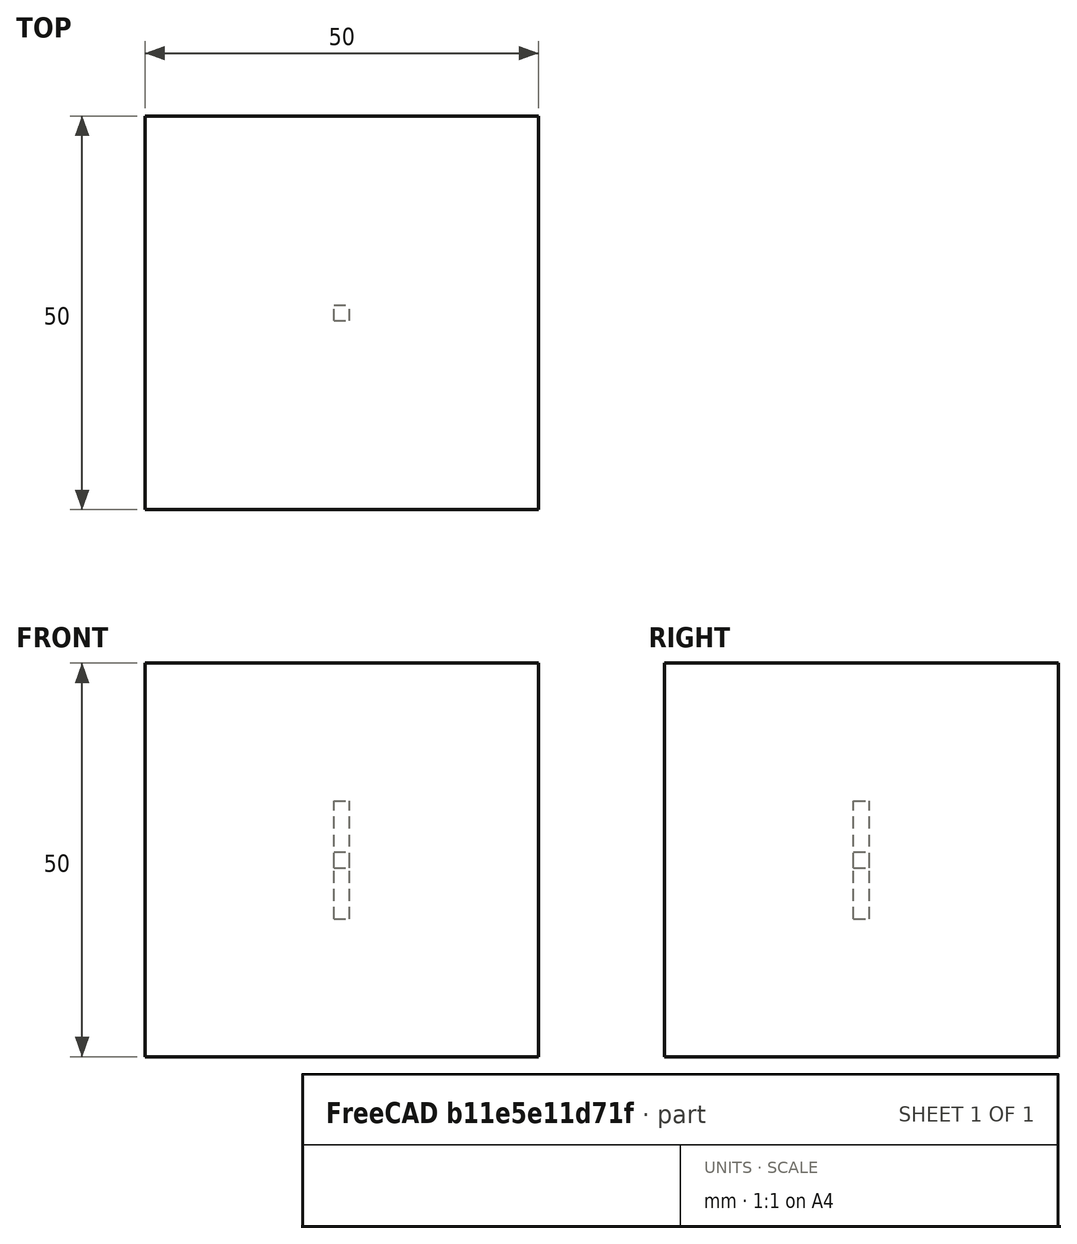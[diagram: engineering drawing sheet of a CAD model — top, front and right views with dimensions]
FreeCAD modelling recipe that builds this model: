
FCSTD DOCUMENT  (FreeCAD 0.22R36391 (Git))
Label: COG_Expanded_simple_array
License: All rights reserved
LicenseURL: http://en.wikipedia.org/wiki/All_rights_reserved
objects: App::DocumentObjectGroupPython×1269, App::Part×7, Part::FeaturePython×6, App::Link×4, App::FeaturePython×2
note: 5 computed .brp shape members not serialized (recipe doc carries the construction recipe); baked Part::Feature solids carry a one-line shape summary decoded from their .brp

FEATURE [App::DocumentObjectGroupPython] Constants  # scripted group (container) (typed FeaturePython)
FEATURE [App::DocumentObjectGroupPython] Variables  # scripted group (container) (typed FeaturePython)
FEATURE [App::DocumentObjectGroupPython] Quantities  # scripted group (container) (typed FeaturePython)
FEATURE [App::DocumentObjectGroupPython] Isotopes  # scripted group (container) (typed FeaturePython)
FEATURE [App::DocumentObjectGroupPython] Elements  # scripted group (container) (typed FeaturePython)
FEATURE [App::DocumentObjectGroupPython] G4_CESIUM_IODIDE  label="G4_CESIUM_IODIDE : 1.000"  # scripted group (container) (typed FeaturePython)
  n = 1
FEATURE [App::DocumentObjectGroupPython] LYSO  # scripted group (container) (typed FeaturePython)
  ABSLENGTH = ABSLENGTHLAR
  Dunit = g/cm3
  Dvalue = 7.1
  FASTCOMPONENT = SCINTLAR
  Group = -> [G4_CESIUM_IODIDE]
  RAYLEIGH = RAYLEIGHLAR
  REEMISSIONPROB = SCINTLAR
  RESOLUTIONSCALE = RS
  RINDEX = RINDEXLAR
  SCINTILLATIONCOMPONENT1 = SCINTLAR
  SCINTILLATIONCOMPONENT2 = SCINTLAR
  SCINTILLATIONTIMECONSTANT1 = FTC
  SCINTILLATIONTIMECONSTANT2 = STC
  SCINTILLATIONYIELD = SY
  SCINTILLATIONYIELD1 = RY1
  SCINTILLATIONYIELD2 = RY2
  SLOWCOMPONENT = SCINTLAR
  YIELDRATIO = YR
  conduct = 2
  density = 1
  expand = 3
  name = LYSO
  specific = 4
FEATURE [App::DocumentObjectGroupPython] G4_AIR  label="G4_AIR : 1.000"  # scripted group (container) (typed FeaturePython)
  n = 1
FEATURE [App::DocumentObjectGroupPython] Air  # scripted group (container) (typed FeaturePython)
  Dunit = mg/cm3
  Dvalue = 1.29
  Group = -> [G4_AIR]
  RINDEX = AirRINDEX
  conduct = 2
  density = 1
  expand = 3
  name = Air
  specific = 4
FEATURE [App::DocumentObjectGroupPython] G4_SILICON_DIOXIDE  label="G4_SILICON_DIOXIDE : 1.000"  # scripted group (container) (typed FeaturePython)
  n = 1
FEATURE [App::DocumentObjectGroupPython] Glass  # scripted group (container) (typed FeaturePython)
  Dunit = g/cm3
  Dvalue = 2.32
  Group = -> [G4_SILICON_DIOXIDE]
  RINDEX = RINDEXLAR
  conduct = 2
  density = 1
  expand = 3
  name = Glass
  specific = 4
FEATURE [App::DocumentObjectGroupPython] SY  # scripted group (container) (typed FeaturePython)
  coldim = 1
  values = 100000
FEATURE [App::DocumentObjectGroupPython] RS  # scripted group (container) (typed FeaturePython)
  coldim = 1
  values = 1
FEATURE [App::DocumentObjectGroupPython] FTC  # scripted group (container) (typed FeaturePython)
  coldim = 1
  values = 21.5*ns
FEATURE [App::DocumentObjectGroupPython] STC  # scripted group (container) (typed FeaturePython)
  coldim = 1
  values = 43.8*ns
FEATURE [App::DocumentObjectGroupPython] RY1  # scripted group (container) (typed FeaturePython)
  coldim = 1
  values = 95
FEATURE [App::DocumentObjectGroupPython] RY2  # scripted group (container) (typed FeaturePython)
  coldim = 1
  values = 5
FEATURE [App::DocumentObjectGroupPython] YR  # scripted group (container) (typed FeaturePython)
  coldim = 1
  values = 0.8
FEATURE [App::DocumentObjectGroupPython] SCINTLAR  # scripted group (container) (typed FeaturePython)
  coldim = 2
  values = <blob: 2358 chars omitted>
FEATURE [App::DocumentObjectGroupPython] RINDEXLAR  # scripted group (container) (typed FeaturePython)
  coldim = 2
  values = <blob: 9384 chars omitted>
FEATURE [App::DocumentObjectGroupPython] ABSLENGTHLAR  # scripted group (container) (typed FeaturePython)
  coldim = 2
  values = 7.74901*eV 10.0*m 7.77525*eV 10.0*m 7.80167*eV 10.0*m 7.82827*eV 10.0*m 7.85506*eV 10.0*m 7.88202*eV 10.0*m 7.90917*eV 10.0*m 7.93651*eV 10.0*m 7.96404*eV 10.0*m 7.99176*eV 10.0*m 8.01968*eV 10.0*m 8.04779*eV 10.0*m 8.07609*eV 10.0*m 8.1046*eV 10.0*m 8.13331*eV 10.0*m 8.16222*eV 10.0*m 8.19134*eV 10.0*m 8.22067*eV 10.0*m 8.25021*eV 10.0*m 8.27996*eV 10.0*m 8.30993*eV 10.0*m 8.34012*eV 10.0*m 8.37052*eV 10.0*m 8.40115*eV 10.0*m 8.432*eV 10.0*m 8.46308*eV 10.0*m 8.4944*eV 10.0*m 8.52594*eV 10.0*m 8.55772*eV 10.0*m 8.58973*eV 10.0*m 8.62199*eV 10.0*m 8.65449*eV 10.0*m 8.68723*eV 10.0*m 8.72023*eV 10.0*m 8.75347*eV 10.0*m 8.78697*eV 10.0*m 8.82073*eV 10.0*m 8.85475*eV 10.0*m 8.88903*eV 10.0*m 8.92358*eV 10.0*m 8.9584*eV 10.0*m 8.99349*eV 10.0*m 9.02885*eV 10.0*m 9.0645*eV 10.0*m 9.10043*eV 10.0*m 9.13664*eV 10.0*m 9.17314*eV 10.0*m 9.20994*eV 10.0*m 9.24703*eV 10.0*m 9.28442*eV 10.0*m 9.32212*eV 10.0*m 9.36012*eV 10.0*m 9.39844*eV 10.0*m 9.43707*eV 10.0*m 9.47602*eV 10.0*m 9.51529*eV 10.0*m 9.55489*eV 10.0*m 9.59481*eV 10.0*m 9.63508*eV 10.0*m 9.67568*eV 10.0*m 9.71663*eV 10.0*m 9.75792*eV 10.0*m 9.79957*eV 10.0*m 9.84158*eV 10.0*m 9.88394*eV 10.0*m 9.92668*eV 10.0*m 9.96978*eV 10.0*m 10.0133*eV 10.0*m 10.0571*eV 10.0*m 10.1014*eV 10.0*m 10.146*eV 10.0*m 10.191*eV 10.0*m 10.2365*eV 10.0*m 10.2823*eV 10.0*m 10.3286*eV 10.0*m 10.3752*eV 10.0*m 10.4223*eV 10.0*m 10.4699*eV 10.0*m 10.5178*eV 10.0*m 10.5662*eV 10.0*m 10.6151*eV 10.0*m 10.6644*eV 10.0*m 10.7142*eV 10.0*m 10.7644*eV 10.0*m 10.8151*eV 10.0*m 10.8663*eV 10.0*m 10.9179*eV 10.0*m 10.9701*eV 10.0*m 11.0228*eV 10.0*m 11.076*eV 10.0*m 11.1296*eV 10.0*m 11.1839*eV 10.0*m 11.2386*eV 10.0*m 11.2939*eV 10.0*m 11.3497*eV 10.0*m 11.4061*eV 10.0*m 11.463*eV 10.0*m 11.5206*eV 10.0*m 11.5787*eV 10.0*m 11.6373*eV 10.0*m
FEATURE [App::DocumentObjectGroupPython] RAYLEIGHLAR  # scripted group (container) (typed FeaturePython)
  coldim = 2
  values = 7.74901*eV 90.0*cm 7.77525*eV 90.0*cm 7.80167*eV 90.0*cm 7.82827*eV 90.0*cm 7.85506*eV 90.0*cm 7.88202*eV 90.0*cm 7.90917*eV 90.0*cm 7.93651*eV 90.0*cm 7.96404*eV 90.0*cm 7.99176*eV 90.0*cm 8.01968*eV 90.0*cm 8.04779*eV 90.0*cm 8.07609*eV 90.0*cm 8.1046*eV 90.0*cm 8.13331*eV 90.0*cm 8.16222*eV 90.0*cm 8.19134*eV 90.0*cm 8.22067*eV 90.0*cm 8.25021*eV 90.0*cm 8.27996*eV 90.0*cm 8.30993*eV 90.0*cm 8.34012*eV 90.0*cm 8.37052*eV 90.0*cm 8.40115*eV 90.0*cm 8.432*eV 90.0*cm 8.46308*eV 90.0*cm 8.4944*eV 90.0*cm 8.52594*eV 90.0*cm 8.55772*eV 90.0*cm 8.58973*eV 90.0*cm 8.62199*eV 90.0*cm 8.65449*eV 90.0*cm 8.68723*eV 90.0*cm 8.72023*eV 90.0*cm 8.75347*eV 90.0*cm 8.78697*eV 90.0*cm 8.82073*eV 90.0*cm 8.85475*eV 90.0*cm 8.88903*eV 90.0*cm 8.92358*eV 90.0*cm 8.9584*eV 90.0*cm 8.99349*eV 90.0*cm 9.02885*eV 90.0*cm 9.0645*eV 90.0*cm 9.10043*eV 90.0*cm 9.13664*eV 90.0*cm 9.17314*eV 90.0*cm 9.20994*eV 90.0*cm 9.24703*eV 90.0*cm 9.28442*eV 90.0*cm 9.32212*eV 90.0*cm 9.36012*eV 90.0*cm 9.39844*eV 90.0*cm 9.43707*eV 90.0*cm 9.47602*eV 90.0*cm 9.51529*eV 90.0*cm 9.55489*eV 90.0*cm 9.59481*eV 90.0*cm 9.63508*eV 90.0*cm 9.67568*eV 90.0*cm 9.71663*eV 90.0*cm 9.75792*eV 90.0*cm 9.79957*eV 90.0*cm 9.84158*eV 90.0*cm 9.88394*eV 90.0*cm 9.92668*eV 90.0*cm 9.96978*eV 90.0*cm 10.0133*eV 90.0*cm 10.0571*eV 90.0*cm 10.1014*eV 90.0*cm 10.146*eV 90.0*cm 10.191*eV 90.0*cm 10.2365*eV 90.0*cm 10.2823*eV 90.0*cm 10.3286*eV 90.0*cm 10.3752*eV 90.0*cm 10.4223*eV 90.0*cm 10.4699*eV 90.0*cm 10.5178*eV 90.0*cm 10.5662*eV 90.0*cm 10.6151*eV 90.0*cm 10.6644*eV 90.0*cm 10.7142*eV 90.0*cm 10.7644*eV 90.0*cm 10.8151*eV 90.0*cm 10.8663*eV 90.0*cm 10.9179*eV 90.0*cm 10.9701*eV 90.0*cm 11.0228*eV 90.0*cm 11.076*eV 90.0*cm 11.1296*eV 90.0*cm 11.1839*eV 90.0*cm 11.2386*eV 90.0*cm 11.2939*eV 90.0*cm 11.3497*eV 90.0*cm 11.4061*eV 90.0*cm 11.463*eV 90.0*cm 11.5206*eV 90.0*cm 11.5787*eV 90.0*cm 11.6373*eV 90.0*cm
FEATURE [App::DocumentObjectGroupPython] REFLECTIVITY  # scripted group (container) (typed FeaturePython)
  coldim = 2
  values = 2.034*eV 0.98 2.068*eV 0.98 2.103*eV 0.98 2.139*eV 0.98 2.177*eV 0.98 2.216*eV 0.98 2.256*eV 0.98 2.298*eV 0.98 2.341*eV 0.98 2.386*eV 0.98 2.433*eV 0.98 2.481*eV 0.98 2.532*eV 0.98 2.585*eV 0.98 2.64*eV 0.98 2.697*eV 0.98 2.757*eV 0.98 2.82*eV 0.98 2.885*eV 0.98 2.954*eV 0.98 3.026*eV 0.98 3.102*eV 0.98 3.181*eV 0.98 3.265*eV 0.98 3.353*eV 0.98 3.446*eV 0.98 3.545*eV 0.98 3.649*eV 0.98 3.76*eV 0.98 3.877*eV 0.98 4.002*eV 0.98 4.136*eV 0.98 5.0*eV 0.98 6.0*eV 0.98 7.0*eV 0.98 8.0*eV 0.98 9.0*eV 0.98 9.0*eV 0.98 10.0*eV 0.98 11.0*eV 0.98 11.6*eV 0.98
FEATURE [App::DocumentObjectGroupPython] EFFICIENCY  # scripted group (container) (typed FeaturePython)
  coldim = 2
  values = 2.034*eV 1 2.068*eV 1 2.103*eV 1 2.139*eV 1 2.177*eV 1 2.216*eV 1 2.256*eV 1 2.298*eV 1 2.341*eV 1 2.386*eV 1 2.433*eV 1 2.481*eV 1 2.532*eV 1 2.585*eV 1 2.64*eV 1 2.697*eV 1 2.757*eV 1 2.82*eV 1 2.885*eV 1 2.954*eV 1 3.026*eV 1 3.102*eV 1 3.181*eV  1 3.265*eV 1 3.353*eV 1 3.446*eV 1 3.545*eV 1 3.649*eV 1 3.76*eV 1 3.877*eV 1 4.002*eV 1 4.136*eV 1 5.0*eV 1 6.0*eV 1 7.0*eV 1 8.0*eV 1 9.0*eV 1 9.0*eV 1 10.0*eV 1 11.0*eV 1 11.6*eV 1
FEATURE [App::DocumentObjectGroupPython] AirRINDEX  # scripted group (container) (typed FeaturePython)
  coldim = 2
  values = 2.034*eV 1 2.068*eV 1 2.103*eV 1 2.139*eV 1 2.177*eV 1 2.216*eV 1 2.256*eV 1 2.298*eV 1 2.341*eV 1 2.386*eV 1 2.433*eV 1 2.481*eV 1 2.532*eV 1 2.585*eV 1 2.64*eV 1 2.697*eV 1 2.757*eV 1 2.82*eV 1 2.885*eV 1 2.954*eV 1 3.026*eV 1 3.102*eV 1 3.181*eV 1 3.265*eV 1 3.353*eV 1 3.446*eV 1 3.545*eV 1 3.649*eV 1 3.76*eV 1 3.877*eV 1 4.002*eV 1 4.136*eV 1 5.0*eV 1 6.0*eV 1 7.0*eV 1 8.0*eV 1 9.0*eV 1 10.0*eV 1 11.0*eV 1 11.6*eV 1
FEATURE [App::DocumentObjectGroupPython] Matrix  # scripted group (container) (typed FeaturePython)
  Group = -> [SY,RS,FTC,STC,RY1,RY2,YR,SCINTLAR,RINDEXLAR,ABSLENGTHLAR,RAYLEIGHLAR,REFLECTIVITY,EFFICIENCY,AirRINDEX]
FEATURE [App::DocumentObjectGroupPython] ScintWrap  # scripted group (container) (typed FeaturePython)
  EFFICIENCY = EFFICIENCY
  REFLECTIVITY = REFLECTIVITY
  finish = 39
  model = 0
  type = 2
  value = 1
FEATURE [App::DocumentObjectGroupPython] Surfaces  # scripted group (container) (typed FeaturePython)
  Group = -> [ScintWrap]
FEATURE [App::DocumentObjectGroupPython] Opticals  # scripted group (container) (typed FeaturePython)
  Group = -> [Matrix,Surfaces]
FEATURE [App::DocumentObjectGroupPython] G4Isotopes  # scripted group (container) (typed FeaturePython)
FEATURE [App::DocumentObjectGroupPython] H_element  # scripted group (container) (typed FeaturePython)
  Z = 1
  atom_value = 1.008
  formula = H
  name = H_element
FEATURE [App::DocumentObjectGroupPython] He_element  # scripted group (container) (typed FeaturePython)
  Z = 2
  atom_value = 4.0026
  formula = He
  name = He_element
FEATURE [App::DocumentObjectGroupPython] Li_element  # scripted group (container) (typed FeaturePython)
  Z = 3
  atom_value = 6.94
  formula = Li
  name = Li_element
FEATURE [App::DocumentObjectGroupPython] Be_element  # scripted group (container) (typed FeaturePython)
  Z = 4
  atom_value = 9.01218
  formula = Be
  name = Be_element
FEATURE [App::DocumentObjectGroupPython] B_element  # scripted group (container) (typed FeaturePython)
  Z = 5
  atom_value = 10.81
  formula = B
  name = B_element
FEATURE [App::DocumentObjectGroupPython] C_element  # scripted group (container) (typed FeaturePython)
  Z = 6
  atom_value = 12.011
  formula = C
  name = C_element
FEATURE [App::DocumentObjectGroupPython] N_element  # scripted group (container) (typed FeaturePython)
  Z = 7
  atom_value = 14.007
  formula = N
  name = N_element
FEATURE [App::DocumentObjectGroupPython] O_element  # scripted group (container) (typed FeaturePython)
  Z = 8
  atom_value = 15.999
  formula = O
  name = O_element
FEATURE [App::DocumentObjectGroupPython] F_element  # scripted group (container) (typed FeaturePython)
  Z = 9
  atom_value = 18.9984
  formula = F
  name = F_element
FEATURE [App::DocumentObjectGroupPython] Ne_element  # scripted group (container) (typed FeaturePython)
  Z = 10
  atom_value = 20.1797
  formula = Ne
  name = Ne_element
FEATURE [App::DocumentObjectGroupPython] Na_element  # scripted group (container) (typed FeaturePython)
  Z = 11
  atom_value = 22.9898
  formula = Na
  name = Na_element
FEATURE [App::DocumentObjectGroupPython] Mg_element  # scripted group (container) (typed FeaturePython)
  Z = 12
  atom_value = 24.305
  formula = Mg
  name = Mg_element
FEATURE [App::DocumentObjectGroupPython] Al_element  # scripted group (container) (typed FeaturePython)
  Z = 13
  atom_value = 26.9815
  formula = Al
  name = Al_element
FEATURE [App::DocumentObjectGroupPython] Si_element  # scripted group (container) (typed FeaturePython)
  Z = 14
  atom_value = 28.085
  formula = Si
  name = Si_element
FEATURE [App::DocumentObjectGroupPython] P_element  # scripted group (container) (typed FeaturePython)
  Z = 15
  atom_value = 30.9738
  formula = P
  name = P_element
FEATURE [App::DocumentObjectGroupPython] S_element  # scripted group (container) (typed FeaturePython)
  Z = 16
  atom_value = 32.06
  formula = S
  name = S_element
FEATURE [App::DocumentObjectGroupPython] Cl_element  # scripted group (container) (typed FeaturePython)
  Z = 17
  atom_value = 35.45
  formula = Cl
  name = Cl_element
FEATURE [App::DocumentObjectGroupPython] Ar_element  # scripted group (container) (typed FeaturePython)
  Z = 18
  atom_value = 39.95
  formula = Ar
  name = Ar_element
FEATURE [App::DocumentObjectGroupPython] K_element  # scripted group (container) (typed FeaturePython)
  Z = 19
  atom_value = 39.0983
  formula = K
  name = K_element
FEATURE [App::DocumentObjectGroupPython] Ca_element  # scripted group (container) (typed FeaturePython)
  Z = 20
  atom_value = 40.078
  formula = Ca
  name = Ca_element
FEATURE [App::DocumentObjectGroupPython] Sc_element  # scripted group (container) (typed FeaturePython)
  Z = 21
  atom_value = 44.9559
  formula = Sc
  name = Sc_element
FEATURE [App::DocumentObjectGroupPython] Ti_element  # scripted group (container) (typed FeaturePython)
  Z = 22
  atom_value = 47.867
  formula = Ti
  name = Ti_element
FEATURE [App::DocumentObjectGroupPython] V_element  # scripted group (container) (typed FeaturePython)
  Z = 23
  atom_value = 50.9415
  formula = V
  name = V_element
FEATURE [App::DocumentObjectGroupPython] Cr_element  # scripted group (container) (typed FeaturePython)
  Z = 24
  atom_value = 51.9961
  formula = Cr
  name = Cr_element
FEATURE [App::DocumentObjectGroupPython] Mn_element  # scripted group (container) (typed FeaturePython)
  Z = 25
  atom_value = 54.938
  formula = Mn
  name = Mn_element
FEATURE [App::DocumentObjectGroupPython] Fe_element  # scripted group (container) (typed FeaturePython)
  Z = 26
  atom_value = 55.845
  formula = Fe
  name = Fe_element
FEATURE [App::DocumentObjectGroupPython] Co_element  # scripted group (container) (typed FeaturePython)
  Z = 27
  atom_value = 58.9332
  formula = Co
  name = Co_element
FEATURE [App::DocumentObjectGroupPython] Ni_element  # scripted group (container) (typed FeaturePython)
  Z = 28
  atom_value = 58.6934
  formula = Ni
  name = Ni_element
FEATURE [App::DocumentObjectGroupPython] Cu_element  # scripted group (container) (typed FeaturePython)
  Z = 29
  atom_value = 63.546
  formula = Cu
  name = Cu_element
FEATURE [App::DocumentObjectGroupPython] Zn_element  # scripted group (container) (typed FeaturePython)
  Z = 30
  atom_value = 65.38
  formula = Zn
  name = Zn_element
FEATURE [App::DocumentObjectGroupPython] Ga_element  # scripted group (container) (typed FeaturePython)
  Z = 31
  atom_value = 69.723
  formula = Ga
  name = Ga_element
FEATURE [App::DocumentObjectGroupPython] Ge_element  # scripted group (container) (typed FeaturePython)
  Z = 32
  atom_value = 72.63
  formula = Ge
  name = Ge_element
FEATURE [App::DocumentObjectGroupPython] As_element  # scripted group (container) (typed FeaturePython)
  Z = 33
  atom_value = 74.9216
  formula = As
  name = As_element
FEATURE [App::DocumentObjectGroupPython] Se_element  # scripted group (container) (typed FeaturePython)
  Z = 34
  atom_value = 78.971
  formula = Se
  name = Se_element
FEATURE [App::DocumentObjectGroupPython] Br_element  # scripted group (container) (typed FeaturePython)
  Z = 35
  atom_value = 79.904
  formula = Br
  name = Br_element
FEATURE [App::DocumentObjectGroupPython] Kr_element  # scripted group (container) (typed FeaturePython)
  Z = 36
  atom_value = 83.798
  formula = Kr
  name = Kr_element
FEATURE [App::DocumentObjectGroupPython] Rb_element  # scripted group (container) (typed FeaturePython)
  Z = 37
  atom_value = 85.4678
  formula = Rb
  name = Rb_element
FEATURE [App::DocumentObjectGroupPython] Sr_element  # scripted group (container) (typed FeaturePython)
  Z = 38
  atom_value = 87.62
  formula = Sr
  name = Sr_element
FEATURE [App::DocumentObjectGroupPython] Y_element  # scripted group (container) (typed FeaturePython)
  Z = 39
  atom_value = 88.9058
  formula = Y
  name = Y_element
FEATURE [App::DocumentObjectGroupPython] Zr_element  # scripted group (container) (typed FeaturePython)
  Z = 40
  atom_value = 91.224
  formula = Zr
  name = Zr_element
FEATURE [App::DocumentObjectGroupPython] Nb_element  # scripted group (container) (typed FeaturePython)
  Z = 41
  atom_value = 92.9064
  formula = Nb
  name = Nb_element
FEATURE [App::DocumentObjectGroupPython] Mo_element  # scripted group (container) (typed FeaturePython)
  Z = 42
  atom_value = 95.95
  formula = Mo
  name = Mo_element
FEATURE [App::DocumentObjectGroupPython] Tc_element  # scripted group (container) (typed FeaturePython)
  Z = 43
  atom_value = 97
  formula = Tc
  name = Tc_element
FEATURE [App::DocumentObjectGroupPython] Ru_element  # scripted group (container) (typed FeaturePython)
  Z = 44
  atom_value = 101.07
  formula = Ru
  name = Ru_element
FEATURE [App::DocumentObjectGroupPython] Rh_element  # scripted group (container) (typed FeaturePython)
  Z = 45
  atom_value = 102.905
  formula = Rh
  name = Rh_element
FEATURE [App::DocumentObjectGroupPython] Pd_element  # scripted group (container) (typed FeaturePython)
  Z = 46
  atom_value = 106.42
  formula = Pd
  name = Pd_element
FEATURE [App::DocumentObjectGroupPython] Ag_element  # scripted group (container) (typed FeaturePython)
  Z = 47
  atom_value = 107.868
  formula = Ag
  name = Ag_element
FEATURE [App::DocumentObjectGroupPython] Cd_element  # scripted group (container) (typed FeaturePython)
  Z = 48
  atom_value = 112.414
  formula = Cd
  name = Cd_element
FEATURE [App::DocumentObjectGroupPython] In_element  # scripted group (container) (typed FeaturePython)
  Z = 49
  atom_value = 114.818
  formula = In
  name = In_element
FEATURE [App::DocumentObjectGroupPython] Sn_element  # scripted group (container) (typed FeaturePython)
  Z = 50
  atom_value = 118.71
  formula = Sn
  name = Sn_element
FEATURE [App::DocumentObjectGroupPython] Sb_element  # scripted group (container) (typed FeaturePython)
  Z = 51
  atom_value = 121.76
  formula = Sb
  name = Sb_element
FEATURE [App::DocumentObjectGroupPython] Te_element  # scripted group (container) (typed FeaturePython)
  Z = 52
  atom_value = 127.6
  formula = Te
  name = Te_element
FEATURE [App::DocumentObjectGroupPython] I_element  # scripted group (container) (typed FeaturePython)
  Z = 53
  atom_value = 126.904
  formula = I
  name = I_element
FEATURE [App::DocumentObjectGroupPython] Xe_element  # scripted group (container) (typed FeaturePython)
  Z = 54
  atom_value = 131.293
  formula = Xe
  name = Xe_element
FEATURE [App::DocumentObjectGroupPython] Cs_element  # scripted group (container) (typed FeaturePython)
  Z = 55
  atom_value = 132.905
  formula = Cs
  name = Cs_element
FEATURE [App::DocumentObjectGroupPython] Ba_element  # scripted group (container) (typed FeaturePython)
  Z = 56
  atom_value = 137.327
  formula = Ba
  name = Ba_element
FEATURE [App::DocumentObjectGroupPython] La_element  # scripted group (container) (typed FeaturePython)
  Z = 57
  atom_value = 138.905
  formula = La
  name = La_element
FEATURE [App::DocumentObjectGroupPython] Ce_element  # scripted group (container) (typed FeaturePython)
  Z = 58
  atom_value = 140.116
  formula = Ce
  name = Ce_element
FEATURE [App::DocumentObjectGroupPython] Pr_element  # scripted group (container) (typed FeaturePython)
  Z = 59
  atom_value = 140.908
  formula = Pr
  name = Pr_element
FEATURE [App::DocumentObjectGroupPython] Nd_element  # scripted group (container) (typed FeaturePython)
  Z = 60
  atom_value = 144.242
  formula = Nd
  name = Nd_element
FEATURE [App::DocumentObjectGroupPython] Pm_element  # scripted group (container) (typed FeaturePython)
  Z = 61
  atom_value = 145
  formula = Pm
  name = Pm_element
FEATURE [App::DocumentObjectGroupPython] Sm_element  # scripted group (container) (typed FeaturePython)
  Z = 62
  atom_value = 150.36
  formula = Sm
  name = Sm_element
FEATURE [App::DocumentObjectGroupPython] Eu_element  # scripted group (container) (typed FeaturePython)
  Z = 63
  atom_value = 151.964
  formula = Eu
  name = Eu_element
FEATURE [App::DocumentObjectGroupPython] Gd_element  # scripted group (container) (typed FeaturePython)
  Z = 64
  atom_value = 157.25
  formula = Gd
  name = Gd_element
FEATURE [App::DocumentObjectGroupPython] Tb_element  # scripted group (container) (typed FeaturePython)
  Z = 65
  atom_value = 158.925
  formula = Tb
  name = Tb_element
FEATURE [App::DocumentObjectGroupPython] Dy_element  # scripted group (container) (typed FeaturePython)
  Z = 66
  atom_value = 162.5
  formula = Dy
  name = Dy_element
FEATURE [App::DocumentObjectGroupPython] Ho_element  # scripted group (container) (typed FeaturePython)
  Z = 67
  atom_value = 164.93
  formula = Ho
  name = Ho_element
FEATURE [App::DocumentObjectGroupPython] Er_element  # scripted group (container) (typed FeaturePython)
  Z = 68
  atom_value = 167.259
  formula = Er
  name = Er_element
FEATURE [App::DocumentObjectGroupPython] Tm_element  # scripted group (container) (typed FeaturePython)
  Z = 69
  atom_value = 168.934
  formula = Tm
  name = Tm_element
FEATURE [App::DocumentObjectGroupPython] Yb_element  # scripted group (container) (typed FeaturePython)
  Z = 70
  atom_value = 173.045
  formula = Yb
  name = Yb_element
FEATURE [App::DocumentObjectGroupPython] Lu_element  # scripted group (container) (typed FeaturePython)
  Z = 71
  atom_value = 174.967
  formula = Lu
  name = Lu_element
FEATURE [App::DocumentObjectGroupPython] Hf_element  # scripted group (container) (typed FeaturePython)
  Z = 72
  atom_value = 178.49
  formula = Hf
  name = Hf_element
FEATURE [App::DocumentObjectGroupPython] Ta_element  # scripted group (container) (typed FeaturePython)
  Z = 73
  atom_value = 180.948
  formula = Ta
  name = Ta_element
FEATURE [App::DocumentObjectGroupPython] W_element  # scripted group (container) (typed FeaturePython)
  Z = 74
  atom_value = 183.84
  formula = W
  name = W_element
FEATURE [App::DocumentObjectGroupPython] Re_element  # scripted group (container) (typed FeaturePython)
  Z = 75
  atom_value = 186.207
  formula = Re
  name = Re_element
FEATURE [App::DocumentObjectGroupPython] Os_element  # scripted group (container) (typed FeaturePython)
  Z = 76
  atom_value = 190.23
  formula = Os
  name = Os_element
FEATURE [App::DocumentObjectGroupPython] Ir_element  # scripted group (container) (typed FeaturePython)
  Z = 77
  atom_value = 192.217
  formula = Ir
  name = Ir_element
FEATURE [App::DocumentObjectGroupPython] Pt_element  # scripted group (container) (typed FeaturePython)
  Z = 78
  atom_value = 195.084
  formula = Pt
  name = Pt_element
FEATURE [App::DocumentObjectGroupPython] Au_element  # scripted group (container) (typed FeaturePython)
  Z = 79
  atom_value = 196.967
  formula = Au
  name = Au_element
FEATURE [App::DocumentObjectGroupPython] Hg_element  # scripted group (container) (typed FeaturePython)
  Z = 80
  atom_value = 200.592
  formula = Hg
  name = Hg_element
FEATURE [App::DocumentObjectGroupPython] Tl_element  # scripted group (container) (typed FeaturePython)
  Z = 81
  atom_value = 204.38
  formula = Tl
  name = Tl_element
FEATURE [App::DocumentObjectGroupPython] Pb_element  # scripted group (container) (typed FeaturePython)
  Z = 82
  atom_value = 207.2
  formula = Pb
  name = Pb_element
FEATURE [App::DocumentObjectGroupPython] Bi_element  # scripted group (container) (typed FeaturePython)
  Z = 83
  atom_value = 208.98
  formula = Bi
  name = Bi_element
FEATURE [App::DocumentObjectGroupPython] Po_element  # scripted group (container) (typed FeaturePython)
  Z = 84
  atom_value = 209
  formula = Po
  name = Po_element
FEATURE [App::DocumentObjectGroupPython] At_element  # scripted group (container) (typed FeaturePython)
  Z = 85
  atom_value = 210
  formula = At
  name = At_element
FEATURE [App::DocumentObjectGroupPython] Rn_element  # scripted group (container) (typed FeaturePython)
  Z = 86
  atom_value = 222
  formula = Rn
  name = Rn_element
FEATURE [App::DocumentObjectGroupPython] Fr_element  # scripted group (container) (typed FeaturePython)
  Z = 87
  atom_value = 223
  formula = Fr
  name = Fr_element
FEATURE [App::DocumentObjectGroupPython] Ra_element  # scripted group (container) (typed FeaturePython)
  Z = 88
  atom_value = 226
  formula = Ra
  name = Ra_element
FEATURE [App::DocumentObjectGroupPython] Ac_element  # scripted group (container) (typed FeaturePython)
  Z = 89
  atom_value = 227
  formula = Ac
  name = Ac_element
FEATURE [App::DocumentObjectGroupPython] Th_element  # scripted group (container) (typed FeaturePython)
  Z = 90
  atom_value = 232.038
  formula = Th
  name = Th_element
FEATURE [App::DocumentObjectGroupPython] Pa_element  # scripted group (container) (typed FeaturePython)
  Z = 91
  atom_value = 231.036
  formula = Pa
  name = Pa_element
FEATURE [App::DocumentObjectGroupPython] U_element  # scripted group (container) (typed FeaturePython)
  Z = 92
  atom_value = 238.029
  formula = U
  name = U_element
FEATURE [App::DocumentObjectGroupPython] Np_element  # scripted group (container) (typed FeaturePython)
  Z = 93
  atom_value = 237
  formula = Np
  name = Np_element
FEATURE [App::DocumentObjectGroupPython] Pu_element  # scripted group (container) (typed FeaturePython)
  Z = 94
  atom_value = 244
  formula = Pu
  name = Pu_element
FEATURE [App::DocumentObjectGroupPython] Am_element  # scripted group (container) (typed FeaturePython)
  Z = 95
  atom_value = 243
  formula = Am
  name = Am_element
FEATURE [App::DocumentObjectGroupPython] Cm_element  # scripted group (container) (typed FeaturePython)
  Z = 96
  atom_value = 247
  formula = Cm
  name = Cm_element
FEATURE [App::DocumentObjectGroupPython] Bk_element  # scripted group (container) (typed FeaturePython)
  Z = 97
  atom_value = 247
  formula = Bk
  name = Bk_element
FEATURE [App::DocumentObjectGroupPython] Cf_element  # scripted group (container) (typed FeaturePython)
  Z = 98
  atom_value = 251
  formula = Cf
  name = Cf_element
FEATURE [App::DocumentObjectGroupPython] G4Elements  # scripted group (container) (typed FeaturePython)
  Group = -> [H_element,He_element,Li_element,Be_element,B_element,C_element,N_element,O_element,F_element,Ne_element,Na_element,Mg_element,Al_element,Si_element,P_element,S_element,Cl_element,Ar_element,K_element,Ca_element,Sc_element,Ti_element,V_element,Cr_element,Mn_element,Fe_element,Co_element,Ni_element,Cu_element,Zn_element,Ga_element,Ge_element,As_element,Se_element,Br_element,Kr_element,Rb_element,+61 more]
FEATURE [App::DocumentObjectGroupPython] H_element001  label="H_element : 0.101"  # scripted group (container) (typed FeaturePython)
  n = 0.101327
FEATURE [App::DocumentObjectGroupPython] C_element001  label="C_element : 0.775"  # scripted group (container) (typed FeaturePython)
  n = 0.7755
FEATURE [App::DocumentObjectGroupPython] N_element001  label="N_element : 0.035"  # scripted group (container) (typed FeaturePython)
  n = 0.035057
FEATURE [App::DocumentObjectGroupPython] O_element001  label="O_element : 0.052"  # scripted group (container) (typed FeaturePython)
  n = 0.0523159
FEATURE [App::DocumentObjectGroupPython] F_element001  label="F_element : 0.017"  # scripted group (container) (typed FeaturePython)
  n = 0.017422
FEATURE [App::DocumentObjectGroupPython] Ca_element001  label="Ca_element : 0.018"  # scripted group (container) (typed FeaturePython)
  n = 0.018378
FEATURE [App::DocumentObjectGroupPython] G4_A_150_TISSUE  label="G4_A-150_TISSUE"  # scripted group (container) (typed FeaturePython)
  Dunit = g/cm3
  Dvalue = 1.127
  Group = -> [H_element001,C_element001,N_element001,O_element001,F_element001,Ca_element001]
  conduct = 2
  density = 1
  expand = 3
  formula = G4_A-150_TISSUE
  name = G4_A-150_TISSUE
  specific = 4
FEATURE [App::DocumentObjectGroupPython] C_element002  label="C_element : 3"  # scripted group (container) (typed FeaturePython)
  n = 3
  ref = C_element
FEATURE [App::DocumentObjectGroupPython] H_element002  label="H_element : 6"  # scripted group (container) (typed FeaturePython)
  n = 6
  ref = H_element
FEATURE [App::DocumentObjectGroupPython] O_element002  label="O_element : 1"  # scripted group (container) (typed FeaturePython)
  n = 1
  ref = O_element
FEATURE [App::DocumentObjectGroupPython] G4_ACETONE  # scripted group (container) (typed FeaturePython)
  Dunit = g/cm3
  Dvalue = 0.7899
  Group = -> [C_element002,H_element002,O_element002]
  conduct = 2
  density = 1
  expand = 3
  formula = G4_ACETONE
  name = G4_ACETONE
  specific = 4
FEATURE [App::DocumentObjectGroupPython] C_element003  label="C_element : 2"  # scripted group (container) (typed FeaturePython)
  n = 2
  ref = C_element
FEATURE [App::DocumentObjectGroupPython] H_element003  label="H_element : 2"  # scripted group (container) (typed FeaturePython)
  n = 2
  ref = H_element
FEATURE [App::DocumentObjectGroupPython] G4_ACETYLENE  # scripted group (container) (typed FeaturePython)
  Dunit = g/cm3
  Dvalue = 0.0010967
  Group = -> [C_element003,H_element003]
  conduct = 2
  density = 1
  expand = 3
  formula = G4_ACETYLENE
  name = G4_ACETYLENE
  specific = 4
FEATURE [App::DocumentObjectGroupPython] C_element004  label="C_element : 5"  # scripted group (container) (typed FeaturePython)
  n = 5
  ref = C_element
FEATURE [App::DocumentObjectGroupPython] H_element004  label="H_element : 5"  # scripted group (container) (typed FeaturePython)
  n = 5
  ref = H_element
FEATURE [App::DocumentObjectGroupPython] N_element002  label="N_element : 5"  # scripted group (container) (typed FeaturePython)
  n = 5
  ref = N_element
FEATURE [App::DocumentObjectGroupPython] G4_ADENINE  # scripted group (container) (typed FeaturePython)
  Dunit = g/cm3
  Dvalue = 1.6
  Group = -> [C_element004,H_element004,N_element002]
  conduct = 2
  density = 1
  expand = 3
  formula = G4_ADENINE
  name = G4_ADENINE
  specific = 4
FEATURE [App::DocumentObjectGroupPython] H_element005  label="H_element : 0.114"  # scripted group (container) (typed FeaturePython)
  n = 0.114
FEATURE [App::DocumentObjectGroupPython] C_element005  label="C_element : 0.598"  # scripted group (container) (typed FeaturePython)
  n = 0.598
FEATURE [App::DocumentObjectGroupPython] N_element003  label="N_element : 0.007"  # scripted group (container) (typed FeaturePython)
  n = 0.007
FEATURE [App::DocumentObjectGroupPython] O_element003  label="O_element : 0.278"  # scripted group (container) (typed FeaturePython)
  n = 0.278
FEATURE [App::DocumentObjectGroupPython] Na_element001  label="Na_element : 0.001"  # scripted group (container) (typed FeaturePython)
  n = 0.001
FEATURE [App::DocumentObjectGroupPython] S_element001  label="S_element : 0.001"  # scripted group (container) (typed FeaturePython)
  n = 0.001
FEATURE [App::DocumentObjectGroupPython] Cl_element001  label="Cl_element : 0.001"  # scripted group (container) (typed FeaturePython)
  n = 0.001
FEATURE [App::DocumentObjectGroupPython] G4_ADIPOSE_TISSUE_ICRP  # scripted group (container) (typed FeaturePython)
  Dunit = g/cm3
  Dvalue = 0.95
  Group = -> [H_element005,C_element005,N_element003,O_element003,Na_element001,S_element001,Cl_element001]
  conduct = 2
  density = 1
  expand = 3
  formula = G4_ADIPOSE_TISSUE_ICRP
  name = G4_ADIPOSE_TISSUE_ICRP
  specific = 4
FEATURE [App::DocumentObjectGroupPython] C_element006  label="C_element : 0.000"  # scripted group (container) (typed FeaturePython)
  n = 0.000124
FEATURE [App::DocumentObjectGroupPython] N_element004  label="N_element : 0.755"  # scripted group (container) (typed FeaturePython)
  n = 0.755268
FEATURE [App::DocumentObjectGroupPython] O_element004  label="O_element : 0.232"  # scripted group (container) (typed FeaturePython)
  n = 0.231781
FEATURE [App::DocumentObjectGroupPython] Ar_element001  label="Ar_element : 0.013"  # scripted group (container) (typed FeaturePython)
  n = 0.012827
FEATURE [App::DocumentObjectGroupPython] G4_AIR001  label="G4_AIR"  # scripted group (container) (typed FeaturePython)
  Dunit = g/cm3
  Dvalue = 0.00120479
  Group = -> [C_element006,N_element004,O_element004,Ar_element001]
  conduct = 2
  density = 1
  expand = 3
  formula = G4_AIR
  name = G4_AIR
  specific = 4
FEATURE [App::DocumentObjectGroupPython] C_element007  label="C_element : 006"  # scripted group (container) (typed FeaturePython)
  n = 3
  ref = C_element
FEATURE [App::DocumentObjectGroupPython] H_element006  label="H_element : 7"  # scripted group (container) (typed FeaturePython)
  n = 7
  ref = H_element
FEATURE [App::DocumentObjectGroupPython] N_element005  label="N_element : 1"  # scripted group (container) (typed FeaturePython)
  n = 1
  ref = N_element
FEATURE [App::DocumentObjectGroupPython] O_element005  label="O_element : 2"  # scripted group (container) (typed FeaturePython)
  n = 2
  ref = O_element
FEATURE [App::DocumentObjectGroupPython] G4_ALANINE  # scripted group (container) (typed FeaturePython)
  Dunit = g/cm3
  Dvalue = 1.42
  Group = -> [C_element007,H_element006,N_element005,O_element005]
  conduct = 2
  density = 1
  expand = 3
  formula = G4_ALANINE
  name = G4_ALANINE
  specific = 4
FEATURE [App::DocumentObjectGroupPython] Al_element001  label="Al_element : 2"  # scripted group (container) (typed FeaturePython)
  n = 2
  ref = Al_element
FEATURE [App::DocumentObjectGroupPython] O_element006  label="O_element : 3"  # scripted group (container) (typed FeaturePython)
  n = 3
  ref = O_element
FEATURE [App::DocumentObjectGroupPython] G4_ALUMINUM_OXIDE  # scripted group (container) (typed FeaturePython)
  Dunit = g/cm3
  Dvalue = 3.97
  Group = -> [Al_element001,O_element006]
  conduct = 2
  density = 1
  expand = 3
  formula = G4_ALUMINUM_OXIDE
  name = G4_ALUMINUM_OXIDE
  specific = 4
FEATURE [App::DocumentObjectGroupPython] H_element007  label="H_element : 0.106"  # scripted group (container) (typed FeaturePython)
  n = 0.10593
FEATURE [App::DocumentObjectGroupPython] C_element008  label="C_element : 0.789"  # scripted group (container) (typed FeaturePython)
  n = 0.788974
FEATURE [App::DocumentObjectGroupPython] O_element007  label="O_element : 0.105"  # scripted group (container) (typed FeaturePython)
  n = 0.105096
FEATURE [App::DocumentObjectGroupPython] G4_AMBER  # scripted group (container) (typed FeaturePython)
  Dunit = g/cm3
  Dvalue = 1.1
  Group = -> [H_element007,C_element008,O_element007]
  conduct = 2
  density = 1
  expand = 3
  formula = G4_AMBER
  name = G4_AMBER
  specific = 4
FEATURE [App::DocumentObjectGroupPython] N_element006  label="N_element : 006"  # scripted group (container) (typed FeaturePython)
  n = 1
  ref = N_element
FEATURE [App::DocumentObjectGroupPython] H_element008  label="H_element : 3"  # scripted group (container) (typed FeaturePython)
  n = 3
  ref = H_element
FEATURE [App::DocumentObjectGroupPython] G4_AMMONIA  # scripted group (container) (typed FeaturePython)
  Dunit = g/cm3
  Dvalue = 0.000826019
  Group = -> [N_element006,H_element008]
  conduct = 2
  density = 1
  expand = 3
  formula = G4_AMMONIA
  name = G4_AMMONIA
  specific = 4
FEATURE [App::DocumentObjectGroupPython] C_element009  label="C_element : 6"  # scripted group (container) (typed FeaturePython)
  n = 6
  ref = C_element
FEATURE [App::DocumentObjectGroupPython] H_element009  label="H_element : 008"  # scripted group (container) (typed FeaturePython)
  n = 7
  ref = H_element
FEATURE [App::DocumentObjectGroupPython] N_element007  label="N_element : 007"  # scripted group (container) (typed FeaturePython)
  n = 1
  ref = N_element
FEATURE [App::DocumentObjectGroupPython] G4_ANILINE  # scripted group (container) (typed FeaturePython)
  Dunit = g/cm3
  Dvalue = 1.0235
  Group = -> [C_element009,H_element009,N_element007]
  conduct = 2
  density = 1
  expand = 3
  formula = G4_ANILINE
  name = G4_ANILINE
  specific = 4
FEATURE [App::DocumentObjectGroupPython] C_element010  label="C_element : 14"  # scripted group (container) (typed FeaturePython)
  n = 14
  ref = C_element
FEATURE [App::DocumentObjectGroupPython] H_element010  label="H_element : 10"  # scripted group (container) (typed FeaturePython)
  n = 10
  ref = H_element
FEATURE [App::DocumentObjectGroupPython] G4_ANTHRACENE  # scripted group (container) (typed FeaturePython)
  Dunit = g/cm3
  Dvalue = 1.283
  Group = -> [C_element010,H_element010]
  conduct = 2
  density = 1
  expand = 3
  formula = G4_ANTHRACENE
  name = G4_ANTHRACENE
  specific = 4
FEATURE [App::DocumentObjectGroupPython] H_element011  label="H_element : 0.065"  # scripted group (container) (typed FeaturePython)
  n = 0.0654709
FEATURE [App::DocumentObjectGroupPython] C_element011  label="C_element : 0.537"  # scripted group (container) (typed FeaturePython)
  n = 0.536944
FEATURE [App::DocumentObjectGroupPython] N_element008  label="N_element : 0.021"  # scripted group (container) (typed FeaturePython)
  n = 0.0215
FEATURE [App::DocumentObjectGroupPython] O_element008  label="O_element : 0.032"  # scripted group (container) (typed FeaturePython)
  n = 0.032085
FEATURE [App::DocumentObjectGroupPython] F_element002  label="F_element : 0.167"  # scripted group (container) (typed FeaturePython)
  n = 0.167411
FEATURE [App::DocumentObjectGroupPython] Ca_element002  label="Ca_element : 0.177"  # scripted group (container) (typed FeaturePython)
  n = 0.176589
FEATURE [App::DocumentObjectGroupPython] G4_B_100_BONE  label="G4_B-100_BONE"  # scripted group (container) (typed FeaturePython)
  Dunit = g/cm3
  Dvalue = 1.45
  Group = -> [H_element011,C_element011,N_element008,O_element008,F_element002,Ca_element002]
  conduct = 2
  density = 1
  expand = 3
  formula = G4_B-100_BONE
  name = G4_B-100_BONE
  specific = 4
FEATURE [App::DocumentObjectGroupPython] H_element012  label="H_element : 0.057"  # scripted group (container) (typed FeaturePython)
  n = 0.057441
FEATURE [App::DocumentObjectGroupPython] C_element012  label="C_element : 0.790"  # scripted group (container) (typed FeaturePython)
  n = 0.774591
FEATURE [App::DocumentObjectGroupPython] O_element009  label="O_element : 0.168"  # scripted group (container) (typed FeaturePython)
  n = 0.167968
FEATURE [App::DocumentObjectGroupPython] G4_BAKELITE  # scripted group (container) (typed FeaturePython)
  Dunit = g/cm3
  Dvalue = 1.25
  Group = -> [H_element012,C_element012,O_element009]
  conduct = 2
  density = 1
  expand = 3
  formula = G4_BAKELITE
  name = G4_BAKELITE
  specific = 4
FEATURE [App::DocumentObjectGroupPython] Ba_element001  label="Ba_element : 1"  # scripted group (container) (typed FeaturePython)
  n = 1
  ref = Ba_element
FEATURE [App::DocumentObjectGroupPython] F_element003  label="F_element : 2"  # scripted group (container) (typed FeaturePython)
  n = 2
  ref = F_element
FEATURE [App::DocumentObjectGroupPython] G4_BARIUM_FLUORIDE  # scripted group (container) (typed FeaturePython)
  Dunit = g/cm3
  Dvalue = 4.89
  Group = -> [Ba_element001,F_element003]
  conduct = 2
  density = 1
  expand = 3
  formula = G4_BARIUM_FLUORIDE
  name = G4_BARIUM_FLUORIDE
  specific = 4
FEATURE [App::DocumentObjectGroupPython] Ba_element002  label="Ba_element : 002"  # scripted group (container) (typed FeaturePython)
  n = 1
  ref = Ba_element
FEATURE [App::DocumentObjectGroupPython] S_element002  label="S_element : 1"  # scripted group (container) (typed FeaturePython)
  n = 1
  ref = S_element
FEATURE [App::DocumentObjectGroupPython] O_element010  label="O_element : 4"  # scripted group (container) (typed FeaturePython)
  n = 4
  ref = O_element
FEATURE [App::DocumentObjectGroupPython] G4_BARIUM_SULFATE  # scripted group (container) (typed FeaturePython)
  Dunit = g/cm3
  Dvalue = 4.5
  Group = -> [Ba_element002,S_element002,O_element010]
  conduct = 2
  density = 1
  expand = 3
  formula = G4_BARIUM_SULFATE
  name = G4_BARIUM_SULFATE
  specific = 4
FEATURE [App::DocumentObjectGroupPython] C_element013  label="C_element : 007"  # scripted group (container) (typed FeaturePython)
  n = 6
  ref = C_element
FEATURE [App::DocumentObjectGroupPython] H_element013  label="H_element : 009"  # scripted group (container) (typed FeaturePython)
  n = 6
  ref = H_element
FEATURE [App::DocumentObjectGroupPython] G4_BENZENE  # scripted group (container) (typed FeaturePython)
  Dunit = g/cm3
  Dvalue = 0.87865
  Group = -> [C_element013,H_element013]
  conduct = 2
  density = 1
  expand = 3
  formula = G4_BENZENE
  name = G4_BENZENE
  specific = 4
FEATURE [App::DocumentObjectGroupPython] Be_element001  label="Be_element : 1"  # scripted group (container) (typed FeaturePython)
  n = 1
  ref = Be_element
FEATURE [App::DocumentObjectGroupPython] O_element011  label="O_element : 005"  # scripted group (container) (typed FeaturePython)
  n = 1
  ref = O_element
FEATURE [App::DocumentObjectGroupPython] G4_BERYLLIUM_OXIDE  # scripted group (container) (typed FeaturePython)
  Dunit = g/cm3
  Dvalue = 3.01
  Group = -> [Be_element001,O_element011]
  conduct = 2
  density = 1
  expand = 3
  formula = G4_BERYLLIUM_OXIDE
  name = G4_BERYLLIUM_OXIDE
  specific = 4
FEATURE [App::DocumentObjectGroupPython] Bi_element001  label="Bi_element : 4"  # scripted group (container) (typed FeaturePython)
  n = 4
  ref = Bi_element
FEATURE [App::DocumentObjectGroupPython] Ge_element001  label="Ge_element : 3"  # scripted group (container) (typed FeaturePython)
  n = 3
  ref = Ge_element
FEATURE [App::DocumentObjectGroupPython] O_element012  label="O_element : 12"  # scripted group (container) (typed FeaturePython)
  n = 12
  ref = O_element
FEATURE [App::DocumentObjectGroupPython] G4_BGO  # scripted group (container) (typed FeaturePython)
  Dunit = g/cm3
  Dvalue = 7.13
  Group = -> [Bi_element001,Ge_element001,O_element012]
  conduct = 2
  density = 1
  expand = 3
  formula = G4_BGO
  name = G4_BGO
  specific = 4
FEATURE [App::DocumentObjectGroupPython] H_element014  label="H_element : 0.102"  # scripted group (container) (typed FeaturePython)
  n = 0.102
FEATURE [App::DocumentObjectGroupPython] C_element014  label="C_element : 0.110"  # scripted group (container) (typed FeaturePython)
  n = 0.11
FEATURE [App::DocumentObjectGroupPython] N_element009  label="N_element : 0.033"  # scripted group (container) (typed FeaturePython)
  n = 0.033
FEATURE [App::DocumentObjectGroupPython] O_element013  label="O_element : 0.745"  # scripted group (container) (typed FeaturePython)
  n = 0.745
FEATURE [App::DocumentObjectGroupPython] Na_element002  label="Na_element : 0.002"  # scripted group (container) (typed FeaturePython)
  n = 0.001
FEATURE [App::DocumentObjectGroupPython] P_element001  label="P_element : 0.001"  # scripted group (container) (typed FeaturePython)
  n = 0.001
FEATURE [App::DocumentObjectGroupPython] S_element003  label="S_element : 0.002"  # scripted group (container) (typed FeaturePython)
  n = 0.002
FEATURE [App::DocumentObjectGroupPython] Cl_element002  label="Cl_element : 0.003"  # scripted group (container) (typed FeaturePython)
  n = 0.003
FEATURE [App::DocumentObjectGroupPython] K_element001  label="K_element : 0.002"  # scripted group (container) (typed FeaturePython)
  n = 0.002
FEATURE [App::DocumentObjectGroupPython] Fe_element001  label="Fe_element : 0.001"  # scripted group (container) (typed FeaturePython)
  n = 0.001
FEATURE [App::DocumentObjectGroupPython] G4_BLOOD_ICRP  # scripted group (container) (typed FeaturePython)
  Dunit = g/cm3
  Dvalue = 1.06
  Group = -> [H_element014,C_element014,N_element009,O_element013,Na_element002,P_element001,S_element003,Cl_element002,K_element001,Fe_element001]
  conduct = 2
  density = 1
  expand = 3
  formula = G4_BLOOD_ICRP
  name = G4_BLOOD_ICRP
  specific = 4
FEATURE [App::DocumentObjectGroupPython] H_element015  label="H_element : 0.064"  # scripted group (container) (typed FeaturePython)
  n = 0.064
FEATURE [App::DocumentObjectGroupPython] C_element015  label="C_element : 0.278"  # scripted group (container) (typed FeaturePython)
  n = 0.278
FEATURE [App::DocumentObjectGroupPython] N_element010  label="N_element : 0.027"  # scripted group (container) (typed FeaturePython)
  n = 0.027
FEATURE [App::DocumentObjectGroupPython] O_element014  label="O_element : 0.410"  # scripted group (container) (typed FeaturePython)
  n = 0.41
FEATURE [App::DocumentObjectGroupPython] Mg_element001  label="Mg_element : 0.002"  # scripted group (container) (typed FeaturePython)
  n = 0.002
FEATURE [App::DocumentObjectGroupPython] P_element002  label="P_element : 0.070"  # scripted group (container) (typed FeaturePython)
  n = 0.07
FEATURE [App::DocumentObjectGroupPython] S_element004  label="S_element : 0.003"  # scripted group (container) (typed FeaturePython)
  n = 0.002
FEATURE [App::DocumentObjectGroupPython] Ca_element003  label="Ca_element : 0.147"  # scripted group (container) (typed FeaturePython)
  n = 0.147
FEATURE [App::DocumentObjectGroupPython] G4_BONE_COMPACT_ICRU  # scripted group (container) (typed FeaturePython)
  Dunit = g/cm3
  Dvalue = 1.85
  Group = -> [H_element015,C_element015,N_element010,O_element014,Mg_element001,P_element002,S_element004,Ca_element003]
  conduct = 2
  density = 1
  expand = 3
  formula = G4_BONE_COMPACT_ICRU
  name = G4_BONE_COMPACT_ICRU
  specific = 4
FEATURE [App::DocumentObjectGroupPython] H_element016  label="H_element : 0.034"  # scripted group (container) (typed FeaturePython)
  n = 0.034
FEATURE [App::DocumentObjectGroupPython] C_element016  label="C_element : 0.155"  # scripted group (container) (typed FeaturePython)
  n = 0.155
FEATURE [App::DocumentObjectGroupPython] N_element011  label="N_element : 0.042"  # scripted group (container) (typed FeaturePython)
  n = 0.042
FEATURE [App::DocumentObjectGroupPython] O_element015  label="O_element : 0.435"  # scripted group (container) (typed FeaturePython)
  n = 0.435
FEATURE [App::DocumentObjectGroupPython] Na_element003  label="Na_element : 0.003"  # scripted group (container) (typed FeaturePython)
  n = 0.001
FEATURE [App::DocumentObjectGroupPython] Mg_element002  label="Mg_element : 0.003"  # scripted group (container) (typed FeaturePython)
  n = 0.002
FEATURE [App::DocumentObjectGroupPython] P_element003  label="P_element : 0.103"  # scripted group (container) (typed FeaturePython)
  n = 0.103
FEATURE [App::DocumentObjectGroupPython] S_element005  label="S_element : 0.004"  # scripted group (container) (typed FeaturePython)
  n = 0.003
FEATURE [App::DocumentObjectGroupPython] Ca_element004  label="Ca_element : 0.225"  # scripted group (container) (typed FeaturePython)
  n = 0.225
FEATURE [App::DocumentObjectGroupPython] G4_BONE_CORTICAL_ICRP  # scripted group (container) (typed FeaturePython)
  Dunit = g/cm3
  Dvalue = 1.92
  Group = -> [H_element016,C_element016,N_element011,O_element015,Na_element003,Mg_element002,P_element003,S_element005,Ca_element004]
  conduct = 2
  density = 1
  expand = 3
  formula = G4_BONE_CORTICAL_ICRP
  name = G4_BONE_CORTICAL_ICRP
  specific = 4
FEATURE [App::DocumentObjectGroupPython] B_element001  label="B_element : 4"  # scripted group (container) (typed FeaturePython)
  n = 4
  ref = B_element
FEATURE [App::DocumentObjectGroupPython] C_element017  label="C_element : 1"  # scripted group (container) (typed FeaturePython)
  n = 1
  ref = C_element
FEATURE [App::DocumentObjectGroupPython] G4_BORON_CARBIDE  # scripted group (container) (typed FeaturePython)
  Dunit = g/cm3
  Dvalue = 2.52
  Group = -> [B_element001,C_element017]
  conduct = 2
  density = 1
  expand = 3
  formula = G4_BORON_CARBIDE
  name = G4_BORON_CARBIDE
  specific = 4
FEATURE [App::DocumentObjectGroupPython] B_element002  label="B_element : 2"  # scripted group (container) (typed FeaturePython)
  n = 2
  ref = B_element
FEATURE [App::DocumentObjectGroupPython] O_element016  label="O_element : 006"  # scripted group (container) (typed FeaturePython)
  n = 3
  ref = O_element
FEATURE [App::DocumentObjectGroupPython] G4_BORON_OXIDE  # scripted group (container) (typed FeaturePython)
  Dunit = g/cm3
  Dvalue = 1.812
  Group = -> [B_element002,O_element016]
  conduct = 2
  density = 1
  expand = 3
  formula = G4_BORON_OXIDE
  name = G4_BORON_OXIDE
  specific = 4
FEATURE [App::DocumentObjectGroupPython] H_element017  label="H_element : 0.107"  # scripted group (container) (typed FeaturePython)
  n = 0.107
FEATURE [App::DocumentObjectGroupPython] C_element018  label="C_element : 0.145"  # scripted group (container) (typed FeaturePython)
  n = 0.145
FEATURE [App::DocumentObjectGroupPython] N_element012  label="N_element : 0.022"  # scripted group (container) (typed FeaturePython)
  n = 0.022
FEATURE [App::DocumentObjectGroupPython] O_element017  label="O_element : 0.712"  # scripted group (container) (typed FeaturePython)
  n = 0.712
FEATURE [App::DocumentObjectGroupPython] Na_element004  label="Na_element : 0.004"  # scripted group (container) (typed FeaturePython)
  n = 0.002
FEATURE [App::DocumentObjectGroupPython] P_element004  label="P_element : 0.004"  # scripted group (container) (typed FeaturePython)
  n = 0.004
FEATURE [App::DocumentObjectGroupPython] S_element006  label="S_element : 0.005"  # scripted group (container) (typed FeaturePython)
  n = 0.002
FEATURE [App::DocumentObjectGroupPython] Cl_element003  label="Cl_element : 0.004"  # scripted group (container) (typed FeaturePython)
  n = 0.003
FEATURE [App::DocumentObjectGroupPython] K_element002  label="K_element : 0.003"  # scripted group (container) (typed FeaturePython)
  n = 0.003
FEATURE [App::DocumentObjectGroupPython] G4_BRAIN_ICRP  # scripted group (container) (typed FeaturePython)
  Dunit = g/cm3
  Dvalue = 1.04
  Group = -> [H_element017,C_element018,N_element012,O_element017,Na_element004,P_element004,S_element006,Cl_element003,K_element002]
  conduct = 2
  density = 1
  expand = 3
  formula = G4_BRAIN_ICRP
  name = G4_BRAIN_ICRP
  specific = 4
FEATURE [App::DocumentObjectGroupPython] C_element019  label="C_element : 4"  # scripted group (container) (typed FeaturePython)
  n = 4
  ref = C_element
FEATURE [App::DocumentObjectGroupPython] H_element018  label="H_element : 010"  # scripted group (container) (typed FeaturePython)
  n = 10
  ref = H_element
FEATURE [App::DocumentObjectGroupPython] G4_BUTANE  # scripted group (container) (typed FeaturePython)
  Dunit = g/cm3
  Dvalue = 0.00249343
  Group = -> [C_element019,H_element018]
  conduct = 2
  density = 1
  expand = 3
  formula = G4_BUTANE
  name = G4_BUTANE
  specific = 4
FEATURE [App::DocumentObjectGroupPython] C_element020  label="C_element : 008"  # scripted group (container) (typed FeaturePython)
  n = 4
  ref = C_element
FEATURE [App::DocumentObjectGroupPython] H_element019  label="H_element : 011"  # scripted group (container) (typed FeaturePython)
  n = 10
  ref = H_element
FEATURE [App::DocumentObjectGroupPython] O_element018  label="O_element : 007"  # scripted group (container) (typed FeaturePython)
  n = 1
  ref = O_element
FEATURE [App::DocumentObjectGroupPython] G4_N_BUTYL_ALCOHOL  label="G4_N-BUTYL_ALCOHOL"  # scripted group (container) (typed FeaturePython)
  Dunit = g/cm3
  Dvalue = 0.8098
  Group = -> [C_element020,H_element019,O_element018]
  conduct = 2
  density = 1
  expand = 3
  formula = G4_N-BUTYL_ALCOHOL
  name = G4_N-BUTYL_ALCOHOL
  specific = 4
FEATURE [App::DocumentObjectGroupPython] H_element020  label="H_element : 0.025"  # scripted group (container) (typed FeaturePython)
  n = 0.02468
FEATURE [App::DocumentObjectGroupPython] C_element021  label="C_element : 0.502"  # scripted group (container) (typed FeaturePython)
  n = 0.501611
FEATURE [App::DocumentObjectGroupPython] O_element019  label="O_element : 0.005"  # scripted group (container) (typed FeaturePython)
  n = 0.004527
FEATURE [App::DocumentObjectGroupPython] F_element004  label="F_element : 0.465"  # scripted group (container) (typed FeaturePython)
  n = 0.465209
FEATURE [App::DocumentObjectGroupPython] Si_element001  label="Si_element : 0.004"  # scripted group (container) (typed FeaturePython)
  n = 0.003973
FEATURE [App::DocumentObjectGroupPython] G4_C_552  label="G4_C-552"  # scripted group (container) (typed FeaturePython)
  Dunit = g/cm3
  Dvalue = 1.76
  Group = -> [H_element020,C_element021,O_element019,F_element004,Si_element001]
  conduct = 2
  density = 1
  expand = 3
  formula = G4_C-552
  name = G4_C-552
  specific = 4
FEATURE [App::DocumentObjectGroupPython] Cd_element001  label="Cd_element : 1"  # scripted group (container) (typed FeaturePython)
  n = 1
  ref = Cd_element
FEATURE [App::DocumentObjectGroupPython] Te_element001  label="Te_element : 1"  # scripted group (container) (typed FeaturePython)
  n = 1
  ref = Te_element
FEATURE [App::DocumentObjectGroupPython] G4_CADMIUM_TELLURIDE  # scripted group (container) (typed FeaturePython)
  Dunit = g/cm3
  Dvalue = 6.2
  Group = -> [Cd_element001,Te_element001]
  conduct = 2
  density = 1
  expand = 3
  formula = G4_CADMIUM_TELLURIDE
  name = G4_CADMIUM_TELLURIDE
  specific = 4
FEATURE [App::DocumentObjectGroupPython] Cd_element002  label="Cd_element : 002"  # scripted group (container) (typed FeaturePython)
  n = 1
  ref = Cd_element
FEATURE [App::DocumentObjectGroupPython] W_element001  label="W_element : 1"  # scripted group (container) (typed FeaturePython)
  n = 1
  ref = W_element
FEATURE [App::DocumentObjectGroupPython] O_element020  label="O_element : 008"  # scripted group (container) (typed FeaturePython)
  n = 4
  ref = O_element
FEATURE [App::DocumentObjectGroupPython] G4_CADMIUM_TUNGSTATE  # scripted group (container) (typed FeaturePython)
  Dunit = g/cm3
  Dvalue = 7.9
  Group = -> [Cd_element002,W_element001,O_element020]
  conduct = 2
  density = 1
  expand = 3
  formula = G4_CADMIUM_TUNGSTATE
  name = G4_CADMIUM_TUNGSTATE
  specific = 4
FEATURE [App::DocumentObjectGroupPython] Ca_element005  label="Ca_element : 1"  # scripted group (container) (typed FeaturePython)
  n = 1
  ref = Ca_element
FEATURE [App::DocumentObjectGroupPython] C_element022  label="C_element : 009"  # scripted group (container) (typed FeaturePython)
  n = 1
  ref = C_element
FEATURE [App::DocumentObjectGroupPython] O_element021  label="O_element : 009"  # scripted group (container) (typed FeaturePython)
  n = 3
  ref = O_element
FEATURE [App::DocumentObjectGroupPython] G4_CALCIUM_CARBONATE  # scripted group (container) (typed FeaturePython)
  Dunit = g/cm3
  Dvalue = 2.8
  Group = -> [Ca_element005,C_element022,O_element021]
  conduct = 2
  density = 1
  expand = 3
  formula = G4_CALCIUM_CARBONATE
  name = G4_CALCIUM_CARBONATE
  specific = 4
FEATURE [App::DocumentObjectGroupPython] Ca_element006  label="Ca_element : 002"  # scripted group (container) (typed FeaturePython)
  n = 1
  ref = Ca_element
FEATURE [App::DocumentObjectGroupPython] F_element005  label="F_element : 003"  # scripted group (container) (typed FeaturePython)
  n = 2
  ref = F_element
FEATURE [App::DocumentObjectGroupPython] G4_CALCIUM_FLUORIDE  # scripted group (container) (typed FeaturePython)
  Dunit = g/cm3
  Dvalue = 3.18
  Group = -> [Ca_element006,F_element005]
  conduct = 2
  density = 1
  expand = 3
  formula = G4_CALCIUM_FLUORIDE
  name = G4_CALCIUM_FLUORIDE
  specific = 4
FEATURE [App::DocumentObjectGroupPython] Ca_element007  label="Ca_element : 003"  # scripted group (container) (typed FeaturePython)
  n = 1
  ref = Ca_element
FEATURE [App::DocumentObjectGroupPython] O_element022  label="O_element : 010"  # scripted group (container) (typed FeaturePython)
  n = 1
  ref = O_element
FEATURE [App::DocumentObjectGroupPython] G4_CALCIUM_OXIDE  # scripted group (container) (typed FeaturePython)
  Dunit = g/cm3
  Dvalue = 3.3
  Group = -> [Ca_element007,O_element022]
  conduct = 2
  density = 1
  expand = 3
  formula = G4_CALCIUM_OXIDE
  name = G4_CALCIUM_OXIDE
  specific = 4
FEATURE [App::DocumentObjectGroupPython] Ca_element008  label="Ca_element : 004"  # scripted group (container) (typed FeaturePython)
  n = 1
  ref = Ca_element
FEATURE [App::DocumentObjectGroupPython] S_element007  label="S_element : 002"  # scripted group (container) (typed FeaturePython)
  n = 1
  ref = S_element
FEATURE [App::DocumentObjectGroupPython] O_element023  label="O_element : 011"  # scripted group (container) (typed FeaturePython)
  n = 4
  ref = O_element
FEATURE [App::DocumentObjectGroupPython] G4_CALCIUM_SULFATE  # scripted group (container) (typed FeaturePython)
  Dunit = g/cm3
  Dvalue = 2.96
  Group = -> [Ca_element008,S_element007,O_element023]
  conduct = 2
  density = 1
  expand = 3
  formula = G4_CALCIUM_SULFATE
  name = G4_CALCIUM_SULFATE
  specific = 4
FEATURE [App::DocumentObjectGroupPython] Ca_element009  label="Ca_element : 005"  # scripted group (container) (typed FeaturePython)
  n = 1
  ref = Ca_element
FEATURE [App::DocumentObjectGroupPython] W_element002  label="W_element : 002"  # scripted group (container) (typed FeaturePython)
  n = 1
  ref = W_element
FEATURE [App::DocumentObjectGroupPython] O_element024  label="O_element : 012"  # scripted group (container) (typed FeaturePython)
  n = 4
  ref = O_element
FEATURE [App::DocumentObjectGroupPython] G4_CALCIUM_TUNGSTATE  # scripted group (container) (typed FeaturePython)
  Dunit = g/cm3
  Dvalue = 6.062
  Group = -> [Ca_element009,W_element002,O_element024]
  conduct = 2
  density = 1
  expand = 3
  formula = G4_CALCIUM_TUNGSTATE
  name = G4_CALCIUM_TUNGSTATE
  specific = 4
FEATURE [App::DocumentObjectGroupPython] C_element023  label="C_element : 010"  # scripted group (container) (typed FeaturePython)
  n = 1
  ref = C_element
FEATURE [App::DocumentObjectGroupPython] O_element025  label="O_element : 013"  # scripted group (container) (typed FeaturePython)
  n = 2
  ref = O_element
FEATURE [App::DocumentObjectGroupPython] G4_CARBON_DIOXIDE  # scripted group (container) (typed FeaturePython)
  Dunit = g/cm3
  Dvalue = 0.00184212
  Group = -> [C_element023,O_element025]
  conduct = 2
  density = 1
  expand = 3
  formula = G4_CARBON_DIOXIDE
  name = G4_CARBON_DIOXIDE
  specific = 4
FEATURE [App::DocumentObjectGroupPython] C_element024  label="C_element : 011"  # scripted group (container) (typed FeaturePython)
  n = 1
  ref = C_element
FEATURE [App::DocumentObjectGroupPython] Cl_element004  label="Cl_element : 4"  # scripted group (container) (typed FeaturePython)
  n = 4
  ref = Cl_element
FEATURE [App::DocumentObjectGroupPython] G4_CARBON_TETRACHLORIDE  # scripted group (container) (typed FeaturePython)
  Dunit = g/cm3
  Dvalue = 1.594
  Group = -> [C_element024,Cl_element004]
  conduct = 2
  density = 1
  expand = 3
  formula = G4_CARBON_TETRACHLORIDE
  name = G4_CARBON_TETRACHLORIDE
  specific = 4
FEATURE [App::DocumentObjectGroupPython] C_element025  label="C_element : 012"  # scripted group (container) (typed FeaturePython)
  n = 6
  ref = C_element
FEATURE [App::DocumentObjectGroupPython] H_element021  label="H_element : 012"  # scripted group (container) (typed FeaturePython)
  n = 10
  ref = H_element
FEATURE [App::DocumentObjectGroupPython] O_element026  label="O_element : 5"  # scripted group (container) (typed FeaturePython)
  n = 5
  ref = O_element
FEATURE [App::DocumentObjectGroupPython] G4_CELLULOSE_CELLOPHANE  # scripted group (container) (typed FeaturePython)
  Dunit = g/cm3
  Dvalue = 1.42
  Group = -> [C_element025,H_element021,O_element026]
  conduct = 2
  density = 1
  expand = 3
  formula = G4_CELLULOSE_CELLOPHANE
  name = G4_CELLULOSE_CELLOPHANE
  specific = 4
FEATURE [App::DocumentObjectGroupPython] H_element022  label="H_element : 0.067"  # scripted group (container) (typed FeaturePython)
  n = 0.067125
FEATURE [App::DocumentObjectGroupPython] C_element026  label="C_element : 0.545"  # scripted group (container) (typed FeaturePython)
  n = 0.545403
FEATURE [App::DocumentObjectGroupPython] O_element027  label="O_element : 0.387"  # scripted group (container) (typed FeaturePython)
  n = 0.387472
FEATURE [App::DocumentObjectGroupPython] G4_CELLULOSE_BUTYRATE  # scripted group (container) (typed FeaturePython)
  Dunit = g/cm3
  Dvalue = 1.2
  Group = -> [H_element022,C_element026,O_element027]
  conduct = 2
  density = 1
  expand = 3
  formula = G4_CELLULOSE_BUTYRATE
  name = G4_CELLULOSE_BUTYRATE
  specific = 4
FEATURE [App::DocumentObjectGroupPython] H_element023  label="H_element : 0.029"  # scripted group (container) (typed FeaturePython)
  n = 0.029216
FEATURE [App::DocumentObjectGroupPython] C_element027  label="C_element : 0.271"  # scripted group (container) (typed FeaturePython)
  n = 0.271296
FEATURE [App::DocumentObjectGroupPython] N_element013  label="N_element : 0.121"  # scripted group (container) (typed FeaturePython)
  n = 0.121276
FEATURE [App::DocumentObjectGroupPython] O_element028  label="O_element : 0.578"  # scripted group (container) (typed FeaturePython)
  n = 0.578212
FEATURE [App::DocumentObjectGroupPython] G4_CELLULOSE_NITRATE  # scripted group (container) (typed FeaturePython)
  Dunit = g/cm3
  Dvalue = 1.49
  Group = -> [H_element023,C_element027,N_element013,O_element028]
  conduct = 2
  density = 1
  expand = 3
  formula = G4_CELLULOSE_NITRATE
  name = G4_CELLULOSE_NITRATE
  specific = 4
FEATURE [App::DocumentObjectGroupPython] H_element024  label="H_element : 0.108"  # scripted group (container) (typed FeaturePython)
  n = 0.107596
FEATURE [App::DocumentObjectGroupPython] N_element014  label="N_element : 0.001"  # scripted group (container) (typed FeaturePython)
  n = 0.0008
FEATURE [App::DocumentObjectGroupPython] O_element029  label="O_element : 0.875"  # scripted group (container) (typed FeaturePython)
  n = 0.874976
FEATURE [App::DocumentObjectGroupPython] S_element008  label="S_element : 0.015"  # scripted group (container) (typed FeaturePython)
  n = 0.014627
FEATURE [App::DocumentObjectGroupPython] Ce_element001  label="Ce_element : 0.002"  # scripted group (container) (typed FeaturePython)
  n = 0.002001
FEATURE [App::DocumentObjectGroupPython] G4_CERIC_SULFATE  # scripted group (container) (typed FeaturePython)
  Dunit = g/cm3
  Dvalue = 1.03
  Group = -> [H_element024,N_element014,O_element029,S_element008,Ce_element001]
  conduct = 2
  density = 1
  expand = 3
  formula = G4_CERIC_SULFATE
  name = G4_CERIC_SULFATE
  specific = 4
FEATURE [App::DocumentObjectGroupPython] Cs_element001  label="Cs_element : 1"  # scripted group (container) (typed FeaturePython)
  n = 1
  ref = Cs_element
FEATURE [App::DocumentObjectGroupPython] F_element006  label="F_element : 1"  # scripted group (container) (typed FeaturePython)
  n = 1
  ref = F_element
FEATURE [App::DocumentObjectGroupPython] G4_CESIUM_FLUORIDE  # scripted group (container) (typed FeaturePython)
  Dunit = g/cm3
  Dvalue = 4.115
  Group = -> [Cs_element001,F_element006]
  conduct = 2
  density = 1
  expand = 3
  formula = G4_CESIUM_FLUORIDE
  name = G4_CESIUM_FLUORIDE
  specific = 4
FEATURE [App::DocumentObjectGroupPython] Cs_element002  label="Cs_element : 002"  # scripted group (container) (typed FeaturePython)
  n = 1
  ref = Cs_element
FEATURE [App::DocumentObjectGroupPython] I_element001  label="I_element : 1"  # scripted group (container) (typed FeaturePython)
  n = 1
  ref = I_element
FEATURE [App::DocumentObjectGroupPython] G4_CESIUM_IODIDE001  label="G4_CESIUM_IODIDE"  # scripted group (container) (typed FeaturePython)
  Dunit = g/cm3
  Dvalue = 4.51
  Group = -> [Cs_element002,I_element001]
  conduct = 2
  density = 1
  expand = 3
  formula = G4_CESIUM_IODIDE
  name = G4_CESIUM_IODIDE
  specific = 4
FEATURE [App::DocumentObjectGroupPython] C_element028  label="C_element : 013"  # scripted group (container) (typed FeaturePython)
  n = 6
  ref = C_element
FEATURE [App::DocumentObjectGroupPython] H_element025  label="H_element : 013"  # scripted group (container) (typed FeaturePython)
  n = 5
  ref = H_element
FEATURE [App::DocumentObjectGroupPython] Cl_element005  label="Cl_element : 1"  # scripted group (container) (typed FeaturePython)
  n = 1
  ref = Cl_element
FEATURE [App::DocumentObjectGroupPython] G4_CHLOROBENZENE  # scripted group (container) (typed FeaturePython)
  Dunit = g/cm3
  Dvalue = 1.1058
  Group = -> [C_element028,H_element025,Cl_element005]
  conduct = 2
  density = 1
  expand = 3
  formula = G4_CHLOROBENZENE
  name = G4_CHLOROBENZENE
  specific = 4
FEATURE [App::DocumentObjectGroupPython] C_element029  label="C_element : 014"  # scripted group (container) (typed FeaturePython)
  n = 1
  ref = C_element
FEATURE [App::DocumentObjectGroupPython] H_element026  label="H_element : 1"  # scripted group (container) (typed FeaturePython)
  n = 1
  ref = H_element
FEATURE [App::DocumentObjectGroupPython] Cl_element006  label="Cl_element : 3"  # scripted group (container) (typed FeaturePython)
  n = 3
  ref = Cl_element
FEATURE [App::DocumentObjectGroupPython] G4_CHLOROFORM  # scripted group (container) (typed FeaturePython)
  Dunit = g/cm3
  Dvalue = 1.4832
  Group = -> [C_element029,H_element026,Cl_element006]
  conduct = 2
  density = 1
  expand = 3
  formula = G4_CHLOROFORM
  name = G4_CHLOROFORM
  specific = 4
FEATURE [App::DocumentObjectGroupPython] H_element027  label="H_element : 0.010"  # scripted group (container) (typed FeaturePython)
  n = 0.01
FEATURE [App::DocumentObjectGroupPython] C_element030  label="C_element : 0.001"  # scripted group (container) (typed FeaturePython)
  n = 0.001
FEATURE [App::DocumentObjectGroupPython] O_element030  label="O_element : 0.529"  # scripted group (container) (typed FeaturePython)
  n = 0.529107
FEATURE [App::DocumentObjectGroupPython] Na_element005  label="Na_element : 0.016"  # scripted group (container) (typed FeaturePython)
  n = 0.016
FEATURE [App::DocumentObjectGroupPython] Mg_element003  label="Mg_element : 0.004"  # scripted group (container) (typed FeaturePython)
  n = 0.002
FEATURE [App::DocumentObjectGroupPython] Al_element002  label="Al_element : 0.034"  # scripted group (container) (typed FeaturePython)
  n = 0.033872
FEATURE [App::DocumentObjectGroupPython] Si_element002  label="Si_element : 0.337"  # scripted group (container) (typed FeaturePython)
  n = 0.337021
FEATURE [App::DocumentObjectGroupPython] K_element003  label="K_element : 0.013"  # scripted group (container) (typed FeaturePython)
  n = 0.013
FEATURE [App::DocumentObjectGroupPython] Ca_element010  label="Ca_element : 0.044"  # scripted group (container) (typed FeaturePython)
  n = 0.044
FEATURE [App::DocumentObjectGroupPython] Fe_element002  label="Fe_element : 0.014"  # scripted group (container) (typed FeaturePython)
  n = 0.014
FEATURE [App::DocumentObjectGroupPython] G4_CONCRETE  # scripted group (container) (typed FeaturePython)
  Dunit = g/cm3
  Dvalue = 2.3
  Group = -> [H_element027,C_element030,O_element030,Na_element005,Mg_element003,Al_element002,Si_element002,K_element003,Ca_element010,Fe_element002]
  conduct = 2
  density = 1
  expand = 3
  formula = G4_CONCRETE
  name = G4_CONCRETE
  specific = 4
FEATURE [App::DocumentObjectGroupPython] C_element031  label="C_element : 015"  # scripted group (container) (typed FeaturePython)
  n = 6
  ref = C_element
FEATURE [App::DocumentObjectGroupPython] H_element028  label="H_element : 12"  # scripted group (container) (typed FeaturePython)
  n = 12
  ref = H_element
FEATURE [App::DocumentObjectGroupPython] G4_CYCLOHEXANE  # scripted group (container) (typed FeaturePython)
  Dunit = g/cm3
  Dvalue = 0.779
  Group = -> [C_element031,H_element028]
  conduct = 2
  density = 1
  expand = 3
  formula = G4_CYCLOHEXANE
  name = G4_CYCLOHEXANE
  specific = 4
FEATURE [App::DocumentObjectGroupPython] C_element032  label="C_element : 016"  # scripted group (container) (typed FeaturePython)
  n = 6
  ref = C_element
FEATURE [App::DocumentObjectGroupPython] H_element029  label="H_element : 4"  # scripted group (container) (typed FeaturePython)
  n = 4
  ref = H_element
FEATURE [App::DocumentObjectGroupPython] Cl_element007  label="Cl_element : 2"  # scripted group (container) (typed FeaturePython)
  n = 2
  ref = Cl_element
FEATURE [App::DocumentObjectGroupPython] G4_1_2_DICHLOROBENZENE  label="G4_1.2-DICHLOROBENZENE"  # scripted group (container) (typed FeaturePython)
  Dunit = g/cm3
  Dvalue = 1.3048
  Group = -> [C_element032,H_element029,Cl_element007]
  conduct = 2
  density = 1
  expand = 3
  formula = G4_1.2-DICHLOROBENZENE
  name = G4_1.2-DICHLOROBENZENE
  specific = 4
FEATURE [App::DocumentObjectGroupPython] C_element033  label="C_element : 017"  # scripted group (container) (typed FeaturePython)
  n = 4
  ref = C_element
FEATURE [App::DocumentObjectGroupPython] H_element030  label="H_element : 8"  # scripted group (container) (typed FeaturePython)
  n = 8
  ref = H_element
FEATURE [App::DocumentObjectGroupPython] O_element031  label="O_element : 014"  # scripted group (container) (typed FeaturePython)
  n = 1
  ref = O_element
FEATURE [App::DocumentObjectGroupPython] Cl_element008  label="Cl_element : 005"  # scripted group (container) (typed FeaturePython)
  n = 2
  ref = Cl_element
FEATURE [App::DocumentObjectGroupPython] G4_DICHLORODIETHYL_ETHER  # scripted group (container) (typed FeaturePython)
  Dunit = g/cm3
  Dvalue = 1.2199
  Group = -> [C_element033,H_element030,O_element031,Cl_element008]
  conduct = 2
  density = 1
  expand = 3
  formula = G4_DICHLORODIETHYL_ETHER
  name = G4_DICHLORODIETHYL_ETHER
  specific = 4
FEATURE [App::DocumentObjectGroupPython] C_element034  label="C_element : 018"  # scripted group (container) (typed FeaturePython)
  n = 2
  ref = C_element
FEATURE [App::DocumentObjectGroupPython] H_element031  label="H_element : 014"  # scripted group (container) (typed FeaturePython)
  n = 4
  ref = H_element
FEATURE [App::DocumentObjectGroupPython] Cl_element009  label="Cl_element : 006"  # scripted group (container) (typed FeaturePython)
  n = 2
  ref = Cl_element
FEATURE [App::DocumentObjectGroupPython] G4_1_2_DICHLOROETHANE  label="G4_1.2-DICHLOROETHANE"  # scripted group (container) (typed FeaturePython)
  Dunit = g/cm3
  Dvalue = 1.2351
  Group = -> [C_element034,H_element031,Cl_element009]
  conduct = 2
  density = 1
  expand = 3
  formula = G4_1.2-DICHLOROETHANE
  name = G4_1.2-DICHLOROETHANE
  specific = 4
FEATURE [App::DocumentObjectGroupPython] C_element035  label="C_element : 019"  # scripted group (container) (typed FeaturePython)
  n = 4
  ref = C_element
FEATURE [App::DocumentObjectGroupPython] H_element032  label="H_element : 015"  # scripted group (container) (typed FeaturePython)
  n = 10
  ref = H_element
FEATURE [App::DocumentObjectGroupPython] O_element032  label="O_element : 015"  # scripted group (container) (typed FeaturePython)
  n = 1
  ref = O_element
FEATURE [App::DocumentObjectGroupPython] G4_DIETHYL_ETHER  # scripted group (container) (typed FeaturePython)
  Dunit = g/cm3
  Dvalue = 0.71378
  Group = -> [C_element035,H_element032,O_element032]
  conduct = 2
  density = 1
  expand = 3
  formula = G4_DIETHYL_ETHER
  name = G4_DIETHYL_ETHER
  specific = 4
FEATURE [App::DocumentObjectGroupPython] C_element036  label="C_element : 020"  # scripted group (container) (typed FeaturePython)
  n = 3
  ref = C_element
FEATURE [App::DocumentObjectGroupPython] H_element033  label="H_element : 016"  # scripted group (container) (typed FeaturePython)
  n = 7
  ref = H_element
FEATURE [App::DocumentObjectGroupPython] N_element015  label="N_element : 008"  # scripted group (container) (typed FeaturePython)
  n = 1
  ref = N_element
FEATURE [App::DocumentObjectGroupPython] O_element033  label="O_element : 016"  # scripted group (container) (typed FeaturePython)
  n = 1
  ref = O_element
FEATURE [App::DocumentObjectGroupPython] G4_N_N_DIMETHYL_FORMAMIDE  label="G4_N.N-DIMETHYL_FORMAMIDE"  # scripted group (container) (typed FeaturePython)
  Dunit = g/cm3
  Dvalue = 0.9487
  Group = -> [C_element036,H_element033,N_element015,O_element033]
  conduct = 2
  density = 1
  expand = 3
  formula = G4_N.N-DIMETHYL_FORMAMIDE
  name = G4_N.N-DIMETHYL_FORMAMIDE
  specific = 4
FEATURE [App::DocumentObjectGroupPython] C_element037  label="C_element : 021"  # scripted group (container) (typed FeaturePython)
  n = 2
  ref = C_element
FEATURE [App::DocumentObjectGroupPython] H_element034  label="H_element : 017"  # scripted group (container) (typed FeaturePython)
  n = 6
  ref = H_element
FEATURE [App::DocumentObjectGroupPython] O_element034  label="O_element : 017"  # scripted group (container) (typed FeaturePython)
  n = 1
  ref = O_element
FEATURE [App::DocumentObjectGroupPython] S_element009  label="S_element : 003"  # scripted group (container) (typed FeaturePython)
  n = 1
  ref = S_element
FEATURE [App::DocumentObjectGroupPython] G4_DIMETHYL_SULFOXIDE  # scripted group (container) (typed FeaturePython)
  Dunit = g/cm3
  Dvalue = 1.1014
  Group = -> [C_element037,H_element034,O_element034,S_element009]
  conduct = 2
  density = 1
  expand = 3
  formula = G4_DIMETHYL_SULFOXIDE
  name = G4_DIMETHYL_SULFOXIDE
  specific = 4
FEATURE [App::DocumentObjectGroupPython] C_element038  label="C_element : 022"  # scripted group (container) (typed FeaturePython)
  n = 2
  ref = C_element
FEATURE [App::DocumentObjectGroupPython] H_element035  label="H_element : 018"  # scripted group (container) (typed FeaturePython)
  n = 6
  ref = H_element
FEATURE [App::DocumentObjectGroupPython] G4_ETHANE  # scripted group (container) (typed FeaturePython)
  Dunit = g/cm3
  Dvalue = 0.00125324
  Group = -> [C_element038,H_element035]
  conduct = 2
  density = 1
  expand = 3
  formula = G4_ETHANE
  name = G4_ETHANE
  specific = 4
FEATURE [App::DocumentObjectGroupPython] C_element039  label="C_element : 023"  # scripted group (container) (typed FeaturePython)
  n = 2
  ref = C_element
FEATURE [App::DocumentObjectGroupPython] H_element036  label="H_element : 019"  # scripted group (container) (typed FeaturePython)
  n = 6
  ref = H_element
FEATURE [App::DocumentObjectGroupPython] O_element035  label="O_element : 018"  # scripted group (container) (typed FeaturePython)
  n = 1
  ref = O_element
FEATURE [App::DocumentObjectGroupPython] G4_ETHYL_ALCOHOL  # scripted group (container) (typed FeaturePython)
  Dunit = g/cm3
  Dvalue = 0.7893
  Group = -> [C_element039,H_element036,O_element035]
  conduct = 2
  density = 1
  expand = 3
  formula = G4_ETHYL_ALCOHOL
  name = G4_ETHYL_ALCOHOL
  specific = 4
FEATURE [App::DocumentObjectGroupPython] H_element037  label="H_element : 0.090"  # scripted group (container) (typed FeaturePython)
  n = 0.090027
FEATURE [App::DocumentObjectGroupPython] C_element040  label="C_element : 0.585"  # scripted group (container) (typed FeaturePython)
  n = 0.585182
FEATURE [App::DocumentObjectGroupPython] O_element036  label="O_element : 0.325"  # scripted group (container) (typed FeaturePython)
  n = 0.324791
FEATURE [App::DocumentObjectGroupPython] G4_ETHYL_CELLULOSE  # scripted group (container) (typed FeaturePython)
  Dunit = g/cm3
  Dvalue = 1.13
  Group = -> [H_element037,C_element040,O_element036]
  conduct = 2
  density = 1
  expand = 3
  formula = G4_ETHYL_CELLULOSE
  name = G4_ETHYL_CELLULOSE
  specific = 4
FEATURE [App::DocumentObjectGroupPython] C_element041  label="C_element : 024"  # scripted group (container) (typed FeaturePython)
  n = 2
  ref = C_element
FEATURE [App::DocumentObjectGroupPython] H_element038  label="H_element : 020"  # scripted group (container) (typed FeaturePython)
  n = 4
  ref = H_element
FEATURE [App::DocumentObjectGroupPython] G4_ETHYLENE  # scripted group (container) (typed FeaturePython)
  Dunit = g/cm3
  Dvalue = 0.00117497
  Group = -> [C_element041,H_element038]
  conduct = 2
  density = 1
  expand = 3
  formula = G4_ETHYLENE
  name = G4_ETHYLENE
  specific = 4
FEATURE [App::DocumentObjectGroupPython] H_element039  label="H_element : 0.096"  # scripted group (container) (typed FeaturePython)
  n = 0.096
FEATURE [App::DocumentObjectGroupPython] C_element042  label="C_element : 0.195"  # scripted group (container) (typed FeaturePython)
  n = 0.195
FEATURE [App::DocumentObjectGroupPython] N_element016  label="N_element : 0.057"  # scripted group (container) (typed FeaturePython)
  n = 0.057
FEATURE [App::DocumentObjectGroupPython] O_element037  label="O_element : 0.646"  # scripted group (container) (typed FeaturePython)
  n = 0.646
FEATURE [App::DocumentObjectGroupPython] Na_element006  label="Na_element : 0.017"  # scripted group (container) (typed FeaturePython)
  n = 0.001
FEATURE [App::DocumentObjectGroupPython] P_element005  label="P_element : 0.104"  # scripted group (container) (typed FeaturePython)
  n = 0.001
FEATURE [App::DocumentObjectGroupPython] S_element010  label="S_element : 0.016"  # scripted group (container) (typed FeaturePython)
  n = 0.003
FEATURE [App::DocumentObjectGroupPython] Cl_element010  label="Cl_element : 0.005"  # scripted group (container) (typed FeaturePython)
  n = 0.001
FEATURE [App::DocumentObjectGroupPython] G4_EYE_LENS_ICRP  # scripted group (container) (typed FeaturePython)
  Dunit = g/cm3
  Dvalue = 1.07
  Group = -> [H_element039,C_element042,N_element016,O_element037,Na_element006,P_element005,S_element010,Cl_element010]
  conduct = 2
  density = 1
  expand = 3
  formula = G4_EYE_LENS_ICRP
  name = G4_EYE_LENS_ICRP
  specific = 4
FEATURE [App::DocumentObjectGroupPython] Fe_element003  label="Fe_element : 2"  # scripted group (container) (typed FeaturePython)
  n = 2
  ref = Fe_element
FEATURE [App::DocumentObjectGroupPython] O_element038  label="O_element : 019"  # scripted group (container) (typed FeaturePython)
  n = 3
  ref = O_element
FEATURE [App::DocumentObjectGroupPython] G4_FERRIC_OXIDE  # scripted group (container) (typed FeaturePython)
  Dunit = g/cm3
  Dvalue = 5.2
  Group = -> [Fe_element003,O_element038]
  conduct = 2
  density = 1
  expand = 3
  formula = G4_FERRIC_OXIDE
  name = G4_FERRIC_OXIDE
  specific = 4
FEATURE [App::DocumentObjectGroupPython] Fe_element004  label="Fe_element : 1"  # scripted group (container) (typed FeaturePython)
  n = 1
  ref = Fe_element
FEATURE [App::DocumentObjectGroupPython] B_element003  label="B_element : 1"  # scripted group (container) (typed FeaturePython)
  n = 1
  ref = B_element
FEATURE [App::DocumentObjectGroupPython] G4_FERROBORIDE  # scripted group (container) (typed FeaturePython)
  Dunit = g/cm3
  Dvalue = 7.15
  Group = -> [Fe_element004,B_element003]
  conduct = 2
  density = 1
  expand = 3
  formula = G4_FERROBORIDE
  name = G4_FERROBORIDE
  specific = 4
FEATURE [App::DocumentObjectGroupPython] Fe_element005  label="Fe_element : 003"  # scripted group (container) (typed FeaturePython)
  n = 1
  ref = Fe_element
FEATURE [App::DocumentObjectGroupPython] O_element039  label="O_element : 020"  # scripted group (container) (typed FeaturePython)
  n = 1
  ref = O_element
FEATURE [App::DocumentObjectGroupPython] G4_FERROUS_OXIDE  # scripted group (container) (typed FeaturePython)
  Dunit = g/cm3
  Dvalue = 5.7
  Group = -> [Fe_element005,O_element039]
  conduct = 2
  density = 1
  expand = 3
  formula = G4_FERROUS_OXIDE
  name = G4_FERROUS_OXIDE
  specific = 4
FEATURE [App::DocumentObjectGroupPython] H_element040  label="H_element : 0.115"  # scripted group (container) (typed FeaturePython)
  n = 0.108259
FEATURE [App::DocumentObjectGroupPython] N_element017  label="N_element : 0.000"  # scripted group (container) (typed FeaturePython)
  n = 2.7e-05
FEATURE [App::DocumentObjectGroupPython] O_element040  label="O_element : 0.879"  # scripted group (container) (typed FeaturePython)
  n = 0.878636
FEATURE [App::DocumentObjectGroupPython] Na_element007  label="Na_element : 0.000"  # scripted group (container) (typed FeaturePython)
  n = 2.2e-05
FEATURE [App::DocumentObjectGroupPython] S_element011  label="S_element : 0.013"  # scripted group (container) (typed FeaturePython)
  n = 0.012968
FEATURE [App::DocumentObjectGroupPython] Cl_element011  label="Cl_element : 0.000"  # scripted group (container) (typed FeaturePython)
  n = 3.4e-05
FEATURE [App::DocumentObjectGroupPython] Fe_element006  label="Fe_element : 0.000"  # scripted group (container) (typed FeaturePython)
  n = 5.4e-05
FEATURE [App::DocumentObjectGroupPython] G4_FERROUS_SULFATE  # scripted group (container) (typed FeaturePython)
  Dunit = g/cm3
  Dvalue = 1.024
  Group = -> [H_element040,N_element017,O_element040,Na_element007,S_element011,Cl_element011,Fe_element006]
  conduct = 2
  density = 1
  expand = 3
  formula = G4_FERROUS_SULFATE
  name = G4_FERROUS_SULFATE
  specific = 4
FEATURE [App::DocumentObjectGroupPython] C_element043  label="C_element : 0.099"  # scripted group (container) (typed FeaturePython)
  n = 0.099335
FEATURE [App::DocumentObjectGroupPython] F_element007  label="F_element : 0.314"  # scripted group (container) (typed FeaturePython)
  n = 0.314247
FEATURE [App::DocumentObjectGroupPython] Cl_element012  label="Cl_element : 0.586"  # scripted group (container) (typed FeaturePython)
  n = 0.586418
FEATURE [App::DocumentObjectGroupPython] G4_FREON_12  label="G4_FREON-12"  # scripted group (container) (typed FeaturePython)
  Dunit = g/cm3
  Dvalue = 1.12
  Group = -> [C_element043,F_element007,Cl_element012]
  conduct = 2
  density = 1
  expand = 3
  formula = G4_FREON-12
  name = G4_FREON-12
  specific = 4
FEATURE [App::DocumentObjectGroupPython] C_element044  label="C_element : 0.057"  # scripted group (container) (typed FeaturePython)
  n = 0.057245
FEATURE [App::DocumentObjectGroupPython] F_element008  label="F_element : 0.181"  # scripted group (container) (typed FeaturePython)
  n = 0.181096
FEATURE [App::DocumentObjectGroupPython] Br_element001  label="Br_element : 0.762"  # scripted group (container) (typed FeaturePython)
  n = 0.761659
FEATURE [App::DocumentObjectGroupPython] G4_FREON_12B2  label="G4_FREON-12B2"  # scripted group (container) (typed FeaturePython)
  Dunit = g/cm3
  Dvalue = 1.8
  Group = -> [C_element044,F_element008,Br_element001]
  conduct = 2
  density = 1
  expand = 3
  formula = G4_FREON-12B2
  name = G4_FREON-12B2
  specific = 4
FEATURE [App::DocumentObjectGroupPython] C_element045  label="C_element : 0.115"  # scripted group (container) (typed FeaturePython)
  n = 0.114983
FEATURE [App::DocumentObjectGroupPython] F_element009  label="F_element : 0.546"  # scripted group (container) (typed FeaturePython)
  n = 0.545621
FEATURE [App::DocumentObjectGroupPython] Cl_element013  label="Cl_element : 0.339"  # scripted group (container) (typed FeaturePython)
  n = 0.339396
FEATURE [App::DocumentObjectGroupPython] G4_FREON_13  label="G4_FREON-13"  # scripted group (container) (typed FeaturePython)
  Dunit = g/cm3
  Dvalue = 0.95
  Group = -> [C_element045,F_element009,Cl_element013]
  conduct = 2
  density = 1
  expand = 3
  formula = G4_FREON-13
  name = G4_FREON-13
  specific = 4
FEATURE [App::DocumentObjectGroupPython] C_element046  label="C_element : 025"  # scripted group (container) (typed FeaturePython)
  n = 1
  ref = C_element
FEATURE [App::DocumentObjectGroupPython] F_element010  label="F_element : 3"  # scripted group (container) (typed FeaturePython)
  n = 3
  ref = F_element
FEATURE [App::DocumentObjectGroupPython] Br_element002  label="Br_element : 1"  # scripted group (container) (typed FeaturePython)
  n = 1
  ref = Br_element
FEATURE [App::DocumentObjectGroupPython] G4_FREON_13B1  label="G4_FREON-13B1"  # scripted group (container) (typed FeaturePython)
  Dunit = g/cm3
  Dvalue = 1.5
  Group = -> [C_element046,F_element010,Br_element002]
  conduct = 2
  density = 1
  expand = 3
  formula = G4_FREON-13B1
  name = G4_FREON-13B1
  specific = 4
FEATURE [App::DocumentObjectGroupPython] C_element047  label="C_element : 0.061"  # scripted group (container) (typed FeaturePython)
  n = 0.061309
FEATURE [App::DocumentObjectGroupPython] F_element011  label="F_element : 0.291"  # scripted group (container) (typed FeaturePython)
  n = 0.290924
FEATURE [App::DocumentObjectGroupPython] I_element002  label="I_element : 0.648"  # scripted group (container) (typed FeaturePython)
  n = 0.647767
FEATURE [App::DocumentObjectGroupPython] G4_FREON_13I1  label="G4_FREON-13I1"  # scripted group (container) (typed FeaturePython)
  Dunit = g/cm3
  Dvalue = 1.8
  Group = -> [C_element047,F_element011,I_element002]
  conduct = 2
  density = 1
  expand = 3
  formula = G4_FREON-13I1
  name = G4_FREON-13I1
  specific = 4
FEATURE [App::DocumentObjectGroupPython] Gd_element001  label="Gd_element : 2"  # scripted group (container) (typed FeaturePython)
  n = 2
  ref = Gd_element
FEATURE [App::DocumentObjectGroupPython] O_element041  label="O_element : 021"  # scripted group (container) (typed FeaturePython)
  n = 2
  ref = O_element
FEATURE [App::DocumentObjectGroupPython] S_element012  label="S_element : 004"  # scripted group (container) (typed FeaturePython)
  n = 1
  ref = S_element
FEATURE [App::DocumentObjectGroupPython] G4_GADOLINIUM_OXYSULFIDE  # scripted group (container) (typed FeaturePython)
  Dunit = g/cm3
  Dvalue = 7.44
  Group = -> [Gd_element001,O_element041,S_element012]
  conduct = 2
  density = 1
  expand = 3
  formula = G4_GADOLINIUM_OXYSULFIDE
  name = G4_GADOLINIUM_OXYSULFIDE
  specific = 4
FEATURE [App::DocumentObjectGroupPython] Ga_element001  label="Ga_element : 1"  # scripted group (container) (typed FeaturePython)
  n = 1
  ref = Ga_element
FEATURE [App::DocumentObjectGroupPython] As_element001  label="As_element : 1"  # scripted group (container) (typed FeaturePython)
  n = 1
  ref = As_element
FEATURE [App::DocumentObjectGroupPython] G4_GALLIUM_ARSENIDE  # scripted group (container) (typed FeaturePython)
  Dunit = g/cm3
  Dvalue = 5.31
  Group = -> [Ga_element001,As_element001]
  conduct = 2
  density = 1
  expand = 3
  formula = G4_GALLIUM_ARSENIDE
  name = G4_GALLIUM_ARSENIDE
  specific = 4
FEATURE [App::DocumentObjectGroupPython] H_element041  label="H_element : 0.081"  # scripted group (container) (typed FeaturePython)
  n = 0.08118
FEATURE [App::DocumentObjectGroupPython] C_element048  label="C_element : 0.416"  # scripted group (container) (typed FeaturePython)
  n = 0.41606
FEATURE [App::DocumentObjectGroupPython] N_element018  label="N_element : 0.111"  # scripted group (container) (typed FeaturePython)
  n = 0.11124
FEATURE [App::DocumentObjectGroupPython] O_element042  label="O_element : 0.381"  # scripted group (container) (typed FeaturePython)
  n = 0.38064
FEATURE [App::DocumentObjectGroupPython] S_element013  label="S_element : 0.011"  # scripted group (container) (typed FeaturePython)
  n = 0.01088
FEATURE [App::DocumentObjectGroupPython] G4_GEL_PHOTO_EMULSION  # scripted group (container) (typed FeaturePython)
  Dunit = g/cm3
  Dvalue = 1.2914
  Group = -> [H_element041,C_element048,N_element018,O_element042,S_element013]
  conduct = 2
  density = 1
  expand = 3
  formula = G4_GEL_PHOTO_EMULSION
  name = G4_GEL_PHOTO_EMULSION
  specific = 4
FEATURE [App::DocumentObjectGroupPython] B_element004  label="B_element : 0.040"  # scripted group (container) (typed FeaturePython)
  n = 0.0400639
FEATURE [App::DocumentObjectGroupPython] O_element043  label="O_element : 0.540"  # scripted group (container) (typed FeaturePython)
  n = 0.539561
FEATURE [App::DocumentObjectGroupPython] Na_element008  label="Na_element : 0.028"  # scripted group (container) (typed FeaturePython)
  n = 0.0281909
FEATURE [App::DocumentObjectGroupPython] Al_element003  label="Al_element : 0.012"  # scripted group (container) (typed FeaturePython)
  n = 0.011644
FEATURE [App::DocumentObjectGroupPython] Si_element003  label="Si_element : 0.377"  # scripted group (container) (typed FeaturePython)
  n = 0.377219
FEATURE [App::DocumentObjectGroupPython] K_element004  label="K_element : 0.014"  # scripted group (container) (typed FeaturePython)
  n = 0.00332099
FEATURE [App::DocumentObjectGroupPython] G4_Pyrex_Glass  # scripted group (container) (typed FeaturePython)
  Dunit = g/cm3
  Dvalue = 2.23
  Group = -> [B_element004,O_element043,Na_element008,Al_element003,Si_element003,K_element004]
  conduct = 2
  density = 1
  expand = 3
  formula = G4_Pyrex_Glass
  name = G4_Pyrex_Glass
  specific = 4
FEATURE [App::DocumentObjectGroupPython] O_element044  label="O_element : 0.156"  # scripted group (container) (typed FeaturePython)
  n = 0.156453
FEATURE [App::DocumentObjectGroupPython] Si_element004  label="Si_element : 0.081"  # scripted group (container) (typed FeaturePython)
  n = 0.080866
FEATURE [App::DocumentObjectGroupPython] Ti_element001  label="Ti_element : 0.008"  # scripted group (container) (typed FeaturePython)
  n = 0.008092
FEATURE [App::DocumentObjectGroupPython] As_element002  label="As_element : 0.003"  # scripted group (container) (typed FeaturePython)
  n = 0.002651
FEATURE [App::DocumentObjectGroupPython] Pb_element001  label="Pb_element : 0.752"  # scripted group (container) (typed FeaturePython)
  n = 0.751938
FEATURE [App::DocumentObjectGroupPython] G4_GLASS_LEAD  # scripted group (container) (typed FeaturePython)
  Dunit = g/cm3
  Dvalue = 6.22
  Group = -> [O_element044,Si_element004,Ti_element001,As_element002,Pb_element001]
  conduct = 2
  density = 1
  expand = 3
  formula = G4_GLASS_LEAD
  name = G4_GLASS_LEAD
  specific = 4
FEATURE [App::DocumentObjectGroupPython] O_element045  label="O_element : 0.460"  # scripted group (container) (typed FeaturePython)
  n = 0.4598
FEATURE [App::DocumentObjectGroupPython] Na_element009  label="Na_element : 0.096"  # scripted group (container) (typed FeaturePython)
  n = 0.0964411
FEATURE [App::DocumentObjectGroupPython] Si_element005  label="Si_element : 0.378"  # scripted group (container) (typed FeaturePython)
  n = 0.336553
FEATURE [App::DocumentObjectGroupPython] Ca_element011  label="Ca_element : 0.107"  # scripted group (container) (typed FeaturePython)
  n = 0.107205
FEATURE [App::DocumentObjectGroupPython] G4_GLASS_PLATE  # scripted group (container) (typed FeaturePython)
  Dunit = g/cm3
  Dvalue = 2.4
  Group = -> [O_element045,Na_element009,Si_element005,Ca_element011]
  conduct = 2
  density = 1
  expand = 3
  formula = G4_GLASS_PLATE
  name = G4_GLASS_PLATE
  specific = 4
FEATURE [App::DocumentObjectGroupPython] C_element049  label="C_element : 026"  # scripted group (container) (typed FeaturePython)
  n = 5
  ref = C_element
FEATURE [App::DocumentObjectGroupPython] H_element042  label="H_element : 021"  # scripted group (container) (typed FeaturePython)
  n = 10
  ref = H_element
FEATURE [App::DocumentObjectGroupPython] N_element019  label="N_element : 2"  # scripted group (container) (typed FeaturePython)
  n = 2
  ref = N_element
FEATURE [App::DocumentObjectGroupPython] O_element046  label="O_element : 022"  # scripted group (container) (typed FeaturePython)
  n = 3
  ref = O_element
FEATURE [App::DocumentObjectGroupPython] G4_GLUTAMINE  # scripted group (container) (typed FeaturePython)
  Dunit = g/cm3
  Dvalue = 1.46
  Group = -> [C_element049,H_element042,N_element019,O_element046]
  conduct = 2
  density = 1
  expand = 3
  formula = G4_GLUTAMINE
  name = G4_GLUTAMINE
  specific = 4
FEATURE [App::DocumentObjectGroupPython] C_element050  label="C_element : 027"  # scripted group (container) (typed FeaturePython)
  n = 3
  ref = C_element
FEATURE [App::DocumentObjectGroupPython] H_element043  label="H_element : 022"  # scripted group (container) (typed FeaturePython)
  n = 8
  ref = H_element
FEATURE [App::DocumentObjectGroupPython] O_element047  label="O_element : 023"  # scripted group (container) (typed FeaturePython)
  n = 3
  ref = O_element
FEATURE [App::DocumentObjectGroupPython] G4_GLYCEROL  # scripted group (container) (typed FeaturePython)
  Dunit = g/cm3
  Dvalue = 1.2613
  Group = -> [C_element050,H_element043,O_element047]
  conduct = 2
  density = 1
  expand = 3
  formula = G4_GLYCEROL
  name = G4_GLYCEROL
  specific = 4
FEATURE [App::DocumentObjectGroupPython] C_element051  label="C_element : 028"  # scripted group (container) (typed FeaturePython)
  n = 5
  ref = C_element
FEATURE [App::DocumentObjectGroupPython] H_element044  label="H_element : 023"  # scripted group (container) (typed FeaturePython)
  n = 5
  ref = H_element
FEATURE [App::DocumentObjectGroupPython] N_element020  label="N_element : 009"  # scripted group (container) (typed FeaturePython)
  n = 5
  ref = N_element
FEATURE [App::DocumentObjectGroupPython] O_element048  label="O_element : 024"  # scripted group (container) (typed FeaturePython)
  n = 1
  ref = O_element
FEATURE [App::DocumentObjectGroupPython] G4_GUANINE  # scripted group (container) (typed FeaturePython)
  Dunit = g/cm3
  Dvalue = 2.2
  Group = -> [C_element051,H_element044,N_element020,O_element048]
  conduct = 2
  density = 1
  expand = 3
  formula = G4_GUANINE
  name = G4_GUANINE
  specific = 4
FEATURE [App::DocumentObjectGroupPython] Ca_element012  label="Ca_element : 006"  # scripted group (container) (typed FeaturePython)
  n = 1
  ref = Ca_element
FEATURE [App::DocumentObjectGroupPython] S_element014  label="S_element : 005"  # scripted group (container) (typed FeaturePython)
  n = 1
  ref = S_element
FEATURE [App::DocumentObjectGroupPython] O_element049  label="O_element : 6"  # scripted group (container) (typed FeaturePython)
  n = 6
  ref = O_element
FEATURE [App::DocumentObjectGroupPython] H_element045  label="H_element : 024"  # scripted group (container) (typed FeaturePython)
  n = 4
  ref = H_element
FEATURE [App::DocumentObjectGroupPython] G4_GYPSUM  # scripted group (container) (typed FeaturePython)
  Dunit = g/cm3
  Dvalue = 2.32
  Group = -> [Ca_element012,S_element014,O_element049,H_element045]
  conduct = 2
  density = 1
  expand = 3
  formula = G4_GYPSUM
  name = G4_GYPSUM
  specific = 4
FEATURE [App::DocumentObjectGroupPython] C_element052  label="C_element : 7"  # scripted group (container) (typed FeaturePython)
  n = 7
  ref = C_element
FEATURE [App::DocumentObjectGroupPython] H_element046  label="H_element : 16"  # scripted group (container) (typed FeaturePython)
  n = 16
  ref = H_element
FEATURE [App::DocumentObjectGroupPython] G4_N_HEPTANE  label="G4_N-HEPTANE"  # scripted group (container) (typed FeaturePython)
  Dunit = g/cm3
  Dvalue = 0.68376
  Group = -> [C_element052,H_element046]
  conduct = 2
  density = 1
  expand = 3
  formula = G4_N-HEPTANE
  name = G4_N-HEPTANE
  specific = 4
FEATURE [App::DocumentObjectGroupPython] C_element053  label="C_element : 029"  # scripted group (container) (typed FeaturePython)
  n = 6
  ref = C_element
FEATURE [App::DocumentObjectGroupPython] H_element047  label="H_element : 14"  # scripted group (container) (typed FeaturePython)
  n = 14
  ref = H_element
FEATURE [App::DocumentObjectGroupPython] G4_N_HEXANE  label="G4_N-HEXANE"  # scripted group (container) (typed FeaturePython)
  Dunit = g/cm3
  Dvalue = 0.6603
  Group = -> [C_element053,H_element047]
  conduct = 2
  density = 1
  expand = 3
  formula = G4_N-HEXANE
  name = G4_N-HEXANE
  specific = 4
FEATURE [App::DocumentObjectGroupPython] C_element054  label="C_element : 22"  # scripted group (container) (typed FeaturePython)
  n = 22
  ref = C_element
FEATURE [App::DocumentObjectGroupPython] H_element048  label="H_element : 025"  # scripted group (container) (typed FeaturePython)
  n = 10
  ref = H_element
FEATURE [App::DocumentObjectGroupPython] N_element021  label="N_element : 010"  # scripted group (container) (typed FeaturePython)
  n = 2
  ref = N_element
FEATURE [App::DocumentObjectGroupPython] O_element050  label="O_element : 025"  # scripted group (container) (typed FeaturePython)
  n = 5
  ref = O_element
FEATURE [App::DocumentObjectGroupPython] G4_KAPTON  # scripted group (container) (typed FeaturePython)
  Dunit = g/cm3
  Dvalue = 1.42
  Group = -> [C_element054,H_element048,N_element021,O_element050]
  conduct = 2
  density = 1
  expand = 3
  formula = G4_KAPTON
  name = G4_KAPTON
  specific = 4
FEATURE [App::DocumentObjectGroupPython] La_element001  label="La_element : 1"  # scripted group (container) (typed FeaturePython)
  n = 1
  ref = La_element
FEATURE [App::DocumentObjectGroupPython] Br_element003  label="Br_element : 002"  # scripted group (container) (typed FeaturePython)
  n = 1
  ref = Br_element
FEATURE [App::DocumentObjectGroupPython] O_element051  label="O_element : 026"  # scripted group (container) (typed FeaturePython)
  n = 1
  ref = O_element
FEATURE [App::DocumentObjectGroupPython] G4_LANTHANUM_OXYBROMIDE  # scripted group (container) (typed FeaturePython)
  Dunit = g/cm3
  Dvalue = 6.28
  Group = -> [La_element001,Br_element003,O_element051]
  conduct = 2
  density = 1
  expand = 3
  formula = G4_LANTHANUM_OXYBROMIDE
  name = G4_LANTHANUM_OXYBROMIDE
  specific = 4
FEATURE [App::DocumentObjectGroupPython] La_element002  label="La_element : 2"  # scripted group (container) (typed FeaturePython)
  n = 2
  ref = La_element
FEATURE [App::DocumentObjectGroupPython] O_element052  label="O_element : 027"  # scripted group (container) (typed FeaturePython)
  n = 2
  ref = O_element
FEATURE [App::DocumentObjectGroupPython] S_element015  label="S_element : 006"  # scripted group (container) (typed FeaturePython)
  n = 1
  ref = S_element
FEATURE [App::DocumentObjectGroupPython] G4_LANTHANUM_OXYSULFIDE  # scripted group (container) (typed FeaturePython)
  Dunit = g/cm3
  Dvalue = 5.86
  Group = -> [La_element002,O_element052,S_element015]
  conduct = 2
  density = 1
  expand = 3
  formula = G4_LANTHANUM_OXYSULFIDE
  name = G4_LANTHANUM_OXYSULFIDE
  specific = 4
FEATURE [App::DocumentObjectGroupPython] O_element053  label="O_element : 0.072"  # scripted group (container) (typed FeaturePython)
  n = 0.071682
FEATURE [App::DocumentObjectGroupPython] Pb_element002  label="Pb_element : 0.928"  # scripted group (container) (typed FeaturePython)
  n = 0.928318
FEATURE [App::DocumentObjectGroupPython] G4_LEAD_OXIDE  # scripted group (container) (typed FeaturePython)
  Dunit = g/cm3
  Dvalue = 9.53
  Group = -> [O_element053,Pb_element002]
  conduct = 2
  density = 1
  expand = 3
  formula = G4_LEAD_OXIDE
  name = G4_LEAD_OXIDE
  specific = 4
FEATURE [App::DocumentObjectGroupPython] Li_element001  label="Li_element : 1"  # scripted group (container) (typed FeaturePython)
  n = 1
  ref = Li_element
FEATURE [App::DocumentObjectGroupPython] N_element022  label="N_element : 011"  # scripted group (container) (typed FeaturePython)
  n = 1
  ref = N_element
FEATURE [App::DocumentObjectGroupPython] H_element049  label="H_element : 026"  # scripted group (container) (typed FeaturePython)
  n = 2
  ref = H_element
FEATURE [App::DocumentObjectGroupPython] G4_LITHIUM_AMIDE  # scripted group (container) (typed FeaturePython)
  Dunit = g/cm3
  Dvalue = 1.178
  Group = -> [Li_element001,N_element022,H_element049]
  conduct = 2
  density = 1
  expand = 3
  formula = G4_LITHIUM_AMIDE
  name = G4_LITHIUM_AMIDE
  specific = 4
FEATURE [App::DocumentObjectGroupPython] Li_element002  label="Li_element : 2"  # scripted group (container) (typed FeaturePython)
  n = 2
  ref = Li_element
FEATURE [App::DocumentObjectGroupPython] C_element055  label="C_element : 030"  # scripted group (container) (typed FeaturePython)
  n = 1
  ref = C_element
FEATURE [App::DocumentObjectGroupPython] O_element054  label="O_element : 028"  # scripted group (container) (typed FeaturePython)
  n = 3
  ref = O_element
FEATURE [App::DocumentObjectGroupPython] G4_LITHIUM_CARBONATE  # scripted group (container) (typed FeaturePython)
  Dunit = g/cm3
  Dvalue = 2.11
  Group = -> [Li_element002,C_element055,O_element054]
  conduct = 2
  density = 1
  expand = 3
  formula = G4_LITHIUM_CARBONATE
  name = G4_LITHIUM_CARBONATE
  specific = 4
FEATURE [App::DocumentObjectGroupPython] Li_element003  label="Li_element : 003"  # scripted group (container) (typed FeaturePython)
  n = 1
  ref = Li_element
FEATURE [App::DocumentObjectGroupPython] F_element012  label="F_element : 004"  # scripted group (container) (typed FeaturePython)
  n = 1
  ref = F_element
FEATURE [App::DocumentObjectGroupPython] G4_LITHIUM_FLUORIDE  # scripted group (container) (typed FeaturePython)
  Dunit = g/cm3
  Dvalue = 2.635
  Group = -> [Li_element003,F_element012]
  conduct = 2
  density = 1
  expand = 3
  formula = G4_LITHIUM_FLUORIDE
  name = G4_LITHIUM_FLUORIDE
  specific = 4
FEATURE [App::DocumentObjectGroupPython] Li_element004  label="Li_element : 004"  # scripted group (container) (typed FeaturePython)
  n = 1
  ref = Li_element
FEATURE [App::DocumentObjectGroupPython] H_element050  label="H_element : 027"  # scripted group (container) (typed FeaturePython)
  n = 1
  ref = H_element
FEATURE [App::DocumentObjectGroupPython] G4_LITHIUM_HYDRIDE  # scripted group (container) (typed FeaturePython)
  Dunit = g/cm3
  Dvalue = 0.82
  Group = -> [Li_element004,H_element050]
  conduct = 2
  density = 1
  expand = 3
  formula = G4_LITHIUM_HYDRIDE
  name = G4_LITHIUM_HYDRIDE
  specific = 4
FEATURE [App::DocumentObjectGroupPython] Li_element005  label="Li_element : 005"  # scripted group (container) (typed FeaturePython)
  n = 1
  ref = Li_element
FEATURE [App::DocumentObjectGroupPython] I_element003  label="I_element : 002"  # scripted group (container) (typed FeaturePython)
  n = 1
  ref = I_element
FEATURE [App::DocumentObjectGroupPython] G4_LITHIUM_IODIDE  # scripted group (container) (typed FeaturePython)
  Dunit = g/cm3
  Dvalue = 3.494
  Group = -> [Li_element005,I_element003]
  conduct = 2
  density = 1
  expand = 3
  formula = G4_LITHIUM_IODIDE
  name = G4_LITHIUM_IODIDE
  specific = 4
FEATURE [App::DocumentObjectGroupPython] Li_element006  label="Li_element : 006"  # scripted group (container) (typed FeaturePython)
  n = 2
  ref = Li_element
FEATURE [App::DocumentObjectGroupPython] O_element055  label="O_element : 029"  # scripted group (container) (typed FeaturePython)
  n = 1
  ref = O_element
FEATURE [App::DocumentObjectGroupPython] G4_LITHIUM_OXIDE  # scripted group (container) (typed FeaturePython)
  Dunit = g/cm3
  Dvalue = 2.013
  Group = -> [Li_element006,O_element055]
  conduct = 2
  density = 1
  expand = 3
  formula = G4_LITHIUM_OXIDE
  name = G4_LITHIUM_OXIDE
  specific = 4
FEATURE [App::DocumentObjectGroupPython] Li_element007  label="Li_element : 007"  # scripted group (container) (typed FeaturePython)
  n = 2
  ref = Li_element
FEATURE [App::DocumentObjectGroupPython] B_element005  label="B_element : 005"  # scripted group (container) (typed FeaturePython)
  n = 4
  ref = B_element
FEATURE [App::DocumentObjectGroupPython] O_element056  label="O_element : 7"  # scripted group (container) (typed FeaturePython)
  n = 7
  ref = O_element
FEATURE [App::DocumentObjectGroupPython] G4_LITHIUM_TETRABORATE  # scripted group (container) (typed FeaturePython)
  Dunit = g/cm3
  Dvalue = 2.44
  Group = -> [Li_element007,B_element005,O_element056]
  conduct = 2
  density = 1
  expand = 3
  formula = G4_LITHIUM_TETRABORATE
  name = G4_LITHIUM_TETRABORATE
  specific = 4
FEATURE [App::DocumentObjectGroupPython] H_element051  label="H_element : 0.105"  # scripted group (container) (typed FeaturePython)
  n = 0.105
FEATURE [App::DocumentObjectGroupPython] C_element056  label="C_element : 0.083"  # scripted group (container) (typed FeaturePython)
  n = 0.083
FEATURE [App::DocumentObjectGroupPython] N_element023  label="N_element : 0.023"  # scripted group (container) (typed FeaturePython)
  n = 0.023
FEATURE [App::DocumentObjectGroupPython] O_element057  label="O_element : 0.779"  # scripted group (container) (typed FeaturePython)
  n = 0.779
FEATURE [App::DocumentObjectGroupPython] Na_element010  label="Na_element : 0.097"  # scripted group (container) (typed FeaturePython)
  n = 0.002
FEATURE [App::DocumentObjectGroupPython] P_element006  label="P_element : 0.105"  # scripted group (container) (typed FeaturePython)
  n = 0.001
FEATURE [App::DocumentObjectGroupPython] S_element016  label="S_element : 0.017"  # scripted group (container) (typed FeaturePython)
  n = 0.002
FEATURE [App::DocumentObjectGroupPython] Cl_element014  label="Cl_element : 0.587"  # scripted group (container) (typed FeaturePython)
  n = 0.003
FEATURE [App::DocumentObjectGroupPython] K_element005  label="K_element : 0.015"  # scripted group (container) (typed FeaturePython)
  n = 0.002
FEATURE [App::DocumentObjectGroupPython] G4_LUNG_ICRP  # scripted group (container) (typed FeaturePython)
  Dunit = g/cm3
  Dvalue = 1.04
  Group = -> [H_element051,C_element056,N_element023,O_element057,Na_element010,P_element006,S_element016,Cl_element014,K_element005]
  conduct = 2
  density = 1
  expand = 3
  formula = G4_LUNG_ICRP
  name = G4_LUNG_ICRP
  specific = 4
FEATURE [App::DocumentObjectGroupPython] H_element052  label="H_element : 0.116"  # scripted group (container) (typed FeaturePython)
  n = 0.114318
FEATURE [App::DocumentObjectGroupPython] C_element057  label="C_element : 0.656"  # scripted group (container) (typed FeaturePython)
  n = 0.655824
FEATURE [App::DocumentObjectGroupPython] O_element058  label="O_element : 0.092"  # scripted group (container) (typed FeaturePython)
  n = 0.0921831
FEATURE [App::DocumentObjectGroupPython] Mg_element004  label="Mg_element : 0.135"  # scripted group (container) (typed FeaturePython)
  n = 0.134792
FEATURE [App::DocumentObjectGroupPython] Ca_element013  label="Ca_element : 0.003"  # scripted group (container) (typed FeaturePython)
  n = 0.002883
FEATURE [App::DocumentObjectGroupPython] G4_M3_WAX  # scripted group (container) (typed FeaturePython)
  Dunit = g/cm3
  Dvalue = 1.05
  Group = -> [H_element052,C_element057,O_element058,Mg_element004,Ca_element013]
  conduct = 2
  density = 1
  expand = 3
  formula = G4_M3_WAX
  name = G4_M3_WAX
  specific = 4
FEATURE [App::DocumentObjectGroupPython] Mg_element005  label="Mg_element : 1"  # scripted group (container) (typed FeaturePython)
  n = 1
  ref = Mg_element
FEATURE [App::DocumentObjectGroupPython] C_element058  label="C_element : 031"  # scripted group (container) (typed FeaturePython)
  n = 1
  ref = C_element
FEATURE [App::DocumentObjectGroupPython] O_element059  label="O_element : 030"  # scripted group (container) (typed FeaturePython)
  n = 3
  ref = O_element
FEATURE [App::DocumentObjectGroupPython] G4_MAGNESIUM_CARBONATE  # scripted group (container) (typed FeaturePython)
  Dunit = g/cm3
  Dvalue = 2.958
  Group = -> [Mg_element005,C_element058,O_element059]
  conduct = 2
  density = 1
  expand = 3
  formula = G4_MAGNESIUM_CARBONATE
  name = G4_MAGNESIUM_CARBONATE
  specific = 4
FEATURE [App::DocumentObjectGroupPython] Mg_element006  label="Mg_element : 002"  # scripted group (container) (typed FeaturePython)
  n = 1
  ref = Mg_element
FEATURE [App::DocumentObjectGroupPython] F_element013  label="F_element : 005"  # scripted group (container) (typed FeaturePython)
  n = 2
  ref = F_element
FEATURE [App::DocumentObjectGroupPython] G4_MAGNESIUM_FLUORIDE  # scripted group (container) (typed FeaturePython)
  Dunit = g/cm3
  Dvalue = 3
  Group = -> [Mg_element006,F_element013]
  conduct = 2
  density = 1
  expand = 3
  formula = G4_MAGNESIUM_FLUORIDE
  name = G4_MAGNESIUM_FLUORIDE
  specific = 4
FEATURE [App::DocumentObjectGroupPython] Mg_element007  label="Mg_element : 003"  # scripted group (container) (typed FeaturePython)
  n = 1
  ref = Mg_element
FEATURE [App::DocumentObjectGroupPython] O_element060  label="O_element : 031"  # scripted group (container) (typed FeaturePython)
  n = 1
  ref = O_element
FEATURE [App::DocumentObjectGroupPython] G4_MAGNESIUM_OXIDE  # scripted group (container) (typed FeaturePython)
  Dunit = g/cm3
  Dvalue = 3.58
  Group = -> [Mg_element007,O_element060]
  conduct = 2
  density = 1
  expand = 3
  formula = G4_MAGNESIUM_OXIDE
  name = G4_MAGNESIUM_OXIDE
  specific = 4
FEATURE [App::DocumentObjectGroupPython] Mg_element008  label="Mg_element : 004"  # scripted group (container) (typed FeaturePython)
  n = 1
  ref = Mg_element
FEATURE [App::DocumentObjectGroupPython] B_element006  label="B_element : 006"  # scripted group (container) (typed FeaturePython)
  n = 4
  ref = B_element
FEATURE [App::DocumentObjectGroupPython] O_element061  label="O_element : 032"  # scripted group (container) (typed FeaturePython)
  n = 7
  ref = O_element
FEATURE [App::DocumentObjectGroupPython] G4_MAGNESIUM_TETRABORATE  # scripted group (container) (typed FeaturePython)
  Dunit = g/cm3
  Dvalue = 2.53
  Group = -> [Mg_element008,B_element006,O_element061]
  conduct = 2
  density = 1
  expand = 3
  formula = G4_MAGNESIUM_TETRABORATE
  name = G4_MAGNESIUM_TETRABORATE
  specific = 4
FEATURE [App::DocumentObjectGroupPython] Hg_element001  label="Hg_element : 1"  # scripted group (container) (typed FeaturePython)
  n = 1
  ref = Hg_element
FEATURE [App::DocumentObjectGroupPython] I_element004  label="I_element : 2"  # scripted group (container) (typed FeaturePython)
  n = 2
  ref = I_element
FEATURE [App::DocumentObjectGroupPython] G4_MERCURIC_IODIDE  # scripted group (container) (typed FeaturePython)
  Dunit = g/cm3
  Dvalue = 6.36
  Group = -> [Hg_element001,I_element004]
  conduct = 2
  density = 1
  expand = 3
  formula = G4_MERCURIC_IODIDE
  name = G4_MERCURIC_IODIDE
  specific = 4
FEATURE [App::DocumentObjectGroupPython] C_element059  label="C_element : 032"  # scripted group (container) (typed FeaturePython)
  n = 1
  ref = C_element
FEATURE [App::DocumentObjectGroupPython] H_element053  label="H_element : 028"  # scripted group (container) (typed FeaturePython)
  n = 4
  ref = H_element
FEATURE [App::DocumentObjectGroupPython] G4_METHANE  # scripted group (container) (typed FeaturePython)
  Dunit = g/cm3
  Dvalue = 0.000667151
  Group = -> [C_element059,H_element053]
  conduct = 2
  density = 1
  expand = 3
  formula = G4_METHANE
  name = G4_METHANE
  specific = 4
FEATURE [App::DocumentObjectGroupPython] C_element060  label="C_element : 033"  # scripted group (container) (typed FeaturePython)
  n = 1
  ref = C_element
FEATURE [App::DocumentObjectGroupPython] H_element054  label="H_element : 029"  # scripted group (container) (typed FeaturePython)
  n = 4
  ref = H_element
FEATURE [App::DocumentObjectGroupPython] O_element062  label="O_element : 033"  # scripted group (container) (typed FeaturePython)
  n = 1
  ref = O_element
FEATURE [App::DocumentObjectGroupPython] G4_METHANOL  # scripted group (container) (typed FeaturePython)
  Dunit = g/cm3
  Dvalue = 0.7914
  Group = -> [C_element060,H_element054,O_element062]
  conduct = 2
  density = 1
  expand = 3
  formula = G4_METHANOL
  name = G4_METHANOL
  specific = 4
FEATURE [App::DocumentObjectGroupPython] H_element055  label="H_element : 0.134"  # scripted group (container) (typed FeaturePython)
  n = 0.13404
FEATURE [App::DocumentObjectGroupPython] C_element061  label="C_element : 0.778"  # scripted group (container) (typed FeaturePython)
  n = 0.77796
FEATURE [App::DocumentObjectGroupPython] O_element063  label="O_element : 0.035"  # scripted group (container) (typed FeaturePython)
  n = 0.03502
FEATURE [App::DocumentObjectGroupPython] Mg_element009  label="Mg_element : 0.039"  # scripted group (container) (typed FeaturePython)
  n = 0.038594
FEATURE [App::DocumentObjectGroupPython] Ti_element002  label="Ti_element : 0.014"  # scripted group (container) (typed FeaturePython)
  n = 0.014386
FEATURE [App::DocumentObjectGroupPython] G4_MIX_D_WAX  # scripted group (container) (typed FeaturePython)
  Dunit = g/cm3
  Dvalue = 0.99
  Group = -> [H_element055,C_element061,O_element063,Mg_element009,Ti_element002]
  conduct = 2
  density = 1
  expand = 3
  formula = G4_MIX_D_WAX
  name = G4_MIX_D_WAX
  specific = 4
FEATURE [App::DocumentObjectGroupPython] H_element056  label="H_element : 0.135"  # scripted group (container) (typed FeaturePython)
  n = 0.081192
FEATURE [App::DocumentObjectGroupPython] C_element062  label="C_element : 0.583"  # scripted group (container) (typed FeaturePython)
  n = 0.583442
FEATURE [App::DocumentObjectGroupPython] N_element024  label="N_element : 0.018"  # scripted group (container) (typed FeaturePython)
  n = 0.017798
FEATURE [App::DocumentObjectGroupPython] O_element064  label="O_element : 0.186"  # scripted group (container) (typed FeaturePython)
  n = 0.186381
FEATURE [App::DocumentObjectGroupPython] Mg_element010  label="Mg_element : 0.130"  # scripted group (container) (typed FeaturePython)
  n = 0.130287
FEATURE [App::DocumentObjectGroupPython] Cl_element015  label="Cl_element : 0.588"  # scripted group (container) (typed FeaturePython)
  n = 0.0009
FEATURE [App::DocumentObjectGroupPython] G4_MS20_TISSUE  # scripted group (container) (typed FeaturePython)
  Dunit = g/cm3
  Dvalue = 1
  Group = -> [H_element056,C_element062,N_element024,O_element064,Mg_element010,Cl_element015]
  conduct = 2
  density = 1
  expand = 3
  formula = G4_MS20_TISSUE
  name = G4_MS20_TISSUE
  specific = 4
FEATURE [App::DocumentObjectGroupPython] H_element057  label="H_element : 0.136"  # scripted group (container) (typed FeaturePython)
  n = 0.102
FEATURE [App::DocumentObjectGroupPython] C_element063  label="C_element : 0.143"  # scripted group (container) (typed FeaturePython)
  n = 0.143
FEATURE [App::DocumentObjectGroupPython] N_element025  label="N_element : 0.034"  # scripted group (container) (typed FeaturePython)
  n = 0.034
FEATURE [App::DocumentObjectGroupPython] O_element065  label="O_element : 0.710"  # scripted group (container) (typed FeaturePython)
  n = 0.71
FEATURE [App::DocumentObjectGroupPython] Na_element011  label="Na_element : 0.098"  # scripted group (container) (typed FeaturePython)
  n = 0.001
FEATURE [App::DocumentObjectGroupPython] P_element007  label="P_element : 0.002"  # scripted group (container) (typed FeaturePython)
  n = 0.002
FEATURE [App::DocumentObjectGroupPython] S_element017  label="S_element : 0.018"  # scripted group (container) (typed FeaturePython)
  n = 0.003
FEATURE [App::DocumentObjectGroupPython] Cl_element016  label="Cl_element : 0.589"  # scripted group (container) (typed FeaturePython)
  n = 0.001
FEATURE [App::DocumentObjectGroupPython] K_element006  label="K_element : 0.004"  # scripted group (container) (typed FeaturePython)
  n = 0.004
FEATURE [App::DocumentObjectGroupPython] G4_MUSCLE_SKELETAL_ICRP  # scripted group (container) (typed FeaturePython)
  Dunit = g/cm3
  Dvalue = 1.05
  Group = -> [H_element057,C_element063,N_element025,O_element065,Na_element011,P_element007,S_element017,Cl_element016,K_element006]
  conduct = 2
  density = 1
  expand = 3
  formula = G4_MUSCLE_SKELETAL_ICRP
  name = G4_MUSCLE_SKELETAL_ICRP
  specific = 4
FEATURE [App::DocumentObjectGroupPython] H_element058  label="H_element : 0.137"  # scripted group (container) (typed FeaturePython)
  n = 0.102102
FEATURE [App::DocumentObjectGroupPython] C_element064  label="C_element : 0.123"  # scripted group (container) (typed FeaturePython)
  n = 0.123123
FEATURE [App::DocumentObjectGroupPython] N_element026  label="N_element : 0.756"  # scripted group (container) (typed FeaturePython)
  n = 0.035035
FEATURE [App::DocumentObjectGroupPython] O_element066  label="O_element : 0.730"  # scripted group (container) (typed FeaturePython)
  n = 0.72973
FEATURE [App::DocumentObjectGroupPython] Na_element012  label="Na_element : 0.099"  # scripted group (container) (typed FeaturePython)
  n = 0.001001
FEATURE [App::DocumentObjectGroupPython] P_element008  label="P_element : 0.106"  # scripted group (container) (typed FeaturePython)
  n = 0.002002
FEATURE [App::DocumentObjectGroupPython] S_element018  label="S_element : 0.019"  # scripted group (container) (typed FeaturePython)
  n = 0.004004
FEATURE [App::DocumentObjectGroupPython] K_element007  label="K_element : 0.016"  # scripted group (container) (typed FeaturePython)
  n = 0.003003
FEATURE [App::DocumentObjectGroupPython] G4_MUSCLE_STRIATED_ICRU  # scripted group (container) (typed FeaturePython)
  Dunit = g/cm3
  Dvalue = 1.04
  Group = -> [H_element058,C_element064,N_element026,O_element066,Na_element012,P_element008,S_element018,K_element007]
  conduct = 2
  density = 1
  expand = 3
  formula = G4_MUSCLE_STRIATED_ICRU
  name = G4_MUSCLE_STRIATED_ICRU
  specific = 4
FEATURE [App::DocumentObjectGroupPython] H_element059  label="H_element : 0.098"  # scripted group (container) (typed FeaturePython)
  n = 0.0982341
FEATURE [App::DocumentObjectGroupPython] C_element065  label="C_element : 0.156"  # scripted group (container) (typed FeaturePython)
  n = 0.156214
FEATURE [App::DocumentObjectGroupPython] N_element027  label="N_element : 0.757"  # scripted group (container) (typed FeaturePython)
  n = 0.035451
FEATURE [App::DocumentObjectGroupPython] O_element067  label="O_element : 0.880"  # scripted group (container) (typed FeaturePython)
  n = 0.710101
FEATURE [App::DocumentObjectGroupPython] G4_MUSCLE_WITH_SUCROSE  # scripted group (container) (typed FeaturePython)
  Dunit = g/cm3
  Dvalue = 1.11
  Group = -> [H_element059,C_element065,N_element027,O_element067]
  conduct = 2
  density = 1
  expand = 3
  formula = G4_MUSCLE_WITH_SUCROSE
  name = G4_MUSCLE_WITH_SUCROSE
  specific = 4
FEATURE [App::DocumentObjectGroupPython] H_element060  label="H_element : 0.138"  # scripted group (container) (typed FeaturePython)
  n = 0.101969
FEATURE [App::DocumentObjectGroupPython] C_element066  label="C_element : 0.120"  # scripted group (container) (typed FeaturePython)
  n = 0.120058
FEATURE [App::DocumentObjectGroupPython] N_element028  label="N_element : 0.758"  # scripted group (container) (typed FeaturePython)
  n = 0.035451
FEATURE [App::DocumentObjectGroupPython] O_element068  label="O_element : 0.743"  # scripted group (container) (typed FeaturePython)
  n = 0.742522
FEATURE [App::DocumentObjectGroupPython] G4_MUSCLE_WITHOUT_SUCROSE  # scripted group (container) (typed FeaturePython)
  Dunit = g/cm3
  Dvalue = 1.07
  Group = -> [H_element060,C_element066,N_element028,O_element068]
  conduct = 2
  density = 1
  expand = 3
  formula = G4_MUSCLE_WITHOUT_SUCROSE
  name = G4_MUSCLE_WITHOUT_SUCROSE
  specific = 4
FEATURE [App::DocumentObjectGroupPython] C_element067  label="C_element : 10"  # scripted group (container) (typed FeaturePython)
  n = 10
  ref = C_element
FEATURE [App::DocumentObjectGroupPython] H_element061  label="H_element : 030"  # scripted group (container) (typed FeaturePython)
  n = 8
  ref = H_element
FEATURE [App::DocumentObjectGroupPython] G4_NAPHTHALENE  # scripted group (container) (typed FeaturePython)
  Dunit = g/cm3
  Dvalue = 1.145
  Group = -> [C_element067,H_element061]
  conduct = 2
  density = 1
  expand = 3
  formula = G4_NAPHTHALENE
  name = G4_NAPHTHALENE
  specific = 4
FEATURE [App::DocumentObjectGroupPython] C_element068  label="C_element : 034"  # scripted group (container) (typed FeaturePython)
  n = 6
  ref = C_element
FEATURE [App::DocumentObjectGroupPython] H_element062  label="H_element : 031"  # scripted group (container) (typed FeaturePython)
  n = 5
  ref = H_element
FEATURE [App::DocumentObjectGroupPython] N_element029  label="N_element : 012"  # scripted group (container) (typed FeaturePython)
  n = 1
  ref = N_element
FEATURE [App::DocumentObjectGroupPython] O_element069  label="O_element : 034"  # scripted group (container) (typed FeaturePython)
  n = 2
  ref = O_element
FEATURE [App::DocumentObjectGroupPython] G4_NITROBENZENE  # scripted group (container) (typed FeaturePython)
  Dunit = g/cm3
  Dvalue = 1.19867
  Group = -> [C_element068,H_element062,N_element029,O_element069]
  conduct = 2
  density = 1
  expand = 3
  formula = G4_NITROBENZENE
  name = G4_NITROBENZENE
  specific = 4
FEATURE [App::DocumentObjectGroupPython] N_element030  label="N_element : 013"  # scripted group (container) (typed FeaturePython)
  n = 2
  ref = N_element
FEATURE [App::DocumentObjectGroupPython] O_element070  label="O_element : 035"  # scripted group (container) (typed FeaturePython)
  n = 1
  ref = O_element
FEATURE [App::DocumentObjectGroupPython] G4_NITROUS_OXIDE  # scripted group (container) (typed FeaturePython)
  Dunit = g/cm3
  Dvalue = 0.00183094
  Group = -> [N_element030,O_element070]
  conduct = 2
  density = 1
  expand = 3
  formula = G4_NITROUS_OXIDE
  name = G4_NITROUS_OXIDE
  specific = 4
FEATURE [App::DocumentObjectGroupPython] H_element063  label="H_element : 0.104"  # scripted group (container) (typed FeaturePython)
  n = 0.103509
FEATURE [App::DocumentObjectGroupPython] C_element069  label="C_element : 0.648"  # scripted group (container) (typed FeaturePython)
  n = 0.648416
FEATURE [App::DocumentObjectGroupPython] N_element031  label="N_element : 0.100"  # scripted group (container) (typed FeaturePython)
  n = 0.0995361
FEATURE [App::DocumentObjectGroupPython] O_element071  label="O_element : 0.149"  # scripted group (container) (typed FeaturePython)
  n = 0.148539
FEATURE [App::DocumentObjectGroupPython] G4_NYLON_8062  label="G4_NYLON-8062"  # scripted group (container) (typed FeaturePython)
  Dunit = g/cm3
  Dvalue = 1.08
  Group = -> [H_element063,C_element069,N_element031,O_element071]
  conduct = 2
  density = 1
  expand = 3
  formula = G4_NYLON-8062
  name = G4_NYLON-8062
  specific = 4
FEATURE [App::DocumentObjectGroupPython] C_element070  label="C_element : 035"  # scripted group (container) (typed FeaturePython)
  n = 6
  ref = C_element
FEATURE [App::DocumentObjectGroupPython] H_element064  label="H_element : 11"  # scripted group (container) (typed FeaturePython)
  n = 11
  ref = H_element
FEATURE [App::DocumentObjectGroupPython] N_element032  label="N_element : 014"  # scripted group (container) (typed FeaturePython)
  n = 1
  ref = N_element
FEATURE [App::DocumentObjectGroupPython] O_element072  label="O_element : 036"  # scripted group (container) (typed FeaturePython)
  n = 1
  ref = O_element
FEATURE [App::DocumentObjectGroupPython] G4_NYLON_6_6  label="G4_NYLON-6-6"  # scripted group (container) (typed FeaturePython)
  Dunit = g/cm3
  Dvalue = 1.14
  Group = -> [C_element070,H_element064,N_element032,O_element072]
  conduct = 2
  density = 1
  expand = 3
  formula = G4_NYLON-6-6
  name = G4_NYLON-6-6
  specific = 4
FEATURE [App::DocumentObjectGroupPython] H_element065  label="H_element : 0.139"  # scripted group (container) (typed FeaturePython)
  n = 0.107062
FEATURE [App::DocumentObjectGroupPython] C_element071  label="C_element : 0.680"  # scripted group (container) (typed FeaturePython)
  n = 0.680449
FEATURE [App::DocumentObjectGroupPython] N_element033  label="N_element : 0.099"  # scripted group (container) (typed FeaturePython)
  n = 0.099189
FEATURE [App::DocumentObjectGroupPython] O_element073  label="O_element : 0.113"  # scripted group (container) (typed FeaturePython)
  n = 0.1133
FEATURE [App::DocumentObjectGroupPython] G4_NYLON_6_10  label="G4_NYLON-6-10"  # scripted group (container) (typed FeaturePython)
  Dunit = g/cm3
  Dvalue = 1.14
  Group = -> [H_element065,C_element071,N_element033,O_element073]
  conduct = 2
  density = 1
  expand = 3
  formula = G4_NYLON-6-10
  name = G4_NYLON-6-10
  specific = 4
FEATURE [App::DocumentObjectGroupPython] H_element066  label="H_element : 0.140"  # scripted group (container) (typed FeaturePython)
  n = 0.115476
FEATURE [App::DocumentObjectGroupPython] C_element072  label="C_element : 0.721"  # scripted group (container) (typed FeaturePython)
  n = 0.720818
FEATURE [App::DocumentObjectGroupPython] N_element034  label="N_element : 0.076"  # scripted group (container) (typed FeaturePython)
  n = 0.0764169
FEATURE [App::DocumentObjectGroupPython] O_element074  label="O_element : 0.087"  # scripted group (container) (typed FeaturePython)
  n = 0.0872889
FEATURE [App::DocumentObjectGroupPython] G4_NYLON_11_RILSAN  label="G4_NYLON-11_RILSAN"  # scripted group (container) (typed FeaturePython)
  Dunit = g/cm3
  Dvalue = 1.425
  Group = -> [H_element066,C_element072,N_element034,O_element074]
  conduct = 2
  density = 1
  expand = 3
  formula = G4_NYLON-11_RILSAN
  name = G4_NYLON-11_RILSAN
  specific = 4
FEATURE [App::DocumentObjectGroupPython] C_element073  label="C_element : 8"  # scripted group (container) (typed FeaturePython)
  n = 8
  ref = C_element
FEATURE [App::DocumentObjectGroupPython] H_element067  label="H_element : 18"  # scripted group (container) (typed FeaturePython)
  n = 18
  ref = H_element
FEATURE [App::DocumentObjectGroupPython] G4_OCTANE  # scripted group (container) (typed FeaturePython)
  Dunit = g/cm3
  Dvalue = 0.7026
  Group = -> [C_element073,H_element067]
  conduct = 2
  density = 1
  expand = 3
  formula = G4_OCTANE
  name = G4_OCTANE
  specific = 4
FEATURE [App::DocumentObjectGroupPython] C_element074  label="C_element : 25"  # scripted group (container) (typed FeaturePython)
  n = 25
  ref = C_element
FEATURE [App::DocumentObjectGroupPython] H_element068  label="H_element : 52"  # scripted group (container) (typed FeaturePython)
  n = 52
  ref = H_element
FEATURE [App::DocumentObjectGroupPython] G4_PARAFFIN  # scripted group (container) (typed FeaturePython)
  Dunit = g/cm3
  Dvalue = 0.93
  Group = -> [C_element074,H_element068]
  conduct = 2
  density = 1
  expand = 3
  formula = G4_PARAFFIN
  name = G4_PARAFFIN
  specific = 4
FEATURE [App::DocumentObjectGroupPython] C_element075  label="C_element : 036"  # scripted group (container) (typed FeaturePython)
  n = 5
  ref = C_element
FEATURE [App::DocumentObjectGroupPython] H_element069  label="H_element : 032"  # scripted group (container) (typed FeaturePython)
  n = 12
  ref = H_element
FEATURE [App::DocumentObjectGroupPython] G4_N_PENTANE  label="G4_N-PENTANE"  # scripted group (container) (typed FeaturePython)
  Dunit = g/cm3
  Dvalue = 0.6262
  Group = -> [C_element075,H_element069]
  conduct = 2
  density = 1
  expand = 3
  formula = G4_N-PENTANE
  name = G4_N-PENTANE
  specific = 4
FEATURE [App::DocumentObjectGroupPython] H_element070  label="H_element : 0.014"  # scripted group (container) (typed FeaturePython)
  n = 0.0141
FEATURE [App::DocumentObjectGroupPython] C_element076  label="C_element : 0.072"  # scripted group (container) (typed FeaturePython)
  n = 0.072261
FEATURE [App::DocumentObjectGroupPython] N_element035  label="N_element : 0.019"  # scripted group (container) (typed FeaturePython)
  n = 0.01932
FEATURE [App::DocumentObjectGroupPython] O_element075  label="O_element : 0.066"  # scripted group (container) (typed FeaturePython)
  n = 0.066101
FEATURE [App::DocumentObjectGroupPython] S_element019  label="S_element : 0.020"  # scripted group (container) (typed FeaturePython)
  n = 0.00189
FEATURE [App::DocumentObjectGroupPython] Br_element004  label="Br_element : 0.349"  # scripted group (container) (typed FeaturePython)
  n = 0.349103
FEATURE [App::DocumentObjectGroupPython] Ag_element001  label="Ag_element : 0.474"  # scripted group (container) (typed FeaturePython)
  n = 0.474105
FEATURE [App::DocumentObjectGroupPython] I_element005  label="I_element : 0.003"  # scripted group (container) (typed FeaturePython)
  n = 0.00312
FEATURE [App::DocumentObjectGroupPython] G4_PHOTO_EMULSION  # scripted group (container) (typed FeaturePython)
  Dunit = g/cm3
  Dvalue = 3.815
  Group = -> [H_element070,C_element076,N_element035,O_element075,S_element019,Br_element004,Ag_element001,I_element005]
  conduct = 2
  density = 1
  expand = 3
  formula = G4_PHOTO_EMULSION
  name = G4_PHOTO_EMULSION
  specific = 4
FEATURE [App::DocumentObjectGroupPython] C_element077  label="C_element : 9"  # scripted group (container) (typed FeaturePython)
  n = 9
  ref = C_element
FEATURE [App::DocumentObjectGroupPython] H_element071  label="H_element : 033"  # scripted group (container) (typed FeaturePython)
  n = 10
  ref = H_element
FEATURE [App::DocumentObjectGroupPython] G4_PLASTIC_SC_VINYLTOLUENE  # scripted group (container) (typed FeaturePython)
  Dunit = g/cm3
  Dvalue = 1.032
  Group = -> [C_element077,H_element071]
  conduct = 2
  density = 1
  expand = 3
  formula = G4_PLASTIC_SC_VINYLTOLUENE
  name = G4_PLASTIC_SC_VINYLTOLUENE
  specific = 4
FEATURE [App::DocumentObjectGroupPython] Pu_element001  label="Pu_element : 1"  # scripted group (container) (typed FeaturePython)
  n = 1
  ref = Pu_element
FEATURE [App::DocumentObjectGroupPython] O_element076  label="O_element : 037"  # scripted group (container) (typed FeaturePython)
  n = 2
  ref = O_element
FEATURE [App::DocumentObjectGroupPython] G4_PLUTONIUM_DIOXIDE  # scripted group (container) (typed FeaturePython)
  Dunit = g/cm3
  Dvalue = 11.46
  Group = -> [Pu_element001,O_element076]
  conduct = 2
  density = 1
  expand = 3
  formula = G4_PLUTONIUM_DIOXIDE
  name = G4_PLUTONIUM_DIOXIDE
  specific = 4
FEATURE [App::DocumentObjectGroupPython] C_element078  label="C_element : 037"  # scripted group (container) (typed FeaturePython)
  n = 3
  ref = C_element
FEATURE [App::DocumentObjectGroupPython] H_element072  label="H_element : 034"  # scripted group (container) (typed FeaturePython)
  n = 3
  ref = H_element
FEATURE [App::DocumentObjectGroupPython] N_element036  label="N_element : 015"  # scripted group (container) (typed FeaturePython)
  n = 1
  ref = N_element
FEATURE [App::DocumentObjectGroupPython] G4_POLYACRYLONITRILE  # scripted group (container) (typed FeaturePython)
  Dunit = g/cm3
  Dvalue = 1.17
  Group = -> [C_element078,H_element072,N_element036]
  conduct = 2
  density = 1
  expand = 3
  formula = G4_POLYACRYLONITRILE
  name = G4_POLYACRYLONITRILE
  specific = 4
FEATURE [App::DocumentObjectGroupPython] C_element079  label="C_element : 16"  # scripted group (container) (typed FeaturePython)
  n = 16
  ref = C_element
FEATURE [App::DocumentObjectGroupPython] H_element073  label="H_element : 035"  # scripted group (container) (typed FeaturePython)
  n = 14
  ref = H_element
FEATURE [App::DocumentObjectGroupPython] O_element077  label="O_element : 038"  # scripted group (container) (typed FeaturePython)
  n = 3
  ref = O_element
FEATURE [App::DocumentObjectGroupPython] G4_POLYCARBONATE  # scripted group (container) (typed FeaturePython)
  Dunit = g/cm3
  Dvalue = 1.2
  Group = -> [C_element079,H_element073,O_element077]
  conduct = 2
  density = 1
  expand = 3
  formula = G4_POLYCARBONATE
  name = G4_POLYCARBONATE
  specific = 4
FEATURE [App::DocumentObjectGroupPython] C_element080  label="C_element : 038"  # scripted group (container) (typed FeaturePython)
  n = 8
  ref = C_element
FEATURE [App::DocumentObjectGroupPython] H_element074  label="H_element : 036"  # scripted group (container) (typed FeaturePython)
  n = 7
  ref = H_element
FEATURE [App::DocumentObjectGroupPython] Cl_element017  label="Cl_element : 007"  # scripted group (container) (typed FeaturePython)
  n = 1
  ref = Cl_element
FEATURE [App::DocumentObjectGroupPython] G4_POLYCHLOROSTYRENE  # scripted group (container) (typed FeaturePython)
  Dunit = g/cm3
  Dvalue = 1.3
  Group = -> [C_element080,H_element074,Cl_element017]
  conduct = 2
  density = 1
  expand = 3
  formula = G4_POLYCHLOROSTYRENE
  name = G4_POLYCHLOROSTYRENE
  specific = 4
FEATURE [App::DocumentObjectGroupPython] C_element081  label="C_element : 039"  # scripted group (container) (typed FeaturePython)
  n = 1
  ref = C_element
FEATURE [App::DocumentObjectGroupPython] H_element075  label="H_element : 037"  # scripted group (container) (typed FeaturePython)
  n = 2
  ref = H_element
FEATURE [App::DocumentObjectGroupPython] G4_POLYETHYLENE  # scripted group (container) (typed FeaturePython)
  Dunit = g/cm3
  Dvalue = 0.94
  Group = -> [C_element081,H_element075]
  conduct = 2
  density = 1
  expand = 3
  formula = G4_POLYETHYLENE
  name = G4_POLYETHYLENE
  specific = 4
FEATURE [App::DocumentObjectGroupPython] C_element082  label="C_element : 040"  # scripted group (container) (typed FeaturePython)
  n = 10
  ref = C_element
FEATURE [App::DocumentObjectGroupPython] H_element076  label="H_element : 038"  # scripted group (container) (typed FeaturePython)
  n = 8
  ref = H_element
FEATURE [App::DocumentObjectGroupPython] O_element078  label="O_element : 039"  # scripted group (container) (typed FeaturePython)
  n = 4
  ref = O_element
FEATURE [App::DocumentObjectGroupPython] G4_MYLAR  # scripted group (container) (typed FeaturePython)
  Dunit = g/cm3
  Dvalue = 1.4
  Group = -> [C_element082,H_element076,O_element078]
  conduct = 2
  density = 1
  expand = 3
  formula = G4_MYLAR
  name = G4_MYLAR
  specific = 4
FEATURE [App::DocumentObjectGroupPython] C_element083  label="C_element : 041"  # scripted group (container) (typed FeaturePython)
  n = 5
  ref = C_element
FEATURE [App::DocumentObjectGroupPython] H_element077  label="H_element : 039"  # scripted group (container) (typed FeaturePython)
  n = 8
  ref = H_element
FEATURE [App::DocumentObjectGroupPython] O_element079  label="O_element : 040"  # scripted group (container) (typed FeaturePython)
  n = 2
  ref = O_element
FEATURE [App::DocumentObjectGroupPython] G4_PLEXIGLASS  # scripted group (container) (typed FeaturePython)
  Dunit = g/cm3
  Dvalue = 1.19
  Group = -> [C_element083,H_element077,O_element079]
  conduct = 2
  density = 1
  expand = 3
  formula = G4_PLEXIGLASS
  name = G4_PLEXIGLASS
  specific = 4
FEATURE [App::DocumentObjectGroupPython] C_element084  label="C_element : 042"  # scripted group (container) (typed FeaturePython)
  n = 1
  ref = C_element
FEATURE [App::DocumentObjectGroupPython] H_element078  label="H_element : 040"  # scripted group (container) (typed FeaturePython)
  n = 2
  ref = H_element
FEATURE [App::DocumentObjectGroupPython] O_element080  label="O_element : 041"  # scripted group (container) (typed FeaturePython)
  n = 1
  ref = O_element
FEATURE [App::DocumentObjectGroupPython] G4_POLYOXYMETHYLENE  # scripted group (container) (typed FeaturePython)
  Dunit = g/cm3
  Dvalue = 1.425
  Group = -> [C_element084,H_element078,O_element080]
  conduct = 2
  density = 1
  expand = 3
  formula = G4_POLYOXYMETHYLENE
  name = G4_POLYOXYMETHYLENE
  specific = 4
FEATURE [App::DocumentObjectGroupPython] C_element085  label="C_element : 043"  # scripted group (container) (typed FeaturePython)
  n = 2
  ref = C_element
FEATURE [App::DocumentObjectGroupPython] H_element079  label="H_element : 041"  # scripted group (container) (typed FeaturePython)
  n = 4
  ref = H_element
FEATURE [App::DocumentObjectGroupPython] G4_POLYPROPYLENE  # scripted group (container) (typed FeaturePython)
  Dunit = g/cm3
  Dvalue = 0.9
  Group = -> [C_element085,H_element079]
  conduct = 2
  density = 1
  expand = 3
  formula = G4_POLYPROPYLENE
  name = G4_POLYPROPYLENE
  specific = 4
FEATURE [App::DocumentObjectGroupPython] C_element086  label="C_element : 044"  # scripted group (container) (typed FeaturePython)
  n = 8
  ref = C_element
FEATURE [App::DocumentObjectGroupPython] H_element080  label="H_element : 042"  # scripted group (container) (typed FeaturePython)
  n = 8
  ref = H_element
FEATURE [App::DocumentObjectGroupPython] G4_POLYSTYRENE  # scripted group (container) (typed FeaturePython)
  Dunit = g/cm3
  Dvalue = 1.06
  Group = -> [C_element086,H_element080]
  conduct = 2
  density = 1
  expand = 3
  formula = G4_POLYSTYRENE
  name = G4_POLYSTYRENE
  specific = 4
FEATURE [App::DocumentObjectGroupPython] C_element087  label="C_element : 045"  # scripted group (container) (typed FeaturePython)
  n = 2
  ref = C_element
FEATURE [App::DocumentObjectGroupPython] F_element014  label="F_element : 4"  # scripted group (container) (typed FeaturePython)
  n = 4
  ref = F_element
FEATURE [App::DocumentObjectGroupPython] G4_TEFLON  # scripted group (container) (typed FeaturePython)
  Dunit = g/cm3
  Dvalue = 2.2
  Group = -> [C_element087,F_element014]
  conduct = 2
  density = 1
  expand = 3
  formula = G4_TEFLON
  name = G4_TEFLON
  specific = 4
FEATURE [App::DocumentObjectGroupPython] C_element088  label="C_element : 046"  # scripted group (container) (typed FeaturePython)
  n = 2
  ref = C_element
FEATURE [App::DocumentObjectGroupPython] F_element015  label="F_element : 006"  # scripted group (container) (typed FeaturePython)
  n = 3
  ref = F_element
FEATURE [App::DocumentObjectGroupPython] Cl_element018  label="Cl_element : 008"  # scripted group (container) (typed FeaturePython)
  n = 1
  ref = Cl_element
FEATURE [App::DocumentObjectGroupPython] G4_POLYTRIFLUOROCHLOROETHYLENE  # scripted group (container) (typed FeaturePython)
  Dunit = g/cm3
  Dvalue = 2.1
  Group = -> [C_element088,F_element015,Cl_element018]
  conduct = 2
  density = 1
  expand = 3
  formula = G4_POLYTRIFLUOROCHLOROETHYLENE
  name = G4_POLYTRIFLUOROCHLOROETHYLENE
  specific = 4
FEATURE [App::DocumentObjectGroupPython] C_element089  label="C_element : 047"  # scripted group (container) (typed FeaturePython)
  n = 4
  ref = C_element
FEATURE [App::DocumentObjectGroupPython] H_element081  label="H_element : 043"  # scripted group (container) (typed FeaturePython)
  n = 6
  ref = H_element
FEATURE [App::DocumentObjectGroupPython] O_element081  label="O_element : 042"  # scripted group (container) (typed FeaturePython)
  n = 2
  ref = O_element
FEATURE [App::DocumentObjectGroupPython] G4_POLYVINYL_ACETATE  # scripted group (container) (typed FeaturePython)
  Dunit = g/cm3
  Dvalue = 1.19
  Group = -> [C_element089,H_element081,O_element081]
  conduct = 2
  density = 1
  expand = 3
  formula = G4_POLYVINYL_ACETATE
  name = G4_POLYVINYL_ACETATE
  specific = 4
FEATURE [App::DocumentObjectGroupPython] C_element090  label="C_element : 048"  # scripted group (container) (typed FeaturePython)
  n = 2
  ref = C_element
FEATURE [App::DocumentObjectGroupPython] H_element082  label="H_element : 044"  # scripted group (container) (typed FeaturePython)
  n = 4
  ref = H_element
FEATURE [App::DocumentObjectGroupPython] O_element082  label="O_element : 043"  # scripted group (container) (typed FeaturePython)
  n = 1
  ref = O_element
FEATURE [App::DocumentObjectGroupPython] G4_POLYVINYL_ALCOHOL  # scripted group (container) (typed FeaturePython)
  Dunit = g/cm3
  Dvalue = 1.3
  Group = -> [C_element090,H_element082,O_element082]
  conduct = 2
  density = 1
  expand = 3
  formula = G4_POLYVINYL_ALCOHOL
  name = G4_POLYVINYL_ALCOHOL
  specific = 4
FEATURE [App::DocumentObjectGroupPython] C_element091  label="C_element : 049"  # scripted group (container) (typed FeaturePython)
  n = 8
  ref = C_element
FEATURE [App::DocumentObjectGroupPython] H_element083  label="H_element : 045"  # scripted group (container) (typed FeaturePython)
  n = 14
  ref = H_element
FEATURE [App::DocumentObjectGroupPython] O_element083  label="O_element : 044"  # scripted group (container) (typed FeaturePython)
  n = 2
  ref = O_element
FEATURE [App::DocumentObjectGroupPython] G4_POLYVINYL_BUTYRAL  # scripted group (container) (typed FeaturePython)
  Dunit = g/cm3
  Dvalue = 1.12
  Group = -> [C_element091,H_element083,O_element083]
  conduct = 2
  density = 1
  expand = 3
  formula = G4_POLYVINYL_BUTYRAL
  name = G4_POLYVINYL_BUTYRAL
  specific = 4
FEATURE [App::DocumentObjectGroupPython] C_element092  label="C_element : 050"  # scripted group (container) (typed FeaturePython)
  n = 2
  ref = C_element
FEATURE [App::DocumentObjectGroupPython] H_element084  label="H_element : 046"  # scripted group (container) (typed FeaturePython)
  n = 3
  ref = H_element
FEATURE [App::DocumentObjectGroupPython] Cl_element019  label="Cl_element : 009"  # scripted group (container) (typed FeaturePython)
  n = 1
  ref = Cl_element
FEATURE [App::DocumentObjectGroupPython] G4_POLYVINYL_CHLORIDE  # scripted group (container) (typed FeaturePython)
  Dunit = g/cm3
  Dvalue = 1.3
  Group = -> [C_element092,H_element084,Cl_element019]
  conduct = 2
  density = 1
  expand = 3
  formula = G4_POLYVINYL_CHLORIDE
  name = G4_POLYVINYL_CHLORIDE
  specific = 4
FEATURE [App::DocumentObjectGroupPython] C_element093  label="C_element : 051"  # scripted group (container) (typed FeaturePython)
  n = 2
  ref = C_element
FEATURE [App::DocumentObjectGroupPython] H_element085  label="H_element : 047"  # scripted group (container) (typed FeaturePython)
  n = 2
  ref = H_element
FEATURE [App::DocumentObjectGroupPython] Cl_element020  label="Cl_element : 010"  # scripted group (container) (typed FeaturePython)
  n = 2
  ref = Cl_element
FEATURE [App::DocumentObjectGroupPython] G4_POLYVINYLIDENE_CHLORIDE  # scripted group (container) (typed FeaturePython)
  Dunit = g/cm3
  Dvalue = 1.7
  Group = -> [C_element093,H_element085,Cl_element020]
  conduct = 2
  density = 1
  expand = 3
  formula = G4_POLYVINYLIDENE_CHLORIDE
  name = G4_POLYVINYLIDENE_CHLORIDE
  specific = 4
FEATURE [App::DocumentObjectGroupPython] C_element094  label="C_element : 052"  # scripted group (container) (typed FeaturePython)
  n = 2
  ref = C_element
FEATURE [App::DocumentObjectGroupPython] H_element086  label="H_element : 048"  # scripted group (container) (typed FeaturePython)
  n = 2
  ref = H_element
FEATURE [App::DocumentObjectGroupPython] F_element016  label="F_element : 007"  # scripted group (container) (typed FeaturePython)
  n = 2
  ref = F_element
FEATURE [App::DocumentObjectGroupPython] G4_POLYVINYLIDENE_FLUORIDE  # scripted group (container) (typed FeaturePython)
  Dunit = g/cm3
  Dvalue = 1.76
  Group = -> [C_element094,H_element086,F_element016]
  conduct = 2
  density = 1
  expand = 3
  formula = G4_POLYVINYLIDENE_FLUORIDE
  name = G4_POLYVINYLIDENE_FLUORIDE
  specific = 4
FEATURE [App::DocumentObjectGroupPython] C_element095  label="C_element : 053"  # scripted group (container) (typed FeaturePython)
  n = 6
  ref = C_element
FEATURE [App::DocumentObjectGroupPython] H_element087  label="H_element : 9"  # scripted group (container) (typed FeaturePython)
  n = 9
  ref = H_element
FEATURE [App::DocumentObjectGroupPython] N_element037  label="N_element : 016"  # scripted group (container) (typed FeaturePython)
  n = 1
  ref = N_element
FEATURE [App::DocumentObjectGroupPython] O_element084  label="O_element : 045"  # scripted group (container) (typed FeaturePython)
  n = 1
  ref = O_element
FEATURE [App::DocumentObjectGroupPython] G4_POLYVINYL_PYRROLIDONE  # scripted group (container) (typed FeaturePython)
  Dunit = g/cm3
  Dvalue = 1.25
  Group = -> [C_element095,H_element087,N_element037,O_element084]
  conduct = 2
  density = 1
  expand = 3
  formula = G4_POLYVINYL_PYRROLIDONE
  name = G4_POLYVINYL_PYRROLIDONE
  specific = 4
FEATURE [App::DocumentObjectGroupPython] K_element008  label="K_element : 1"  # scripted group (container) (typed FeaturePython)
  n = 1
  ref = K_element
FEATURE [App::DocumentObjectGroupPython] I_element006  label="I_element : 003"  # scripted group (container) (typed FeaturePython)
  n = 1
  ref = I_element
FEATURE [App::DocumentObjectGroupPython] G4_POTASSIUM_IODIDE  # scripted group (container) (typed FeaturePython)
  Dunit = g/cm3
  Dvalue = 3.13
  Group = -> [K_element008,I_element006]
  conduct = 2
  density = 1
  expand = 3
  formula = G4_POTASSIUM_IODIDE
  name = G4_POTASSIUM_IODIDE
  specific = 4
FEATURE [App::DocumentObjectGroupPython] K_element009  label="K_element : 2"  # scripted group (container) (typed FeaturePython)
  n = 2
  ref = K_element
FEATURE [App::DocumentObjectGroupPython] O_element085  label="O_element : 046"  # scripted group (container) (typed FeaturePython)
  n = 1
  ref = O_element
FEATURE [App::DocumentObjectGroupPython] G4_POTASSIUM_OXIDE  # scripted group (container) (typed FeaturePython)
  Dunit = g/cm3
  Dvalue = 2.32
  Group = -> [K_element009,O_element085]
  conduct = 2
  density = 1
  expand = 3
  formula = G4_POTASSIUM_OXIDE
  name = G4_POTASSIUM_OXIDE
  specific = 4
FEATURE [App::DocumentObjectGroupPython] C_element096  label="C_element : 054"  # scripted group (container) (typed FeaturePython)
  n = 3
  ref = C_element
FEATURE [App::DocumentObjectGroupPython] H_element088  label="H_element : 049"  # scripted group (container) (typed FeaturePython)
  n = 8
  ref = H_element
FEATURE [App::DocumentObjectGroupPython] G4_PROPANE  # scripted group (container) (typed FeaturePython)
  Dunit = g/cm3
  Dvalue = 0.00187939
  Group = -> [C_element096,H_element088]
  conduct = 2
  density = 1
  expand = 3
  formula = G4_PROPANE
  name = G4_PROPANE
  specific = 4
FEATURE [App::DocumentObjectGroupPython] C_element097  label="C_element : 055"  # scripted group (container) (typed FeaturePython)
  n = 3
  ref = C_element
FEATURE [App::DocumentObjectGroupPython] H_element089  label="H_element : 050"  # scripted group (container) (typed FeaturePython)
  n = 8
  ref = H_element
FEATURE [App::DocumentObjectGroupPython] G4_lPROPANE  # scripted group (container) (typed FeaturePython)
  Dunit = g/cm3
  Dvalue = 0.43
  Group = -> [C_element097,H_element089]
  conduct = 2
  density = 1
  expand = 3
  formula = G4_lPROPANE
  name = G4_lPROPANE
  specific = 4
FEATURE [App::DocumentObjectGroupPython] C_element098  label="C_element : 056"  # scripted group (container) (typed FeaturePython)
  n = 3
  ref = C_element
FEATURE [App::DocumentObjectGroupPython] H_element090  label="H_element : 051"  # scripted group (container) (typed FeaturePython)
  n = 8
  ref = H_element
FEATURE [App::DocumentObjectGroupPython] O_element086  label="O_element : 047"  # scripted group (container) (typed FeaturePython)
  n = 1
  ref = O_element
FEATURE [App::DocumentObjectGroupPython] G4_N_PROPYL_ALCOHOL  label="G4_N-PROPYL_ALCOHOL"  # scripted group (container) (typed FeaturePython)
  Dunit = g/cm3
  Dvalue = 0.8035
  Group = -> [C_element098,H_element090,O_element086]
  conduct = 2
  density = 1
  expand = 3
  formula = G4_N-PROPYL_ALCOHOL
  name = G4_N-PROPYL_ALCOHOL
  specific = 4
FEATURE [App::DocumentObjectGroupPython] C_element099  label="C_element : 057"  # scripted group (container) (typed FeaturePython)
  n = 5
  ref = C_element
FEATURE [App::DocumentObjectGroupPython] H_element091  label="H_element : 052"  # scripted group (container) (typed FeaturePython)
  n = 5
  ref = H_element
FEATURE [App::DocumentObjectGroupPython] N_element038  label="N_element : 017"  # scripted group (container) (typed FeaturePython)
  n = 1
  ref = N_element
FEATURE [App::DocumentObjectGroupPython] G4_PYRIDINE  # scripted group (container) (typed FeaturePython)
  Dunit = g/cm3
  Dvalue = 0.9819
  Group = -> [C_element099,H_element091,N_element038]
  conduct = 2
  density = 1
  expand = 3
  formula = G4_PYRIDINE
  name = G4_PYRIDINE
  specific = 4
FEATURE [App::DocumentObjectGroupPython] H_element092  label="H_element : 0.144"  # scripted group (container) (typed FeaturePython)
  n = 0.143711
FEATURE [App::DocumentObjectGroupPython] C_element100  label="C_element : 0.856"  # scripted group (container) (typed FeaturePython)
  n = 0.856289
FEATURE [App::DocumentObjectGroupPython] G4_RUBBER_BUTYL  # scripted group (container) (typed FeaturePython)
  Dunit = g/cm3
  Dvalue = 0.92
  Group = -> [H_element092,C_element100]
  conduct = 2
  density = 1
  expand = 3
  formula = G4_RUBBER_BUTYL
  name = G4_RUBBER_BUTYL
  specific = 4
FEATURE [App::DocumentObjectGroupPython] H_element093  label="H_element : 0.118"  # scripted group (container) (typed FeaturePython)
  n = 0.118371
FEATURE [App::DocumentObjectGroupPython] C_element101  label="C_element : 0.882"  # scripted group (container) (typed FeaturePython)
  n = 0.881629
FEATURE [App::DocumentObjectGroupPython] G4_RUBBER_NATURAL  # scripted group (container) (typed FeaturePython)
  Dunit = g/cm3
  Dvalue = 0.92
  Group = -> [H_element093,C_element101]
  conduct = 2
  density = 1
  expand = 3
  formula = G4_RUBBER_NATURAL
  name = G4_RUBBER_NATURAL
  specific = 4
FEATURE [App::DocumentObjectGroupPython] H_element094  label="H_element : 0.145"  # scripted group (container) (typed FeaturePython)
  n = 0.05692
FEATURE [App::DocumentObjectGroupPython] C_element102  label="C_element : 0.543"  # scripted group (container) (typed FeaturePython)
  n = 0.542646
FEATURE [App::DocumentObjectGroupPython] Cl_element021  label="Cl_element : 0.400"  # scripted group (container) (typed FeaturePython)
  n = 0.400434
FEATURE [App::DocumentObjectGroupPython] G4_RUBBER_NEOPRENE  # scripted group (container) (typed FeaturePython)
  Dunit = g/cm3
  Dvalue = 1.23
  Group = -> [H_element094,C_element102,Cl_element021]
  conduct = 2
  density = 1
  expand = 3
  formula = G4_RUBBER_NEOPRENE
  name = G4_RUBBER_NEOPRENE
  specific = 4
FEATURE [App::DocumentObjectGroupPython] Si_element006  label="Si_element : 1"  # scripted group (container) (typed FeaturePython)
  n = 1
  ref = Si_element
FEATURE [App::DocumentObjectGroupPython] O_element087  label="O_element : 048"  # scripted group (container) (typed FeaturePython)
  n = 2
  ref = O_element
FEATURE [App::DocumentObjectGroupPython] G4_SILICON_DIOXIDE001  label="G4_SILICON_DIOXIDE"  # scripted group (container) (typed FeaturePython)
  Dunit = g/cm3
  Dvalue = 2.32
  Group = -> [Si_element006,O_element087]
  conduct = 2
  density = 1
  expand = 3
  formula = G4_SILICON_DIOXIDE
  name = G4_SILICON_DIOXIDE
  specific = 4
FEATURE [App::DocumentObjectGroupPython] Ag_element002  label="Ag_element : 1"  # scripted group (container) (typed FeaturePython)
  n = 1
  ref = Ag_element
FEATURE [App::DocumentObjectGroupPython] Br_element005  label="Br_element : 003"  # scripted group (container) (typed FeaturePython)
  n = 1
  ref = Br_element
FEATURE [App::DocumentObjectGroupPython] G4_SILVER_BROMIDE  # scripted group (container) (typed FeaturePython)
  Dunit = g/cm3
  Dvalue = 6.473
  Group = -> [Ag_element002,Br_element005]
  conduct = 2
  density = 1
  expand = 3
  formula = G4_SILVER_BROMIDE
  name = G4_SILVER_BROMIDE
  specific = 4
FEATURE [App::DocumentObjectGroupPython] Ag_element003  label="Ag_element : 002"  # scripted group (container) (typed FeaturePython)
  n = 1
  ref = Ag_element
FEATURE [App::DocumentObjectGroupPython] Cl_element022  label="Cl_element : 011"  # scripted group (container) (typed FeaturePython)
  n = 1
  ref = Cl_element
FEATURE [App::DocumentObjectGroupPython] G4_SILVER_CHLORIDE  # scripted group (container) (typed FeaturePython)
  Dunit = g/cm3
  Dvalue = 5.56
  Group = -> [Ag_element003,Cl_element022]
  conduct = 2
  density = 1
  expand = 3
  formula = G4_SILVER_CHLORIDE
  name = G4_SILVER_CHLORIDE
  specific = 4
FEATURE [App::DocumentObjectGroupPython] Br_element006  label="Br_element : 0.423"  # scripted group (container) (typed FeaturePython)
  n = 0.422895
FEATURE [App::DocumentObjectGroupPython] Ag_element004  label="Ag_element : 0.574"  # scripted group (container) (typed FeaturePython)
  n = 0.573748
FEATURE [App::DocumentObjectGroupPython] I_element007  label="I_element : 0.649"  # scripted group (container) (typed FeaturePython)
  n = 0.003357
FEATURE [App::DocumentObjectGroupPython] G4_SILVER_HALIDES  # scripted group (container) (typed FeaturePython)
  Dunit = g/cm3
  Dvalue = 6.47
  Group = -> [Br_element006,Ag_element004,I_element007]
  conduct = 2
  density = 1
  expand = 3
  formula = G4_SILVER_HALIDES
  name = G4_SILVER_HALIDES
  specific = 4
FEATURE [App::DocumentObjectGroupPython] Ag_element005  label="Ag_element : 003"  # scripted group (container) (typed FeaturePython)
  n = 1
  ref = Ag_element
FEATURE [App::DocumentObjectGroupPython] I_element008  label="I_element : 004"  # scripted group (container) (typed FeaturePython)
  n = 1
  ref = I_element
FEATURE [App::DocumentObjectGroupPython] G4_SILVER_IODIDE  # scripted group (container) (typed FeaturePython)
  Dunit = g/cm3
  Dvalue = 6.01
  Group = -> [Ag_element005,I_element008]
  conduct = 2
  density = 1
  expand = 3
  formula = G4_SILVER_IODIDE
  name = G4_SILVER_IODIDE
  specific = 4
FEATURE [App::DocumentObjectGroupPython] H_element095  label="H_element : 0.100"  # scripted group (container) (typed FeaturePython)
  n = 0.1
FEATURE [App::DocumentObjectGroupPython] C_element103  label="C_element : 0.204"  # scripted group (container) (typed FeaturePython)
  n = 0.204
FEATURE [App::DocumentObjectGroupPython] N_element039  label="N_element : 0.759"  # scripted group (container) (typed FeaturePython)
  n = 0.042
FEATURE [App::DocumentObjectGroupPython] O_element088  label="O_element : 0.645"  # scripted group (container) (typed FeaturePython)
  n = 0.645
FEATURE [App::DocumentObjectGroupPython] Na_element013  label="Na_element : 0.100"  # scripted group (container) (typed FeaturePython)
  n = 0.002
FEATURE [App::DocumentObjectGroupPython] P_element009  label="P_element : 0.107"  # scripted group (container) (typed FeaturePython)
  n = 0.001
FEATURE [App::DocumentObjectGroupPython] S_element020  label="S_element : 0.021"  # scripted group (container) (typed FeaturePython)
  n = 0.002
FEATURE [App::DocumentObjectGroupPython] Cl_element023  label="Cl_element : 0.590"  # scripted group (container) (typed FeaturePython)
  n = 0.003
FEATURE [App::DocumentObjectGroupPython] K_element010  label="K_element : 0.001"  # scripted group (container) (typed FeaturePython)
  n = 0.001
FEATURE [App::DocumentObjectGroupPython] G4_SKIN_ICRP  # scripted group (container) (typed FeaturePython)
  Dunit = g/cm3
  Dvalue = 1.09
  Group = -> [H_element095,C_element103,N_element039,O_element088,Na_element013,P_element009,S_element020,Cl_element023,K_element010]
  conduct = 2
  density = 1
  expand = 3
  formula = G4_SKIN_ICRP
  name = G4_SKIN_ICRP
  specific = 4
FEATURE [App::DocumentObjectGroupPython] Na_element014  label="Na_element : 2"  # scripted group (container) (typed FeaturePython)
  n = 2
  ref = Na_element
FEATURE [App::DocumentObjectGroupPython] C_element104  label="C_element : 058"  # scripted group (container) (typed FeaturePython)
  n = 1
  ref = C_element
FEATURE [App::DocumentObjectGroupPython] O_element089  label="O_element : 049"  # scripted group (container) (typed FeaturePython)
  n = 3
  ref = O_element
FEATURE [App::DocumentObjectGroupPython] G4_SODIUM_CARBONATE  # scripted group (container) (typed FeaturePython)
  Dunit = g/cm3
  Dvalue = 2.532
  Group = -> [Na_element014,C_element104,O_element089]
  conduct = 2
  density = 1
  expand = 3
  formula = G4_SODIUM_CARBONATE
  name = G4_SODIUM_CARBONATE
  specific = 4
FEATURE [App::DocumentObjectGroupPython] Na_element015  label="Na_element : 1"  # scripted group (container) (typed FeaturePython)
  n = 1
  ref = Na_element
FEATURE [App::DocumentObjectGroupPython] I_element009  label="I_element : 005"  # scripted group (container) (typed FeaturePython)
  n = 1
  ref = I_element
FEATURE [App::DocumentObjectGroupPython] G4_SODIUM_IODIDE  # scripted group (container) (typed FeaturePython)
  Dunit = g/cm3
  Dvalue = 3.667
  Group = -> [Na_element015,I_element009]
  conduct = 2
  density = 1
  expand = 3
  formula = G4_SODIUM_IODIDE
  name = G4_SODIUM_IODIDE
  specific = 4
FEATURE [App::DocumentObjectGroupPython] Na_element016  label="Na_element : 003"  # scripted group (container) (typed FeaturePython)
  n = 2
  ref = Na_element
FEATURE [App::DocumentObjectGroupPython] O_element090  label="O_element : 050"  # scripted group (container) (typed FeaturePython)
  n = 1
  ref = O_element
FEATURE [App::DocumentObjectGroupPython] G4_SODIUM_MONOXIDE  # scripted group (container) (typed FeaturePython)
  Dunit = g/cm3
  Dvalue = 2.27
  Group = -> [Na_element016,O_element090]
  conduct = 2
  density = 1
  expand = 3
  formula = G4_SODIUM_MONOXIDE
  name = G4_SODIUM_MONOXIDE
  specific = 4
FEATURE [App::DocumentObjectGroupPython] Na_element017  label="Na_element : 004"  # scripted group (container) (typed FeaturePython)
  n = 1
  ref = Na_element
FEATURE [App::DocumentObjectGroupPython] N_element040  label="N_element : 018"  # scripted group (container) (typed FeaturePython)
  n = 1
  ref = N_element
FEATURE [App::DocumentObjectGroupPython] O_element091  label="O_element : 051"  # scripted group (container) (typed FeaturePython)
  n = 3
  ref = O_element
FEATURE [App::DocumentObjectGroupPython] G4_SODIUM_NITRATE  # scripted group (container) (typed FeaturePython)
  Dunit = g/cm3
  Dvalue = 2.261
  Group = -> [Na_element017,N_element040,O_element091]
  conduct = 2
  density = 1
  expand = 3
  formula = G4_SODIUM_NITRATE
  name = G4_SODIUM_NITRATE
  specific = 4
FEATURE [App::DocumentObjectGroupPython] C_element105  label="C_element : 059"  # scripted group (container) (typed FeaturePython)
  n = 14
  ref = C_element
FEATURE [App::DocumentObjectGroupPython] H_element096  label="H_element : 053"  # scripted group (container) (typed FeaturePython)
  n = 12
  ref = H_element
FEATURE [App::DocumentObjectGroupPython] G4_STILBENE  # scripted group (container) (typed FeaturePython)
  Dunit = g/cm3
  Dvalue = 0.9707
  Group = -> [C_element105,H_element096]
  conduct = 2
  density = 1
  expand = 3
  formula = G4_STILBENE
  name = G4_STILBENE
  specific = 4
FEATURE [App::DocumentObjectGroupPython] C_element106  label="C_element : 12"  # scripted group (container) (typed FeaturePython)
  n = 12
  ref = C_element
FEATURE [App::DocumentObjectGroupPython] H_element097  label="H_element : 22"  # scripted group (container) (typed FeaturePython)
  n = 22
  ref = H_element
FEATURE [App::DocumentObjectGroupPython] O_element092  label="O_element : 11"  # scripted group (container) (typed FeaturePython)
  n = 11
  ref = O_element
FEATURE [App::DocumentObjectGroupPython] G4_SUCROSE  # scripted group (container) (typed FeaturePython)
  Dunit = g/cm3
  Dvalue = 1.5805
  Group = -> [C_element106,H_element097,O_element092]
  conduct = 2
  density = 1
  expand = 3
  formula = G4_SUCROSE
  name = G4_SUCROSE
  specific = 4
FEATURE [App::DocumentObjectGroupPython] C_element107  label="C_element : 18"  # scripted group (container) (typed FeaturePython)
  n = 18
  ref = C_element
FEATURE [App::DocumentObjectGroupPython] H_element098  label="H_element : 054"  # scripted group (container) (typed FeaturePython)
  n = 14
  ref = H_element
FEATURE [App::DocumentObjectGroupPython] G4_TERPHENYL  # scripted group (container) (typed FeaturePython)
  Dunit = g/cm3
  Dvalue = 1.24
  Group = -> [C_element107,H_element098]
  conduct = 2
  density = 1
  expand = 3
  formula = G4_TERPHENYL
  name = G4_TERPHENYL
  specific = 4
FEATURE [App::DocumentObjectGroupPython] H_element099  label="H_element : 0.146"  # scripted group (container) (typed FeaturePython)
  n = 0.106
FEATURE [App::DocumentObjectGroupPython] C_element108  label="C_element : 0.883"  # scripted group (container) (typed FeaturePython)
  n = 0.099
FEATURE [App::DocumentObjectGroupPython] N_element041  label="N_element : 0.020"  # scripted group (container) (typed FeaturePython)
  n = 0.02
FEATURE [App::DocumentObjectGroupPython] O_element093  label="O_element : 0.766"  # scripted group (container) (typed FeaturePython)
  n = 0.766
FEATURE [App::DocumentObjectGroupPython] Na_element018  label="Na_element : 0.101"  # scripted group (container) (typed FeaturePython)
  n = 0.002
FEATURE [App::DocumentObjectGroupPython] P_element010  label="P_element : 0.108"  # scripted group (container) (typed FeaturePython)
  n = 0.001
FEATURE [App::DocumentObjectGroupPython] S_element021  label="S_element : 0.022"  # scripted group (container) (typed FeaturePython)
  n = 0.002
FEATURE [App::DocumentObjectGroupPython] Cl_element024  label="Cl_element : 0.002"  # scripted group (container) (typed FeaturePython)
  n = 0.002
FEATURE [App::DocumentObjectGroupPython] K_element011  label="K_element : 0.017"  # scripted group (container) (typed FeaturePython)
  n = 0.002
FEATURE [App::DocumentObjectGroupPython] G4_TESTIS_ICRP  # scripted group (container) (typed FeaturePython)
  Dunit = g/cm3
  Dvalue = 1.04
  Group = -> [H_element099,C_element108,N_element041,O_element093,Na_element018,P_element010,S_element021,Cl_element024,K_element011]
  conduct = 2
  density = 1
  expand = 3
  formula = G4_TESTIS_ICRP
  name = G4_TESTIS_ICRP
  specific = 4
FEATURE [App::DocumentObjectGroupPython] C_element109  label="C_element : 060"  # scripted group (container) (typed FeaturePython)
  n = 2
  ref = C_element
FEATURE [App::DocumentObjectGroupPython] Cl_element025  label="Cl_element : 012"  # scripted group (container) (typed FeaturePython)
  n = 4
  ref = Cl_element
FEATURE [App::DocumentObjectGroupPython] G4_TETRACHLOROETHYLENE  # scripted group (container) (typed FeaturePython)
  Dunit = g/cm3
  Dvalue = 1.625
  Group = -> [C_element109,Cl_element025]
  conduct = 2
  density = 1
  expand = 3
  formula = G4_TETRACHLOROETHYLENE
  name = G4_TETRACHLOROETHYLENE
  specific = 4
FEATURE [App::DocumentObjectGroupPython] Tl_element001  label="Tl_element : 1"  # scripted group (container) (typed FeaturePython)
  n = 1
  ref = Tl_element
FEATURE [App::DocumentObjectGroupPython] Cl_element026  label="Cl_element : 013"  # scripted group (container) (typed FeaturePython)
  n = 1
  ref = Cl_element
FEATURE [App::DocumentObjectGroupPython] G4_THALLIUM_CHLORIDE  # scripted group (container) (typed FeaturePython)
  Dunit = g/cm3
  Dvalue = 7.004
  Group = -> [Tl_element001,Cl_element026]
  conduct = 2
  density = 1
  expand = 3
  formula = G4_THALLIUM_CHLORIDE
  name = G4_THALLIUM_CHLORIDE
  specific = 4
FEATURE [App::DocumentObjectGroupPython] H_element100  label="H_element : 0.147"  # scripted group (container) (typed FeaturePython)
  n = 0.105
FEATURE [App::DocumentObjectGroupPython] C_element110  label="C_element : 0.256"  # scripted group (container) (typed FeaturePython)
  n = 0.256
FEATURE [App::DocumentObjectGroupPython] N_element042  label="N_element : 0.760"  # scripted group (container) (typed FeaturePython)
  n = 0.027
FEATURE [App::DocumentObjectGroupPython] O_element094  label="O_element : 0.602"  # scripted group (container) (typed FeaturePython)
  n = 0.602
FEATURE [App::DocumentObjectGroupPython] Na_element019  label="Na_element : 0.102"  # scripted group (container) (typed FeaturePython)
  n = 0.001
FEATURE [App::DocumentObjectGroupPython] P_element011  label="P_element : 0.109"  # scripted group (container) (typed FeaturePython)
  n = 0.002
FEATURE [App::DocumentObjectGroupPython] S_element022  label="S_element : 0.023"  # scripted group (container) (typed FeaturePython)
  n = 0.003
FEATURE [App::DocumentObjectGroupPython] Cl_element027  label="Cl_element : 0.591"  # scripted group (container) (typed FeaturePython)
  n = 0.002
FEATURE [App::DocumentObjectGroupPython] K_element012  label="K_element : 0.018"  # scripted group (container) (typed FeaturePython)
  n = 0.002
FEATURE [App::DocumentObjectGroupPython] G4_TISSUE_SOFT_ICRP  # scripted group (container) (typed FeaturePython)
  Dunit = g/cm3
  Dvalue = 1.03
  Group = -> [H_element100,C_element110,N_element042,O_element094,Na_element019,P_element011,S_element022,Cl_element027,K_element012]
  conduct = 2
  density = 1
  expand = 3
  formula = G4_TISSUE_SOFT_ICRP
  name = G4_TISSUE_SOFT_ICRP
  specific = 4
FEATURE [App::DocumentObjectGroupPython] H_element101  label="H_element : 0.148"  # scripted group (container) (typed FeaturePython)
  n = 0.101
FEATURE [App::DocumentObjectGroupPython] C_element111  label="C_element : 0.111"  # scripted group (container) (typed FeaturePython)
  n = 0.111
FEATURE [App::DocumentObjectGroupPython] N_element043  label="N_element : 0.026"  # scripted group (container) (typed FeaturePython)
  n = 0.026
FEATURE [App::DocumentObjectGroupPython] O_element095  label="O_element : 0.762"  # scripted group (container) (typed FeaturePython)
  n = 0.762
FEATURE [App::DocumentObjectGroupPython] G4_TISSUE_SOFT_ICRU_4  label="G4_TISSUE_SOFT_ICRU-4"  # scripted group (container) (typed FeaturePython)
  Dunit = g/cm3
  Dvalue = 1
  Group = -> [H_element101,C_element111,N_element043,O_element095]
  conduct = 2
  density = 1
  expand = 3
  formula = G4_TISSUE_SOFT_ICRU-4
  name = G4_TISSUE_SOFT_ICRU-4
  specific = 4
FEATURE [App::DocumentObjectGroupPython] H_element102  label="H_element : 0.149"  # scripted group (container) (typed FeaturePython)
  n = 0.101869
FEATURE [App::DocumentObjectGroupPython] C_element112  label="C_element : 0.456"  # scripted group (container) (typed FeaturePython)
  n = 0.456179
FEATURE [App::DocumentObjectGroupPython] N_element044  label="N_element : 0.761"  # scripted group (container) (typed FeaturePython)
  n = 0.035172
FEATURE [App::DocumentObjectGroupPython] O_element096  label="O_element : 0.407"  # scripted group (container) (typed FeaturePython)
  n = 0.40678
FEATURE [App::DocumentObjectGroupPython] G4_TISSUE_METHANE  label="G4_TISSUE-METHANE"  # scripted group (container) (typed FeaturePython)
  Dunit = g/cm3
  Dvalue = 0.00106409
  Group = -> [H_element102,C_element112,N_element044,O_element096]
  conduct = 2
  density = 1
  expand = 3
  formula = G4_TISSUE-METHANE
  name = G4_TISSUE-METHANE
  specific = 4
FEATURE [App::DocumentObjectGroupPython] H_element103  label="H_element : 0.103"  # scripted group (container) (typed FeaturePython)
  n = 0.102672
FEATURE [App::DocumentObjectGroupPython] C_element113  label="C_element : 0.569"  # scripted group (container) (typed FeaturePython)
  n = 0.56894
FEATURE [App::DocumentObjectGroupPython] N_element045  label="N_element : 0.762"  # scripted group (container) (typed FeaturePython)
  n = 0.035022
FEATURE [App::DocumentObjectGroupPython] O_element097  label="O_element : 0.293"  # scripted group (container) (typed FeaturePython)
  n = 0.293366
FEATURE [App::DocumentObjectGroupPython] G4_TISSUE_PROPANE  label="G4_TISSUE-PROPANE"  # scripted group (container) (typed FeaturePython)
  Dunit = g/cm3
  Dvalue = 0.00182628
  Group = -> [H_element103,C_element113,N_element045,O_element097]
  conduct = 2
  density = 1
  expand = 3
  formula = G4_TISSUE-PROPANE
  name = G4_TISSUE-PROPANE
  specific = 4
FEATURE [App::DocumentObjectGroupPython] Ti_element003  label="Ti_element : 1"  # scripted group (container) (typed FeaturePython)
  n = 1
  ref = Ti_element
FEATURE [App::DocumentObjectGroupPython] O_element098  label="O_element : 052"  # scripted group (container) (typed FeaturePython)
  n = 2
  ref = O_element
FEATURE [App::DocumentObjectGroupPython] G4_TITANIUM_DIOXIDE  # scripted group (container) (typed FeaturePython)
  Dunit = g/cm3
  Dvalue = 4.26
  Group = -> [Ti_element003,O_element098]
  conduct = 2
  density = 1
  expand = 3
  formula = G4_TITANIUM_DIOXIDE
  name = G4_TITANIUM_DIOXIDE
  specific = 4
FEATURE [App::DocumentObjectGroupPython] C_element114  label="C_element : 061"  # scripted group (container) (typed FeaturePython)
  n = 7
  ref = C_element
FEATURE [App::DocumentObjectGroupPython] H_element104  label="H_element : 055"  # scripted group (container) (typed FeaturePython)
  n = 8
  ref = H_element
FEATURE [App::DocumentObjectGroupPython] G4_TOLUENE  # scripted group (container) (typed FeaturePython)
  Dunit = g/cm3
  Dvalue = 0.8669
  Group = -> [C_element114,H_element104]
  conduct = 2
  density = 1
  expand = 3
  formula = G4_TOLUENE
  name = G4_TOLUENE
  specific = 4
FEATURE [App::DocumentObjectGroupPython] C_element115  label="C_element : 062"  # scripted group (container) (typed FeaturePython)
  n = 2
  ref = C_element
FEATURE [App::DocumentObjectGroupPython] H_element105  label="H_element : 056"  # scripted group (container) (typed FeaturePython)
  n = 1
  ref = H_element
FEATURE [App::DocumentObjectGroupPython] Cl_element028  label="Cl_element : 014"  # scripted group (container) (typed FeaturePython)
  n = 3
  ref = Cl_element
FEATURE [App::DocumentObjectGroupPython] G4_TRICHLOROETHYLENE  # scripted group (container) (typed FeaturePython)
  Dunit = g/cm3
  Dvalue = 1.46
  Group = -> [C_element115,H_element105,Cl_element028]
  conduct = 2
  density = 1
  expand = 3
  formula = G4_TRICHLOROETHYLENE
  name = G4_TRICHLOROETHYLENE
  specific = 4
FEATURE [App::DocumentObjectGroupPython] C_element116  label="C_element : 063"  # scripted group (container) (typed FeaturePython)
  n = 6
  ref = C_element
FEATURE [App::DocumentObjectGroupPython] H_element106  label="H_element : 15"  # scripted group (container) (typed FeaturePython)
  n = 15
  ref = H_element
FEATURE [App::DocumentObjectGroupPython] O_element099  label="O_element : 053"  # scripted group (container) (typed FeaturePython)
  n = 4
  ref = O_element
FEATURE [App::DocumentObjectGroupPython] P_element012  label="P_element : 1"  # scripted group (container) (typed FeaturePython)
  n = 1
  ref = P_element
FEATURE [App::DocumentObjectGroupPython] G4_TRIETHYL_PHOSPHATE  # scripted group (container) (typed FeaturePython)
  Dunit = g/cm3
  Dvalue = 1.07
  Group = -> [C_element116,H_element106,O_element099,P_element012]
  conduct = 2
  density = 1
  expand = 3
  formula = G4_TRIETHYL_PHOSPHATE
  name = G4_TRIETHYL_PHOSPHATE
  specific = 4
FEATURE [App::DocumentObjectGroupPython] W_element003  label="W_element : 003"  # scripted group (container) (typed FeaturePython)
  n = 1
  ref = W_element
FEATURE [App::DocumentObjectGroupPython] F_element017  label="F_element : 6"  # scripted group (container) (typed FeaturePython)
  n = 6
  ref = F_element
FEATURE [App::DocumentObjectGroupPython] G4_TUNGSTEN_HEXAFLUORIDE  # scripted group (container) (typed FeaturePython)
  Dunit = g/cm3
  Dvalue = 2.4
  Group = -> [W_element003,F_element017]
  conduct = 2
  density = 1
  expand = 3
  formula = G4_TUNGSTEN_HEXAFLUORIDE
  name = G4_TUNGSTEN_HEXAFLUORIDE
  specific = 4
FEATURE [App::DocumentObjectGroupPython] U_element001  label="U_element : 1"  # scripted group (container) (typed FeaturePython)
  n = 1
  ref = U_element
FEATURE [App::DocumentObjectGroupPython] C_element117  label="C_element : 064"  # scripted group (container) (typed FeaturePython)
  n = 2
  ref = C_element
FEATURE [App::DocumentObjectGroupPython] G4_URANIUM_DICARBIDE  # scripted group (container) (typed FeaturePython)
  Dunit = g/cm3
  Dvalue = 11.28
  Group = -> [U_element001,C_element117]
  conduct = 2
  density = 1
  expand = 3
  formula = G4_URANIUM_DICARBIDE
  name = G4_URANIUM_DICARBIDE
  specific = 4
FEATURE [App::DocumentObjectGroupPython] U_element002  label="U_element : 002"  # scripted group (container) (typed FeaturePython)
  n = 1
  ref = U_element
FEATURE [App::DocumentObjectGroupPython] C_element118  label="C_element : 065"  # scripted group (container) (typed FeaturePython)
  n = 1
  ref = C_element
FEATURE [App::DocumentObjectGroupPython] G4_URANIUM_MONOCARBIDE  # scripted group (container) (typed FeaturePython)
  Dunit = g/cm3
  Dvalue = 13.63
  Group = -> [U_element002,C_element118]
  conduct = 2
  density = 1
  expand = 3
  formula = G4_URANIUM_MONOCARBIDE
  name = G4_URANIUM_MONOCARBIDE
  specific = 4
FEATURE [App::DocumentObjectGroupPython] U_element003  label="U_element : 003"  # scripted group (container) (typed FeaturePython)
  n = 1
  ref = U_element
FEATURE [App::DocumentObjectGroupPython] O_element100  label="O_element : 054"  # scripted group (container) (typed FeaturePython)
  n = 2
  ref = O_element
FEATURE [App::DocumentObjectGroupPython] G4_URANIUM_OXIDE  # scripted group (container) (typed FeaturePython)
  Dunit = g/cm3
  Dvalue = 10.96
  Group = -> [U_element003,O_element100]
  conduct = 2
  density = 1
  expand = 3
  formula = G4_URANIUM_OXIDE
  name = G4_URANIUM_OXIDE
  specific = 4
FEATURE [App::DocumentObjectGroupPython] C_element119  label="C_element : 066"  # scripted group (container) (typed FeaturePython)
  n = 1
  ref = C_element
FEATURE [App::DocumentObjectGroupPython] H_element107  label="H_element : 057"  # scripted group (container) (typed FeaturePython)
  n = 4
  ref = H_element
FEATURE [App::DocumentObjectGroupPython] N_element046  label="N_element : 019"  # scripted group (container) (typed FeaturePython)
  n = 2
  ref = N_element
FEATURE [App::DocumentObjectGroupPython] O_element101  label="O_element : 055"  # scripted group (container) (typed FeaturePython)
  n = 1
  ref = O_element
FEATURE [App::DocumentObjectGroupPython] G4_UREA  # scripted group (container) (typed FeaturePython)
  Dunit = g/cm3
  Dvalue = 1.323
  Group = -> [C_element119,H_element107,N_element046,O_element101]
  conduct = 2
  density = 1
  expand = 3
  formula = G4_UREA
  name = G4_UREA
  specific = 4
FEATURE [App::DocumentObjectGroupPython] C_element120  label="C_element : 067"  # scripted group (container) (typed FeaturePython)
  n = 5
  ref = C_element
FEATURE [App::DocumentObjectGroupPython] H_element108  label="H_element : 058"  # scripted group (container) (typed FeaturePython)
  n = 11
  ref = H_element
FEATURE [App::DocumentObjectGroupPython] N_element047  label="N_element : 020"  # scripted group (container) (typed FeaturePython)
  n = 1
  ref = N_element
FEATURE [App::DocumentObjectGroupPython] O_element102  label="O_element : 056"  # scripted group (container) (typed FeaturePython)
  n = 2
  ref = O_element
FEATURE [App::DocumentObjectGroupPython] G4_VALINE  # scripted group (container) (typed FeaturePython)
  Dunit = g/cm3
  Dvalue = 1.23
  Group = -> [C_element120,H_element108,N_element047,O_element102]
  conduct = 2
  density = 1
  expand = 3
  formula = G4_VALINE
  name = G4_VALINE
  specific = 4
FEATURE [App::DocumentObjectGroupPython] H_element109  label="H_element : 0.009"  # scripted group (container) (typed FeaturePython)
  n = 0.009417
FEATURE [App::DocumentObjectGroupPython] C_element121  label="C_element : 0.281"  # scripted group (container) (typed FeaturePython)
  n = 0.280555
FEATURE [App::DocumentObjectGroupPython] F_element018  label="F_element : 0.710"  # scripted group (container) (typed FeaturePython)
  n = 0.710028
FEATURE [App::DocumentObjectGroupPython] G4_VITON  # scripted group (container) (typed FeaturePython)
  Dunit = g/cm3
  Dvalue = 1.8
  Group = -> [H_element109,C_element121,F_element018]
  conduct = 2
  density = 1
  expand = 3
  formula = G4_VITON
  name = G4_VITON
  specific = 4
FEATURE [App::DocumentObjectGroupPython] H_element110  label="H_element : 059"  # scripted group (container) (typed FeaturePython)
  n = 2
  ref = H_element
FEATURE [App::DocumentObjectGroupPython] O_element103  label="O_element : 057"  # scripted group (container) (typed FeaturePython)
  n = 1
  ref = O_element
FEATURE [App::DocumentObjectGroupPython] G4_WATER  # scripted group (container) (typed FeaturePython)
  Dunit = g/cm3
  Dvalue = 1
  Group = -> [H_element110,O_element103]
  conduct = 2
  density = 1
  expand = 3
  formula = G4_WATER
  name = G4_WATER
  specific = 4
FEATURE [App::DocumentObjectGroupPython] H_element111  label="H_element : 060"  # scripted group (container) (typed FeaturePython)
  n = 2
  ref = H_element
FEATURE [App::DocumentObjectGroupPython] O_element104  label="O_element : 058"  # scripted group (container) (typed FeaturePython)
  n = 1
  ref = O_element
FEATURE [App::DocumentObjectGroupPython] G4_WATER_VAPOR  # scripted group (container) (typed FeaturePython)
  Dunit = g/cm3
  Dvalue = 0.000756182
  Group = -> [H_element111,O_element104]
  conduct = 2
  density = 1
  expand = 3
  formula = G4_WATER_VAPOR
  name = G4_WATER_VAPOR
  specific = 4
FEATURE [App::DocumentObjectGroupPython] C_element122  label="C_element : 068"  # scripted group (container) (typed FeaturePython)
  n = 8
  ref = C_element
FEATURE [App::DocumentObjectGroupPython] H_element112  label="H_element : 061"  # scripted group (container) (typed FeaturePython)
  n = 10
  ref = H_element
FEATURE [App::DocumentObjectGroupPython] G4_XYLENE  # scripted group (container) (typed FeaturePython)
  Dunit = g/cm3
  Dvalue = 0.87
  Group = -> [C_element122,H_element112]
  conduct = 2
  density = 1
  expand = 3
  formula = G4_XYLENE
  name = G4_XYLENE
  specific = 4
FEATURE [App::DocumentObjectGroupPython] C_element123  label="C_element : 069"  # scripted group (container) (typed FeaturePython)
  n = 1
  ref = C_element
FEATURE [App::DocumentObjectGroupPython] G4_GRAPHITE  # scripted group (container) (typed FeaturePython)
  Dunit = g/cm3
  Dvalue = 2.21
  Group = -> [C_element123]
  conduct = 2
  density = 1
  expand = 3
  formula = G4_GRAPHITE
  name = G4_GRAPHITE
  specific = 4
FEATURE [App::DocumentObjectGroupPython] NIST  # scripted group (container) (typed FeaturePython)
  Group = -> [G4_A_150_TISSUE,G4_ACETONE,G4_ACETYLENE,G4_ADENINE,G4_ADIPOSE_TISSUE_ICRP,G4_AIR001,G4_ALANINE,G4_ALUMINUM_OXIDE,G4_AMBER,G4_AMMONIA,G4_ANILINE,G4_ANTHRACENE,G4_B_100_BONE,G4_BAKELITE,G4_BARIUM_FLUORIDE,G4_BARIUM_SULFATE,G4_BENZENE,G4_BERYLLIUM_OXIDE,G4_BGO,G4_BLOOD_ICRP,G4_BONE_COMPACT_ICRU,G4_BONE_CORTICAL_ICRP,G4_BORON_CARBIDE,G4_BORON_OXIDE,G4_BRAIN_ICRP,G4_BUTANE,G4_N_BUTYL_ALCOHOL,G4_C_552,+152 more]
FEATURE [App::DocumentObjectGroupPython] H_element113  label="H_element : 062"  # scripted group (container) (typed FeaturePython)
  n = 1
  ref = H_element
FEATURE [App::DocumentObjectGroupPython] G4_H  # scripted group (container) (typed FeaturePython)
  Dunit = g/cm3
  Dvalue = 8.3748e-05
  Group = -> [H_element113]
  conduct = 2
  density = 1
  expand = 3
  formula = H
  name = G4_H
  specific = 4
FEATURE [App::DocumentObjectGroupPython] He_element001  label="He_element : 1"  # scripted group (container) (typed FeaturePython)
  n = 1
  ref = He_element
FEATURE [App::DocumentObjectGroupPython] G4_He  # scripted group (container) (typed FeaturePython)
  Dunit = g/cm3
  Dvalue = 0.000166322
  Group = -> [He_element001]
  conduct = 2
  density = 1
  expand = 3
  formula = He
  name = G4_He
  specific = 4
FEATURE [App::DocumentObjectGroupPython] Li_element008  label="Li_element : 008"  # scripted group (container) (typed FeaturePython)
  n = 1
  ref = Li_element
FEATURE [App::DocumentObjectGroupPython] G4_Li  # scripted group (container) (typed FeaturePython)
  Dunit = g/cm3
  Dvalue = 0.534
  Group = -> [Li_element008]
  conduct = 2
  density = 1
  expand = 3
  formula = Li
  name = G4_Li
  specific = 4
FEATURE [App::DocumentObjectGroupPython] Be_element002  label="Be_element : 002"  # scripted group (container) (typed FeaturePython)
  n = 1
  ref = Be_element
FEATURE [App::DocumentObjectGroupPython] G4_Be  # scripted group (container) (typed FeaturePython)
  Dunit = g/cm3
  Dvalue = 1.848
  Group = -> [Be_element002]
  conduct = 2
  density = 1
  expand = 3
  formula = Be
  name = G4_Be
  specific = 4
FEATURE [App::DocumentObjectGroupPython] B_element007  label="B_element : 007"  # scripted group (container) (typed FeaturePython)
  n = 1
  ref = B_element
FEATURE [App::DocumentObjectGroupPython] G4_B  # scripted group (container) (typed FeaturePython)
  Dunit = g/cm3
  Dvalue = 2.37
  Group = -> [B_element007]
  conduct = 2
  density = 1
  expand = 3
  formula = B
  name = G4_B
  specific = 4
FEATURE [App::DocumentObjectGroupPython] C_element124  label="C_element : 070"  # scripted group (container) (typed FeaturePython)
  n = 1
  ref = C_element
FEATURE [App::DocumentObjectGroupPython] G4_C  # scripted group (container) (typed FeaturePython)
  Dunit = g/cm3
  Dvalue = 2
  Group = -> [C_element124]
  conduct = 2
  density = 1
  expand = 3
  formula = C
  name = G4_C
  specific = 4
FEATURE [App::DocumentObjectGroupPython] N_element048  label="N_element : 021"  # scripted group (container) (typed FeaturePython)
  n = 1
  ref = N_element
FEATURE [App::DocumentObjectGroupPython] G4_N  # scripted group (container) (typed FeaturePython)
  Dunit = g/cm3
  Dvalue = 0.0011652
  Group = -> [N_element048]
  conduct = 2
  density = 1
  expand = 3
  formula = N
  name = G4_N
  specific = 4
FEATURE [App::DocumentObjectGroupPython] O_element105  label="O_element : 059"  # scripted group (container) (typed FeaturePython)
  n = 1
  ref = O_element
FEATURE [App::DocumentObjectGroupPython] G4_O  # scripted group (container) (typed FeaturePython)
  Dunit = g/cm3
  Dvalue = 0.00133151
  Group = -> [O_element105]
  conduct = 2
  density = 1
  expand = 3
  formula = O
  name = G4_O
  specific = 4
FEATURE [App::DocumentObjectGroupPython] F_element019  label="F_element : 008"  # scripted group (container) (typed FeaturePython)
  n = 1
  ref = F_element
FEATURE [App::DocumentObjectGroupPython] G4_F  # scripted group (container) (typed FeaturePython)
  Dunit = g/cm3
  Dvalue = 0.00158029
  Group = -> [F_element019]
  conduct = 2
  density = 1
  expand = 3
  formula = F
  name = G4_F
  specific = 4
FEATURE [App::DocumentObjectGroupPython] Ne_element001  label="Ne_element : 1"  # scripted group (container) (typed FeaturePython)
  n = 1
  ref = Ne_element
FEATURE [App::DocumentObjectGroupPython] G4_Ne  # scripted group (container) (typed FeaturePython)
  Dunit = g/cm3
  Dvalue = 0.000838505
  Group = -> [Ne_element001]
  conduct = 2
  density = 1
  expand = 3
  formula = Ne
  name = G4_Ne
  specific = 4
FEATURE [App::DocumentObjectGroupPython] Na_element020  label="Na_element : 005"  # scripted group (container) (typed FeaturePython)
  n = 1
  ref = Na_element
FEATURE [App::DocumentObjectGroupPython] G4_Na  # scripted group (container) (typed FeaturePython)
  Dunit = g/cm3
  Dvalue = 0.971
  Group = -> [Na_element020]
  conduct = 2
  density = 1
  expand = 3
  formula = Na
  name = G4_Na
  specific = 4
FEATURE [App::DocumentObjectGroupPython] Mg_element011  label="Mg_element : 005"  # scripted group (container) (typed FeaturePython)
  n = 1
  ref = Mg_element
FEATURE [App::DocumentObjectGroupPython] G4_Mg  # scripted group (container) (typed FeaturePython)
  Dunit = g/cm3
  Dvalue = 1.74
  Group = -> [Mg_element011]
  conduct = 2
  density = 1
  expand = 3
  formula = Mg
  name = G4_Mg
  specific = 4
FEATURE [App::DocumentObjectGroupPython] Al_element004  label="Al_element : 1"  # scripted group (container) (typed FeaturePython)
  n = 1
  ref = Al_element
FEATURE [App::DocumentObjectGroupPython] G4_Al  # scripted group (container) (typed FeaturePython)
  Dunit = g/cm3
  Dvalue = 2.699
  Group = -> [Al_element004]
  conduct = 2
  density = 1
  expand = 3
  formula = Al
  name = G4_Al
  specific = 4
FEATURE [App::DocumentObjectGroupPython] Si_element007  label="Si_element : 002"  # scripted group (container) (typed FeaturePython)
  n = 1
  ref = Si_element
FEATURE [App::DocumentObjectGroupPython] G4_Si  # scripted group (container) (typed FeaturePython)
  Dunit = g/cm3
  Dvalue = 2.33
  Group = -> [Si_element007]
  conduct = 2
  density = 1
  expand = 3
  formula = Si
  name = G4_Si
  specific = 4
FEATURE [App::DocumentObjectGroupPython] P_element013  label="P_element : 002"  # scripted group (container) (typed FeaturePython)
  n = 1
  ref = P_element
FEATURE [App::DocumentObjectGroupPython] G4_P  # scripted group (container) (typed FeaturePython)
  Dunit = g/cm3
  Dvalue = 2.2
  Group = -> [P_element013]
  conduct = 2
  density = 1
  expand = 3
  formula = P
  name = G4_P
  specific = 4
FEATURE [App::DocumentObjectGroupPython] S_element023  label="S_element : 007"  # scripted group (container) (typed FeaturePython)
  n = 1
  ref = S_element
FEATURE [App::DocumentObjectGroupPython] G4_S  # scripted group (container) (typed FeaturePython)
  Dunit = g/cm3
  Dvalue = 2
  Group = -> [S_element023]
  conduct = 2
  density = 1
  expand = 3
  formula = S
  name = G4_S
  specific = 4
FEATURE [App::DocumentObjectGroupPython] Cl_element029  label="Cl_element : 015"  # scripted group (container) (typed FeaturePython)
  n = 1
  ref = Cl_element
FEATURE [App::DocumentObjectGroupPython] G4_Cl  # scripted group (container) (typed FeaturePython)
  Dunit = g/cm3
  Dvalue = 0.00299473
  Group = -> [Cl_element029]
  conduct = 2
  density = 1
  expand = 3
  formula = Cl
  name = G4_Cl
  specific = 4
FEATURE [App::DocumentObjectGroupPython] Ar_element002  label="Ar_element : 1"  # scripted group (container) (typed FeaturePython)
  n = 1
  ref = Ar_element
FEATURE [App::DocumentObjectGroupPython] G4_Ar  # scripted group (container) (typed FeaturePython)
  Dunit = g/cm3
  Dvalue = 0.00166201
  Group = -> [Ar_element002]
  conduct = 2
  density = 1
  expand = 3
  formula = Ar
  name = G4_Ar
  specific = 4
FEATURE [App::DocumentObjectGroupPython] K_element013  label="K_element : 003"  # scripted group (container) (typed FeaturePython)
  n = 1
  ref = K_element
FEATURE [App::DocumentObjectGroupPython] G4_K  # scripted group (container) (typed FeaturePython)
  Dunit = g/cm3
  Dvalue = 0.862
  Group = -> [K_element013]
  conduct = 2
  density = 1
  expand = 3
  formula = K
  name = G4_K
  specific = 4
FEATURE [App::DocumentObjectGroupPython] Ca_element014  label="Ca_element : 007"  # scripted group (container) (typed FeaturePython)
  n = 1
  ref = Ca_element
FEATURE [App::DocumentObjectGroupPython] G4_Ca  # scripted group (container) (typed FeaturePython)
  Dunit = g/cm3
  Dvalue = 1.55
  Group = -> [Ca_element014]
  conduct = 2
  density = 1
  expand = 3
  formula = Ca
  name = G4_Ca
  specific = 4
FEATURE [App::DocumentObjectGroupPython] Sc_element001  label="Sc_element : 1"  # scripted group (container) (typed FeaturePython)
  n = 1
  ref = Sc_element
FEATURE [App::DocumentObjectGroupPython] G4_Sc  # scripted group (container) (typed FeaturePython)
  Dunit = g/cm3
  Dvalue = 2.989
  Group = -> [Sc_element001]
  conduct = 2
  density = 1
  expand = 3
  formula = Sc
  name = G4_Sc
  specific = 4
FEATURE [App::DocumentObjectGroupPython] Ti_element004  label="Ti_element : 002"  # scripted group (container) (typed FeaturePython)
  n = 1
  ref = Ti_element
FEATURE [App::DocumentObjectGroupPython] G4_Ti  # scripted group (container) (typed FeaturePython)
  Dunit = g/cm3
  Dvalue = 4.54
  Group = -> [Ti_element004]
  conduct = 2
  density = 1
  expand = 3
  formula = Ti
  name = G4_Ti
  specific = 4
FEATURE [App::DocumentObjectGroupPython] V_element001  label="V_element : 1"  # scripted group (container) (typed FeaturePython)
  n = 1
  ref = V_element
FEATURE [App::DocumentObjectGroupPython] G4_V  # scripted group (container) (typed FeaturePython)
  Dunit = g/cm3
  Dvalue = 6.11
  Group = -> [V_element001]
  conduct = 2
  density = 1
  expand = 3
  formula = V
  name = G4_V
  specific = 4
FEATURE [App::DocumentObjectGroupPython] Cr_element001  label="Cr_element : 1"  # scripted group (container) (typed FeaturePython)
  n = 1
  ref = Cr_element
FEATURE [App::DocumentObjectGroupPython] G4_Cr  # scripted group (container) (typed FeaturePython)
  Dunit = g/cm3
  Dvalue = 7.18
  Group = -> [Cr_element001]
  conduct = 2
  density = 1
  expand = 3
  formula = Cr
  name = G4_Cr
  specific = 4
FEATURE [App::DocumentObjectGroupPython] Mn_element001  label="Mn_element : 1"  # scripted group (container) (typed FeaturePython)
  n = 1
  ref = Mn_element
FEATURE [App::DocumentObjectGroupPython] G4_Mn  # scripted group (container) (typed FeaturePython)
  Dunit = g/cm3
  Dvalue = 7.44
  Group = -> [Mn_element001]
  conduct = 2
  density = 1
  expand = 3
  formula = Mn
  name = G4_Mn
  specific = 4
FEATURE [App::DocumentObjectGroupPython] Fe_element007  label="Fe_element : 004"  # scripted group (container) (typed FeaturePython)
  n = 1
  ref = Fe_element
FEATURE [App::DocumentObjectGroupPython] G4_Fe  # scripted group (container) (typed FeaturePython)
  Dunit = g/cm3
  Dvalue = 7.874
  Group = -> [Fe_element007]
  conduct = 2
  density = 1
  expand = 3
  formula = Fe
  name = G4_Fe
  specific = 4
FEATURE [App::DocumentObjectGroupPython] Co_element001  label="Co_element : 1"  # scripted group (container) (typed FeaturePython)
  n = 1
  ref = Co_element
FEATURE [App::DocumentObjectGroupPython] G4_Co  # scripted group (container) (typed FeaturePython)
  Dunit = g/cm3
  Dvalue = 8.9
  Group = -> [Co_element001]
  conduct = 2
  density = 1
  expand = 3
  formula = Co
  name = G4_Co
  specific = 4
FEATURE [App::DocumentObjectGroupPython] Ni_element001  label="Ni_element : 1"  # scripted group (container) (typed FeaturePython)
  n = 1
  ref = Ni_element
FEATURE [App::DocumentObjectGroupPython] G4_Ni  # scripted group (container) (typed FeaturePython)
  Dunit = g/cm3
  Dvalue = 8.902
  Group = -> [Ni_element001]
  conduct = 2
  density = 1
  expand = 3
  formula = Ni
  name = G4_Ni
  specific = 4
FEATURE [App::DocumentObjectGroupPython] Cu_element001  label="Cu_element : 1"  # scripted group (container) (typed FeaturePython)
  n = 1
  ref = Cu_element
FEATURE [App::DocumentObjectGroupPython] G4_Cu  # scripted group (container) (typed FeaturePython)
  Dunit = g/cm3
  Dvalue = 8.96
  Group = -> [Cu_element001]
  conduct = 2
  density = 1
  expand = 3
  formula = Cu
  name = G4_Cu
  specific = 4
FEATURE [App::DocumentObjectGroupPython] Zn_element001  label="Zn_element : 1"  # scripted group (container) (typed FeaturePython)
  n = 1
  ref = Zn_element
FEATURE [App::DocumentObjectGroupPython] G4_Zn  # scripted group (container) (typed FeaturePython)
  Dunit = g/cm3
  Dvalue = 7.133
  Group = -> [Zn_element001]
  conduct = 2
  density = 1
  expand = 3
  formula = Zn
  name = G4_Zn
  specific = 4
FEATURE [App::DocumentObjectGroupPython] Ga_element002  label="Ga_element : 002"  # scripted group (container) (typed FeaturePython)
  n = 1
  ref = Ga_element
FEATURE [App::DocumentObjectGroupPython] G4_Ga  # scripted group (container) (typed FeaturePython)
  Dunit = g/cm3
  Dvalue = 5.904
  Group = -> [Ga_element002]
  conduct = 2
  density = 1
  expand = 3
  formula = Ga
  name = G4_Ga
  specific = 4
FEATURE [App::DocumentObjectGroupPython] Ge_element002  label="Ge_element : 1"  # scripted group (container) (typed FeaturePython)
  n = 1
  ref = Ge_element
FEATURE [App::DocumentObjectGroupPython] G4_Ge  # scripted group (container) (typed FeaturePython)
  Dunit = g/cm3
  Dvalue = 5.323
  Group = -> [Ge_element002]
  conduct = 2
  density = 1
  expand = 3
  formula = Ge
  name = G4_Ge
  specific = 4
FEATURE [App::DocumentObjectGroupPython] As_element003  label="As_element : 002"  # scripted group (container) (typed FeaturePython)
  n = 1
  ref = As_element
FEATURE [App::DocumentObjectGroupPython] G4_As  # scripted group (container) (typed FeaturePython)
  Dunit = g/cm3
  Dvalue = 5.73
  Group = -> [As_element003]
  conduct = 2
  density = 1
  expand = 3
  formula = As
  name = G4_As
  specific = 4
FEATURE [App::DocumentObjectGroupPython] Se_element001  label="Se_element : 1"  # scripted group (container) (typed FeaturePython)
  n = 1
  ref = Se_element
FEATURE [App::DocumentObjectGroupPython] G4_Se  # scripted group (container) (typed FeaturePython)
  Dunit = g/cm3
  Dvalue = 4.5
  Group = -> [Se_element001]
  conduct = 2
  density = 1
  expand = 3
  formula = Se
  name = G4_Se
  specific = 4
FEATURE [App::DocumentObjectGroupPython] Br_element007  label="Br_element : 004"  # scripted group (container) (typed FeaturePython)
  n = 1
  ref = Br_element
FEATURE [App::DocumentObjectGroupPython] G4_Br  # scripted group (container) (typed FeaturePython)
  Dunit = g/cm3
  Dvalue = 0.0070721
  Group = -> [Br_element007]
  conduct = 2
  density = 1
  expand = 3
  formula = Br
  name = G4_Br
  specific = 4
FEATURE [App::DocumentObjectGroupPython] Kr_element001  label="Kr_element : 1"  # scripted group (container) (typed FeaturePython)
  n = 1
  ref = Kr_element
FEATURE [App::DocumentObjectGroupPython] G4_Kr  # scripted group (container) (typed FeaturePython)
  Dunit = g/cm3
  Dvalue = 0.00347832
  Group = -> [Kr_element001]
  conduct = 2
  density = 1
  expand = 3
  formula = Kr
  name = G4_Kr
  specific = 4
FEATURE [App::DocumentObjectGroupPython] Rb_element001  label="Rb_element : 1"  # scripted group (container) (typed FeaturePython)
  n = 1
  ref = Rb_element
FEATURE [App::DocumentObjectGroupPython] G4_Rb  # scripted group (container) (typed FeaturePython)
  Dunit = g/cm3
  Dvalue = 1.532
  Group = -> [Rb_element001]
  conduct = 2
  density = 1
  expand = 3
  formula = Rb
  name = G4_Rb
  specific = 4
FEATURE [App::DocumentObjectGroupPython] Sr_element001  label="Sr_element : 1"  # scripted group (container) (typed FeaturePython)
  n = 1
  ref = Sr_element
FEATURE [App::DocumentObjectGroupPython] G4_Sr  # scripted group (container) (typed FeaturePython)
  Dunit = g/cm3
  Dvalue = 2.54
  Group = -> [Sr_element001]
  conduct = 2
  density = 1
  expand = 3
  formula = Sr
  name = G4_Sr
  specific = 4
FEATURE [App::DocumentObjectGroupPython] Y_element001  label="Y_element : 1"  # scripted group (container) (typed FeaturePython)
  n = 1
  ref = Y_element
FEATURE [App::DocumentObjectGroupPython] G4_Y  # scripted group (container) (typed FeaturePython)
  Dunit = g/cm3
  Dvalue = 4.469
  Group = -> [Y_element001]
  conduct = 2
  density = 1
  expand = 3
  formula = Y
  name = G4_Y
  specific = 4
FEATURE [App::DocumentObjectGroupPython] Zr_element001  label="Zr_element : 1"  # scripted group (container) (typed FeaturePython)
  n = 1
  ref = Zr_element
FEATURE [App::DocumentObjectGroupPython] G4_Zr  # scripted group (container) (typed FeaturePython)
  Dunit = g/cm3
  Dvalue = 6.506
  Group = -> [Zr_element001]
  conduct = 2
  density = 1
  expand = 3
  formula = Zr
  name = G4_Zr
  specific = 4
FEATURE [App::DocumentObjectGroupPython] Nb_element001  label="Nb_element : 1"  # scripted group (container) (typed FeaturePython)
  n = 1
  ref = Nb_element
FEATURE [App::DocumentObjectGroupPython] G4_Nb  # scripted group (container) (typed FeaturePython)
  Dunit = g/cm3
  Dvalue = 8.57
  Group = -> [Nb_element001]
  conduct = 2
  density = 1
  expand = 3
  formula = Nb
  name = G4_Nb
  specific = 4
FEATURE [App::DocumentObjectGroupPython] Mo_element001  label="Mo_element : 1"  # scripted group (container) (typed FeaturePython)
  n = 1
  ref = Mo_element
FEATURE [App::DocumentObjectGroupPython] G4_Mo  # scripted group (container) (typed FeaturePython)
  Dunit = g/cm3
  Dvalue = 10.22
  Group = -> [Mo_element001]
  conduct = 2
  density = 1
  expand = 3
  formula = Mo
  name = G4_Mo
  specific = 4
FEATURE [App::DocumentObjectGroupPython] Tc_element001  label="Tc_element : 1"  # scripted group (container) (typed FeaturePython)
  n = 1
  ref = Tc_element
FEATURE [App::DocumentObjectGroupPython] G4_Tc  # scripted group (container) (typed FeaturePython)
  Dunit = g/cm3
  Dvalue = 11.5
  Group = -> [Tc_element001]
  conduct = 2
  density = 1
  expand = 3
  formula = Tc
  name = G4_Tc
  specific = 4
FEATURE [App::DocumentObjectGroupPython] Ru_element001  label="Ru_element : 1"  # scripted group (container) (typed FeaturePython)
  n = 1
  ref = Ru_element
FEATURE [App::DocumentObjectGroupPython] G4_Ru  # scripted group (container) (typed FeaturePython)
  Dunit = g/cm3
  Dvalue = 12.41
  Group = -> [Ru_element001]
  conduct = 2
  density = 1
  expand = 3
  formula = Ru
  name = G4_Ru
  specific = 4
FEATURE [App::DocumentObjectGroupPython] Rh_element001  label="Rh_element : 1"  # scripted group (container) (typed FeaturePython)
  n = 1
  ref = Rh_element
FEATURE [App::DocumentObjectGroupPython] G4_Rh  # scripted group (container) (typed FeaturePython)
  Dunit = g/cm3
  Dvalue = 12.41
  Group = -> [Rh_element001]
  conduct = 2
  density = 1
  expand = 3
  formula = Rh
  name = G4_Rh
  specific = 4
FEATURE [App::DocumentObjectGroupPython] Pd_element001  label="Pd_element : 1"  # scripted group (container) (typed FeaturePython)
  n = 1
  ref = Pd_element
FEATURE [App::DocumentObjectGroupPython] G4_Pd  # scripted group (container) (typed FeaturePython)
  Dunit = g/cm3
  Dvalue = 12.02
  Group = -> [Pd_element001]
  conduct = 2
  density = 1
  expand = 3
  formula = Pd
  name = G4_Pd
  specific = 4
FEATURE [App::DocumentObjectGroupPython] Ag_element006  label="Ag_element : 004"  # scripted group (container) (typed FeaturePython)
  n = 1
  ref = Ag_element
FEATURE [App::DocumentObjectGroupPython] G4_Ag  # scripted group (container) (typed FeaturePython)
  Dunit = g/cm3
  Dvalue = 10.5
  Group = -> [Ag_element006]
  conduct = 2
  density = 1
  expand = 3
  formula = Ag
  name = G4_Ag
  specific = 4
FEATURE [App::DocumentObjectGroupPython] Cd_element003  label="Cd_element : 003"  # scripted group (container) (typed FeaturePython)
  n = 1
  ref = Cd_element
FEATURE [App::DocumentObjectGroupPython] G4_Cd  # scripted group (container) (typed FeaturePython)
  Dunit = g/cm3
  Dvalue = 8.65
  Group = -> [Cd_element003]
  conduct = 2
  density = 1
  expand = 3
  formula = Cd
  name = G4_Cd
  specific = 4
FEATURE [App::DocumentObjectGroupPython] In_element001  label="In_element : 1"  # scripted group (container) (typed FeaturePython)
  n = 1
  ref = In_element
FEATURE [App::DocumentObjectGroupPython] G4_In  # scripted group (container) (typed FeaturePython)
  Dunit = g/cm3
  Dvalue = 7.31
  Group = -> [In_element001]
  conduct = 2
  density = 1
  expand = 3
  formula = In
  name = G4_In
  specific = 4
FEATURE [App::DocumentObjectGroupPython] Sn_element001  label="Sn_element : 1"  # scripted group (container) (typed FeaturePython)
  n = 1
  ref = Sn_element
FEATURE [App::DocumentObjectGroupPython] G4_Sn  # scripted group (container) (typed FeaturePython)
  Dunit = g/cm3
  Dvalue = 7.31
  Group = -> [Sn_element001]
  conduct = 2
  density = 1
  expand = 3
  formula = Sn
  name = G4_Sn
  specific = 4
FEATURE [App::DocumentObjectGroupPython] Sb_element001  label="Sb_element : 1"  # scripted group (container) (typed FeaturePython)
  n = 1
  ref = Sb_element
FEATURE [App::DocumentObjectGroupPython] G4_Sb  # scripted group (container) (typed FeaturePython)
  Dunit = g/cm3
  Dvalue = 6.691
  Group = -> [Sb_element001]
  conduct = 2
  density = 1
  expand = 3
  formula = Sb
  name = G4_Sb
  specific = 4
FEATURE [App::DocumentObjectGroupPython] Te_element002  label="Te_element : 002"  # scripted group (container) (typed FeaturePython)
  n = 1
  ref = Te_element
FEATURE [App::DocumentObjectGroupPython] G4_Te  # scripted group (container) (typed FeaturePython)
  Dunit = g/cm3
  Dvalue = 6.24
  Group = -> [Te_element002]
  conduct = 2
  density = 1
  expand = 3
  formula = Te
  name = G4_Te
  specific = 4
FEATURE [App::DocumentObjectGroupPython] I_element010  label="I_element : 006"  # scripted group (container) (typed FeaturePython)
  n = 1
  ref = I_element
FEATURE [App::DocumentObjectGroupPython] G4_I  # scripted group (container) (typed FeaturePython)
  Dunit = g/cm3
  Dvalue = 4.93
  Group = -> [I_element010]
  conduct = 2
  density = 1
  expand = 3
  formula = I
  name = G4_I
  specific = 4
FEATURE [App::DocumentObjectGroupPython] Xe_element001  label="Xe_element : 1"  # scripted group (container) (typed FeaturePython)
  n = 1
  ref = Xe_element
FEATURE [App::DocumentObjectGroupPython] G4_Xe  # scripted group (container) (typed FeaturePython)
  Dunit = g/cm3
  Dvalue = 0.00548536
  Group = -> [Xe_element001]
  conduct = 2
  density = 1
  expand = 3
  formula = Xe
  name = G4_Xe
  specific = 4
FEATURE [App::DocumentObjectGroupPython] Cs_element003  label="Cs_element : 003"  # scripted group (container) (typed FeaturePython)
  n = 1
  ref = Cs_element
FEATURE [App::DocumentObjectGroupPython] G4_Cs  # scripted group (container) (typed FeaturePython)
  Dunit = g/cm3
  Dvalue = 1.873
  Group = -> [Cs_element003]
  conduct = 2
  density = 1
  expand = 3
  formula = Cs
  name = G4_Cs
  specific = 4
FEATURE [App::DocumentObjectGroupPython] Ba_element003  label="Ba_element : 003"  # scripted group (container) (typed FeaturePython)
  n = 1
  ref = Ba_element
FEATURE [App::DocumentObjectGroupPython] G4_Ba  # scripted group (container) (typed FeaturePython)
  Dunit = g/cm3
  Dvalue = 3.5
  Group = -> [Ba_element003]
  conduct = 2
  density = 1
  expand = 3
  formula = Ba
  name = G4_Ba
  specific = 4
FEATURE [App::DocumentObjectGroupPython] La_element003  label="La_element : 003"  # scripted group (container) (typed FeaturePython)
  n = 1
  ref = La_element
FEATURE [App::DocumentObjectGroupPython] G4_La  # scripted group (container) (typed FeaturePython)
  Dunit = g/cm3
  Dvalue = 6.154
  Group = -> [La_element003]
  conduct = 2
  density = 1
  expand = 3
  formula = La
  name = G4_La
  specific = 4
FEATURE [App::DocumentObjectGroupPython] Ce_element002  label="Ce_element : 1"  # scripted group (container) (typed FeaturePython)
  n = 1
  ref = Ce_element
FEATURE [App::DocumentObjectGroupPython] G4_Ce  # scripted group (container) (typed FeaturePython)
  Dunit = g/cm3
  Dvalue = 6.657
  Group = -> [Ce_element002]
  conduct = 2
  density = 1
  expand = 3
  formula = Ce
  name = G4_Ce
  specific = 4
FEATURE [App::DocumentObjectGroupPython] Pr_element001  label="Pr_element : 1"  # scripted group (container) (typed FeaturePython)
  n = 1
  ref = Pr_element
FEATURE [App::DocumentObjectGroupPython] G4_Pr  # scripted group (container) (typed FeaturePython)
  Dunit = g/cm3
  Dvalue = 6.71
  Group = -> [Pr_element001]
  conduct = 2
  density = 1
  expand = 3
  formula = Pr
  name = G4_Pr
  specific = 4
FEATURE [App::DocumentObjectGroupPython] Nd_element001  label="Nd_element : 1"  # scripted group (container) (typed FeaturePython)
  n = 1
  ref = Nd_element
FEATURE [App::DocumentObjectGroupPython] G4_Nd  # scripted group (container) (typed FeaturePython)
  Dunit = g/cm3
  Dvalue = 6.9
  Group = -> [Nd_element001]
  conduct = 2
  density = 1
  expand = 3
  formula = Nd
  name = G4_Nd
  specific = 4
FEATURE [App::DocumentObjectGroupPython] Pm_element001  label="Pm_element : 1"  # scripted group (container) (typed FeaturePython)
  n = 1
  ref = Pm_element
FEATURE [App::DocumentObjectGroupPython] G4_Pm  # scripted group (container) (typed FeaturePython)
  Dunit = g/cm3
  Dvalue = 7.22
  Group = -> [Pm_element001]
  conduct = 2
  density = 1
  expand = 3
  formula = Pm
  name = G4_Pm
  specific = 4
FEATURE [App::DocumentObjectGroupPython] Sm_element001  label="Sm_element : 1"  # scripted group (container) (typed FeaturePython)
  n = 1
  ref = Sm_element
FEATURE [App::DocumentObjectGroupPython] G4_Sm  # scripted group (container) (typed FeaturePython)
  Dunit = g/cm3
  Dvalue = 7.46
  Group = -> [Sm_element001]
  conduct = 2
  density = 1
  expand = 3
  formula = Sm
  name = G4_Sm
  specific = 4
FEATURE [App::DocumentObjectGroupPython] Eu_element001  label="Eu_element : 1"  # scripted group (container) (typed FeaturePython)
  n = 1
  ref = Eu_element
FEATURE [App::DocumentObjectGroupPython] G4_Eu  # scripted group (container) (typed FeaturePython)
  Dunit = g/cm3
  Dvalue = 5.243
  Group = -> [Eu_element001]
  conduct = 2
  density = 1
  expand = 3
  formula = Eu
  name = G4_Eu
  specific = 4
FEATURE [App::DocumentObjectGroupPython] Gd_element002  label="Gd_element : 1"  # scripted group (container) (typed FeaturePython)
  n = 1
  ref = Gd_element
FEATURE [App::DocumentObjectGroupPython] G4_Gd  # scripted group (container) (typed FeaturePython)
  Dunit = g/cm3
  Dvalue = 7.9004
  Group = -> [Gd_element002]
  conduct = 2
  density = 1
  expand = 3
  formula = Gd
  name = G4_Gd
  specific = 4
FEATURE [App::DocumentObjectGroupPython] Tb_element001  label="Tb_element : 1"  # scripted group (container) (typed FeaturePython)
  n = 1
  ref = Tb_element
FEATURE [App::DocumentObjectGroupPython] G4_Tb  # scripted group (container) (typed FeaturePython)
  Dunit = g/cm3
  Dvalue = 8.229
  Group = -> [Tb_element001]
  conduct = 2
  density = 1
  expand = 3
  formula = Tb
  name = G4_Tb
  specific = 4
FEATURE [App::DocumentObjectGroupPython] Dy_element001  label="Dy_element : 1"  # scripted group (container) (typed FeaturePython)
  n = 1
  ref = Dy_element
FEATURE [App::DocumentObjectGroupPython] G4_Dy  # scripted group (container) (typed FeaturePython)
  Dunit = g/cm3
  Dvalue = 8.55
  Group = -> [Dy_element001]
  conduct = 2
  density = 1
  expand = 3
  formula = Dy
  name = G4_Dy
  specific = 4
FEATURE [App::DocumentObjectGroupPython] Ho_element001  label="Ho_element : 1"  # scripted group (container) (typed FeaturePython)
  n = 1
  ref = Ho_element
FEATURE [App::DocumentObjectGroupPython] G4_Ho  # scripted group (container) (typed FeaturePython)
  Dunit = g/cm3
  Dvalue = 8.795
  Group = -> [Ho_element001]
  conduct = 2
  density = 1
  expand = 3
  formula = Ho
  name = G4_Ho
  specific = 4
FEATURE [App::DocumentObjectGroupPython] Er_element001  label="Er_element : 1"  # scripted group (container) (typed FeaturePython)
  n = 1
  ref = Er_element
FEATURE [App::DocumentObjectGroupPython] G4_Er  # scripted group (container) (typed FeaturePython)
  Dunit = g/cm3
  Dvalue = 9.066
  Group = -> [Er_element001]
  conduct = 2
  density = 1
  expand = 3
  formula = Er
  name = G4_Er
  specific = 4
FEATURE [App::DocumentObjectGroupPython] Tm_element001  label="Tm_element : 1"  # scripted group (container) (typed FeaturePython)
  n = 1
  ref = Tm_element
FEATURE [App::DocumentObjectGroupPython] G4_Tm  # scripted group (container) (typed FeaturePython)
  Dunit = g/cm3
  Dvalue = 9.321
  Group = -> [Tm_element001]
  conduct = 2
  density = 1
  expand = 3
  formula = Tm
  name = G4_Tm
  specific = 4
FEATURE [App::DocumentObjectGroupPython] Yb_element001  label="Yb_element : 1"  # scripted group (container) (typed FeaturePython)
  n = 1
  ref = Yb_element
FEATURE [App::DocumentObjectGroupPython] G4_Yb  # scripted group (container) (typed FeaturePython)
  Dunit = g/cm3
  Dvalue = 6.73
  Group = -> [Yb_element001]
  conduct = 2
  density = 1
  expand = 3
  formula = Yb
  name = G4_Yb
  specific = 4
FEATURE [App::DocumentObjectGroupPython] Lu_element001  label="Lu_element : 1"  # scripted group (container) (typed FeaturePython)
  n = 1
  ref = Lu_element
FEATURE [App::DocumentObjectGroupPython] G4_Lu  # scripted group (container) (typed FeaturePython)
  Dunit = g/cm3
  Dvalue = 9.84
  Group = -> [Lu_element001]
  conduct = 2
  density = 1
  expand = 3
  formula = Lu
  name = G4_Lu
  specific = 4
FEATURE [App::DocumentObjectGroupPython] Hf_element001  label="Hf_element : 1"  # scripted group (container) (typed FeaturePython)
  n = 1
  ref = Hf_element
FEATURE [App::DocumentObjectGroupPython] G4_Hf  # scripted group (container) (typed FeaturePython)
  Dunit = g/cm3
  Dvalue = 13.31
  Group = -> [Hf_element001]
  conduct = 2
  density = 1
  expand = 3
  formula = Hf
  name = G4_Hf
  specific = 4
FEATURE [App::DocumentObjectGroupPython] Ta_element001  label="Ta_element : 1"  # scripted group (container) (typed FeaturePython)
  n = 1
  ref = Ta_element
FEATURE [App::DocumentObjectGroupPython] G4_Ta  # scripted group (container) (typed FeaturePython)
  Dunit = g/cm3
  Dvalue = 16.654
  Group = -> [Ta_element001]
  conduct = 2
  density = 1
  expand = 3
  formula = Ta
  name = G4_Ta
  specific = 4
FEATURE [App::DocumentObjectGroupPython] W_element004  label="W_element : 004"  # scripted group (container) (typed FeaturePython)
  n = 1
  ref = W_element
FEATURE [App::DocumentObjectGroupPython] G4_W  # scripted group (container) (typed FeaturePython)
  Dunit = g/cm3
  Dvalue = 19.3
  Group = -> [W_element004]
  conduct = 2
  density = 1
  expand = 3
  formula = W
  name = G4_W
  specific = 4
FEATURE [App::DocumentObjectGroupPython] Re_element001  label="Re_element : 1"  # scripted group (container) (typed FeaturePython)
  n = 1
  ref = Re_element
FEATURE [App::DocumentObjectGroupPython] G4_Re  # scripted group (container) (typed FeaturePython)
  Dunit = g/cm3
  Dvalue = 21.02
  Group = -> [Re_element001]
  conduct = 2
  density = 1
  expand = 3
  formula = Re
  name = G4_Re
  specific = 4
FEATURE [App::DocumentObjectGroupPython] Os_element001  label="Os_element : 1"  # scripted group (container) (typed FeaturePython)
  n = 1
  ref = Os_element
FEATURE [App::DocumentObjectGroupPython] G4_Os  # scripted group (container) (typed FeaturePython)
  Dunit = g/cm3
  Dvalue = 22.57
  Group = -> [Os_element001]
  conduct = 2
  density = 1
  expand = 3
  formula = Os
  name = G4_Os
  specific = 4
FEATURE [App::DocumentObjectGroupPython] Ir_element001  label="Ir_element : 1"  # scripted group (container) (typed FeaturePython)
  n = 1
  ref = Ir_element
FEATURE [App::DocumentObjectGroupPython] G4_Ir  # scripted group (container) (typed FeaturePython)
  Dunit = g/cm3
  Dvalue = 22.42
  Group = -> [Ir_element001]
  conduct = 2
  density = 1
  expand = 3
  formula = Ir
  name = G4_Ir
  specific = 4
FEATURE [App::DocumentObjectGroupPython] Pt_element001  label="Pt_element : 1"  # scripted group (container) (typed FeaturePython)
  n = 1
  ref = Pt_element
FEATURE [App::DocumentObjectGroupPython] G4_Pt  # scripted group (container) (typed FeaturePython)
  Dunit = g/cm3
  Dvalue = 21.45
  Group = -> [Pt_element001]
  conduct = 2
  density = 1
  expand = 3
  formula = Pt
  name = G4_Pt
  specific = 4
FEATURE [App::DocumentObjectGroupPython] Au_element001  label="Au_element : 1"  # scripted group (container) (typed FeaturePython)
  n = 1
  ref = Au_element
FEATURE [App::DocumentObjectGroupPython] G4_Au  # scripted group (container) (typed FeaturePython)
  Dunit = g/cm3
  Dvalue = 19.32
  Group = -> [Au_element001]
  conduct = 2
  density = 1
  expand = 3
  formula = Au
  name = G4_Au
  specific = 4
FEATURE [App::DocumentObjectGroupPython] Hg_element002  label="Hg_element : 002"  # scripted group (container) (typed FeaturePython)
  n = 1
  ref = Hg_element
FEATURE [App::DocumentObjectGroupPython] G4_Hg  # scripted group (container) (typed FeaturePython)
  Dunit = g/cm3
  Dvalue = 13.546
  Group = -> [Hg_element002]
  conduct = 2
  density = 1
  expand = 3
  formula = Hg
  name = G4_Hg
  specific = 4
FEATURE [App::DocumentObjectGroupPython] Tl_element002  label="Tl_element : 002"  # scripted group (container) (typed FeaturePython)
  n = 1
  ref = Tl_element
FEATURE [App::DocumentObjectGroupPython] G4_Tl  # scripted group (container) (typed FeaturePython)
  Dunit = g/cm3
  Dvalue = 11.72
  Group = -> [Tl_element002]
  conduct = 2
  density = 1
  expand = 3
  formula = Tl
  name = G4_Tl
  specific = 4
FEATURE [App::DocumentObjectGroupPython] Pb_element003  label="Pb_element : 1"  # scripted group (container) (typed FeaturePython)
  n = 1
  ref = Pb_element
FEATURE [App::DocumentObjectGroupPython] G4_Pb  # scripted group (container) (typed FeaturePython)
  Dunit = g/cm3
  Dvalue = 11.35
  Group = -> [Pb_element003]
  conduct = 2
  density = 1
  expand = 3
  formula = Pb
  name = G4_Pb
  specific = 4
FEATURE [App::DocumentObjectGroupPython] Bi_element002  label="Bi_element : 1"  # scripted group (container) (typed FeaturePython)
  n = 1
  ref = Bi_element
FEATURE [App::DocumentObjectGroupPython] G4_Bi  # scripted group (container) (typed FeaturePython)
  Dunit = g/cm3
  Dvalue = 9.747
  Group = -> [Bi_element002]
  conduct = 2
  density = 1
  expand = 3
  formula = Bi
  name = G4_Bi
  specific = 4
FEATURE [App::DocumentObjectGroupPython] Po_element001  label="Po_element : 1"  # scripted group (container) (typed FeaturePython)
  n = 1
  ref = Po_element
FEATURE [App::DocumentObjectGroupPython] G4_Po  # scripted group (container) (typed FeaturePython)
  Dunit = g/cm3
  Dvalue = 9.32
  Group = -> [Po_element001]
  conduct = 2
  density = 1
  expand = 3
  formula = Po
  name = G4_Po
  specific = 4
FEATURE [App::DocumentObjectGroupPython] At_element001  label="At_element : 1"  # scripted group (container) (typed FeaturePython)
  n = 1
  ref = At_element
FEATURE [App::DocumentObjectGroupPython] G4_At  # scripted group (container) (typed FeaturePython)
  Dunit = g/cm3
  Dvalue = 9.32
  Group = -> [At_element001]
  conduct = 2
  density = 1
  expand = 3
  formula = At
  name = G4_At
  specific = 4
FEATURE [App::DocumentObjectGroupPython] Rn_element001  label="Rn_element : 1"  # scripted group (container) (typed FeaturePython)
  n = 1
  ref = Rn_element
FEATURE [App::DocumentObjectGroupPython] G4_Rn  # scripted group (container) (typed FeaturePython)
  Dunit = g/cm3
  Dvalue = 0.00900662
  Group = -> [Rn_element001]
  conduct = 2
  density = 1
  expand = 3
  formula = Rn
  name = G4_Rn
  specific = 4
FEATURE [App::DocumentObjectGroupPython] Fr_element001  label="Fr_element : 1"  # scripted group (container) (typed FeaturePython)
  n = 1
  ref = Fr_element
FEATURE [App::DocumentObjectGroupPython] G4_Fr  # scripted group (container) (typed FeaturePython)
  Dunit = g/cm3
  Dvalue = 1
  Group = -> [Fr_element001]
  conduct = 2
  density = 1
  expand = 3
  formula = Fr
  name = G4_Fr
  specific = 4
FEATURE [App::DocumentObjectGroupPython] Ra_element001  label="Ra_element : 1"  # scripted group (container) (typed FeaturePython)
  n = 1
  ref = Ra_element
FEATURE [App::DocumentObjectGroupPython] G4_Ra  # scripted group (container) (typed FeaturePython)
  Dunit = g/cm3
  Dvalue = 5
  Group = -> [Ra_element001]
  conduct = 2
  density = 1
  expand = 3
  formula = Ra
  name = G4_Ra
  specific = 4
FEATURE [App::DocumentObjectGroupPython] Ac_element001  label="Ac_element : 1"  # scripted group (container) (typed FeaturePython)
  n = 1
  ref = Ac_element
FEATURE [App::DocumentObjectGroupPython] G4_Ac  # scripted group (container) (typed FeaturePython)
  Dunit = g/cm3
  Dvalue = 10.07
  Group = -> [Ac_element001]
  conduct = 2
  density = 1
  expand = 3
  formula = Ac
  name = G4_Ac
  specific = 4
FEATURE [App::DocumentObjectGroupPython] Th_element001  label="Th_element : 1"  # scripted group (container) (typed FeaturePython)
  n = 1
  ref = Th_element
FEATURE [App::DocumentObjectGroupPython] G4_Th  # scripted group (container) (typed FeaturePython)
  Dunit = g/cm3
  Dvalue = 11.72
  Group = -> [Th_element001]
  conduct = 2
  density = 1
  expand = 3
  formula = Th
  name = G4_Th
  specific = 4
FEATURE [App::DocumentObjectGroupPython] Pa_element001  label="Pa_element : 1"  # scripted group (container) (typed FeaturePython)
  n = 1
  ref = Pa_element
FEATURE [App::DocumentObjectGroupPython] G4_Pa  # scripted group (container) (typed FeaturePython)
  Dunit = g/cm3
  Dvalue = 15.37
  Group = -> [Pa_element001]
  conduct = 2
  density = 1
  expand = 3
  formula = Pa
  name = G4_Pa
  specific = 4
FEATURE [App::DocumentObjectGroupPython] U_element004  label="U_element : 004"  # scripted group (container) (typed FeaturePython)
  n = 1
  ref = U_element
FEATURE [App::DocumentObjectGroupPython] G4_U  # scripted group (container) (typed FeaturePython)
  Dunit = g/cm3
  Dvalue = 18.95
  Group = -> [U_element004]
  conduct = 2
  density = 1
  expand = 3
  formula = U
  name = G4_U
  specific = 4
FEATURE [App::DocumentObjectGroupPython] Np_element001  label="Np_element : 1"  # scripted group (container) (typed FeaturePython)
  n = 1
  ref = Np_element
FEATURE [App::DocumentObjectGroupPython] G4_Np  # scripted group (container) (typed FeaturePython)
  Dunit = g/cm3
  Dvalue = 20.25
  Group = -> [Np_element001]
  conduct = 2
  density = 1
  expand = 3
  formula = Np
  name = G4_Np
  specific = 4
FEATURE [App::DocumentObjectGroupPython] Pu_element002  label="Pu_element : 002"  # scripted group (container) (typed FeaturePython)
  n = 1
  ref = Pu_element
FEATURE [App::DocumentObjectGroupPython] G4_Pu  # scripted group (container) (typed FeaturePython)
  Dunit = g/cm3
  Dvalue = 19.84
  Group = -> [Pu_element002]
  conduct = 2
  density = 1
  expand = 3
  formula = Pu
  name = G4_Pu
  specific = 4
FEATURE [App::DocumentObjectGroupPython] Am_element001  label="Am_element : 1"  # scripted group (container) (typed FeaturePython)
  n = 1
  ref = Am_element
FEATURE [App::DocumentObjectGroupPython] G4_Am  # scripted group (container) (typed FeaturePython)
  Dunit = g/cm3
  Dvalue = 13.67
  Group = -> [Am_element001]
  conduct = 2
  density = 1
  expand = 3
  formula = Am
  name = G4_Am
  specific = 4
FEATURE [App::DocumentObjectGroupPython] Cm_element001  label="Cm_element : 1"  # scripted group (container) (typed FeaturePython)
  n = 1
  ref = Cm_element
FEATURE [App::DocumentObjectGroupPython] G4_Cm  # scripted group (container) (typed FeaturePython)
  Dunit = g/cm3
  Dvalue = 13.51
  Group = -> [Cm_element001]
  conduct = 2
  density = 1
  expand = 3
  formula = Cm
  name = G4_Cm
  specific = 4
FEATURE [App::DocumentObjectGroupPython] Bk_element001  label="Bk_element : 1"  # scripted group (container) (typed FeaturePython)
  n = 1
  ref = Bk_element
FEATURE [App::DocumentObjectGroupPython] G4_Bk  # scripted group (container) (typed FeaturePython)
  Dunit = g/cm3
  Dvalue = 14
  Group = -> [Bk_element001]
  conduct = 2
  density = 1
  expand = 3
  formula = Bk
  name = G4_Bk
  specific = 4
FEATURE [App::DocumentObjectGroupPython] Cf_element001  label="Cf_element : 1"  # scripted group (container) (typed FeaturePython)
  n = 1
  ref = Cf_element
FEATURE [App::DocumentObjectGroupPython] G4_Cf  # scripted group (container) (typed FeaturePython)
  Dunit = g/cm3
  Dvalue = 10
  Group = -> [Cf_element001]
  conduct = 2
  density = 1
  expand = 3
  formula = Cf
  name = G4_Cf
  specific = 4
FEATURE [App::DocumentObjectGroupPython] Element  # scripted group (container) (typed FeaturePython)
  Group = -> [G4_H,G4_He,G4_Li,G4_Be,G4_B,G4_C,G4_N,G4_O,G4_F,G4_Ne,G4_Na,G4_Mg,G4_Al,G4_Si,G4_P,G4_S,G4_Cl,G4_Ar,G4_K,G4_Ca,G4_Sc,G4_Ti,G4_V,G4_Cr,G4_Mn,G4_Fe,G4_Co,G4_Ni,G4_Cu,G4_Zn,G4_Ga,G4_Ge,G4_As,G4_Se,G4_Br,G4_Kr,G4_Rb,G4_Sr,G4_Y,G4_Zr,G4_Nb,G4_Mo,G4_Tc,G4_Ru,G4_Rh,G4_Pd,G4_Ag,G4_Cd,G4_In,G4_Sn,G4_Sb,G4_Te,G4_I,G4_Xe,G4_Cs,G4_Ba,G4_La,G4_Ce,G4_Pr,G4_Nd,G4_Pm,G4_Sm,G4_Eu,G4_Gd,G4_Tb,G4_Dy,G4_Ho,G4_Er,+30 more]
FEATURE [App::DocumentObjectGroupPython] H_element114  label="H_element : 063"  # scripted group (container) (typed FeaturePython)
  n = 2
  ref = H_element
FEATURE [App::DocumentObjectGroupPython] G4_lH2  # scripted group (container) (typed FeaturePython)
  Dunit = g/cm3
  Dvalue = 0.0708
  Group = -> [H_element114]
  conduct = 2
  density = 1
  expand = 3
  formula = G4_lH2
  name = G4_lH2
  specific = 4
FEATURE [App::DocumentObjectGroupPython] N_element049  label="N_element : 022"  # scripted group (container) (typed FeaturePython)
  n = 2
  ref = N_element
FEATURE [App::DocumentObjectGroupPython] G4_lN2  # scripted group (container) (typed FeaturePython)
  Dunit = g/cm3
  Dvalue = 0.807
  Group = -> [N_element049]
  conduct = 2
  density = 1
  expand = 3
  formula = G4_lN2
  name = G4_lN2
  specific = 4
FEATURE [App::DocumentObjectGroupPython] O_element106  label="O_element : 060"  # scripted group (container) (typed FeaturePython)
  n = 2
  ref = O_element
FEATURE [App::DocumentObjectGroupPython] G4_lO2  # scripted group (container) (typed FeaturePython)
  Dunit = g/cm3
  Dvalue = 1.141
  Group = -> [O_element106]
  conduct = 2
  density = 1
  expand = 3
  formula = G4_lO2
  name = G4_lO2
  specific = 4
FEATURE [App::DocumentObjectGroupPython] Ar  label="Ar : 1"  # scripted group (container) (typed FeaturePython)
  n = 1
  ref = Ar
FEATURE [App::DocumentObjectGroupPython] G4_lAr  # scripted group (container) (typed FeaturePython)
  Dunit = g/cm3
  Dvalue = 1.396
  Group = -> [Ar]
  conduct = 2
  density = 1
  expand = 3
  formula = G4_lAr
  name = G4_lAr
  specific = 4
FEATURE [App::DocumentObjectGroupPython] Br  label="Br : 1"  # scripted group (container) (typed FeaturePython)
  n = 1
  ref = Br
FEATURE [App::DocumentObjectGroupPython] G4_lBr  # scripted group (container) (typed FeaturePython)
  Dunit = g/cm3
  Dvalue = 3.1028
  Group = -> [Br]
  conduct = 2
  density = 1
  expand = 3
  formula = G4_lBr
  name = G4_lBr
  specific = 4
FEATURE [App::DocumentObjectGroupPython] Kr  label="Kr : 1"  # scripted group (container) (typed FeaturePython)
  n = 1
  ref = Kr
FEATURE [App::DocumentObjectGroupPython] G4_lKr  # scripted group (container) (typed FeaturePython)
  Dunit = g/cm3
  Dvalue = 2.418
  Group = -> [Kr]
  conduct = 2
  density = 1
  expand = 3
  formula = G4_lKr
  name = G4_lKr
  specific = 4
FEATURE [App::DocumentObjectGroupPython] Xe  label="Xe : 1"  # scripted group (container) (typed FeaturePython)
  n = 1
  ref = Xe
FEATURE [App::DocumentObjectGroupPython] G4_lXe  # scripted group (container) (typed FeaturePython)
  Dunit = g/cm3
  Dvalue = 2.953
  Group = -> [Xe]
  conduct = 2
  density = 1
  expand = 3
  formula = G4_lXe
  name = G4_lXe
  specific = 4
FEATURE [App::DocumentObjectGroupPython] O_element107  label="O_element : 061"  # scripted group (container) (typed FeaturePython)
  n = 4
  ref = O_element
FEATURE [App::DocumentObjectGroupPython] Pb_element004  label="Pb_element : 002"  # scripted group (container) (typed FeaturePython)
  n = 1
  ref = Pb_element
FEATURE [App::DocumentObjectGroupPython] W_element005  label="W_element : 005"  # scripted group (container) (typed FeaturePython)
  n = 1
  ref = W_element
FEATURE [App::DocumentObjectGroupPython] G4_PbWO4  # scripted group (container) (typed FeaturePython)
  Dunit = g/cm3
  Dvalue = 8.28
  Group = -> [O_element107,Pb_element004,W_element005]
  conduct = 2
  density = 1
  expand = 3
  formula = G4_PbWO4
  name = G4_PbWO4
  specific = 4
FEATURE [App::DocumentObjectGroupPython] alactic  label="alactic : 1"  # scripted group (container) (typed FeaturePython)
  n = 1
  ref = alactic
FEATURE [App::DocumentObjectGroupPython] G4_Galactic  # scripted group (container) (typed FeaturePython)
  Dunit = g/cm3
  Dvalue = 0
  Group = -> [alactic]
  conduct = 2
  density = 1
  expand = 3
  formula = G4_Galactic
  name = G4_Galactic
  specific = 4
FEATURE [App::DocumentObjectGroupPython] RAPHITE_POROUS  label="RAPHITE_POROUS : 1"  # scripted group (container) (typed FeaturePython)
  n = 1
  ref = RAPHITE_POROUS
FEATURE [App::DocumentObjectGroupPython] G4_GRAPHITE_POROUS  # scripted group (container) (typed FeaturePython)
  Dunit = g/cm3
  Dvalue = 1.7
  Group = -> [RAPHITE_POROUS]
  conduct = 2
  density = 1
  expand = 3
  formula = G4_GRAPHITE_POROUS
  name = G4_GRAPHITE_POROUS
  specific = 4
FEATURE [App::DocumentObjectGroupPython] H_element115  label="H_element : 0.150"  # scripted group (container) (typed FeaturePython)
  n = 0.080538
FEATURE [App::DocumentObjectGroupPython] C_element125  label="C_element : 0.600"  # scripted group (container) (typed FeaturePython)
  n = 0.599848
FEATURE [App::DocumentObjectGroupPython] O_element108  label="O_element : 0.320"  # scripted group (container) (typed FeaturePython)
  n = 0.319614
FEATURE [App::DocumentObjectGroupPython] G4_LUCITE  # scripted group (container) (typed FeaturePython)
  Dunit = g/cm3
  Dvalue = 1.19
  Group = -> [H_element115,C_element125,O_element108]
  conduct = 2
  density = 1
  expand = 3
  formula = G4_LUCITE
  name = G4_LUCITE
  specific = 4
FEATURE [App::DocumentObjectGroupPython] Cu_element002  label="Cu_element : 62"  # scripted group (container) (typed FeaturePython)
  n = 62
  ref = Cu_element
FEATURE [App::DocumentObjectGroupPython] Zn_element002  label="Zn_element : 35"  # scripted group (container) (typed FeaturePython)
  n = 35
  ref = Zn_element
FEATURE [App::DocumentObjectGroupPython] Pb_element005  label="Pb_element : 3"  # scripted group (container) (typed FeaturePython)
  n = 3
  ref = Pb_element
FEATURE [App::DocumentObjectGroupPython] G4_BRASS  # scripted group (container) (typed FeaturePython)
  Dunit = g/cm3
  Dvalue = 8.52
  Group = -> [Cu_element002,Zn_element002,Pb_element005]
  conduct = 2
  density = 1
  expand = 3
  formula = G4_BRASS
  name = G4_BRASS
  specific = 4
FEATURE [App::DocumentObjectGroupPython] Cu_element003  label="Cu_element : 89"  # scripted group (container) (typed FeaturePython)
  n = 89
  ref = Cu_element
FEATURE [App::DocumentObjectGroupPython] Zn_element003  label="Zn_element : 9"  # scripted group (container) (typed FeaturePython)
  n = 9
  ref = Zn_element
FEATURE [App::DocumentObjectGroupPython] Pb_element006  label="Pb_element : 2"  # scripted group (container) (typed FeaturePython)
  n = 2
  ref = Pb_element
FEATURE [App::DocumentObjectGroupPython] G4_BRONZE  # scripted group (container) (typed FeaturePython)
  Dunit = g/cm3
  Dvalue = 8.82
  Group = -> [Cu_element003,Zn_element003,Pb_element006]
  conduct = 2
  density = 1
  expand = 3
  formula = G4_BRONZE
  name = G4_BRONZE
  specific = 4
FEATURE [App::DocumentObjectGroupPython] Fe_element008  label="Fe_element : 74"  # scripted group (container) (typed FeaturePython)
  n = 74
  ref = Fe_element
FEATURE [App::DocumentObjectGroupPython] Cr_element002  label="Cr_element : 18"  # scripted group (container) (typed FeaturePython)
  n = 18
  ref = Cr_element
FEATURE [App::DocumentObjectGroupPython] Ni_element002  label="Ni_element : 8"  # scripted group (container) (typed FeaturePython)
  n = 8
  ref = Ni_element
FEATURE [App::DocumentObjectGroupPython] G4_STAINLESS_STEEL  label="G4_STAINLESS-STEEL"  # scripted group (container) (typed FeaturePython)
  Dunit = g/cm3
  Dvalue = 8
  Group = -> [Fe_element008,Cr_element002,Ni_element002]
  conduct = 2
  density = 1
  expand = 3
  formula = G4_STAINLESS-STEEL
  name = G4_STAINLESS-STEEL
  specific = 4
FEATURE [App::DocumentObjectGroupPython] H_element116  label="H_element : 064"  # scripted group (container) (typed FeaturePython)
  n = 18
  ref = H_element
FEATURE [App::DocumentObjectGroupPython] C_element126  label="C_element : 071"  # scripted group (container) (typed FeaturePython)
  n = 12
  ref = C_element
FEATURE [App::DocumentObjectGroupPython] O_element109  label="O_element : 062"  # scripted group (container) (typed FeaturePython)
  n = 7
  ref = O_element
FEATURE [App::DocumentObjectGroupPython] G4_CR39  # scripted group (container) (typed FeaturePython)
  Dunit = g/cm3
  Dvalue = 1.32
  Group = -> [H_element116,C_element126,O_element109]
  conduct = 2
  density = 1
  expand = 3
  formula = G4_CR39
  name = G4_CR39
  specific = 4
FEATURE [App::DocumentObjectGroupPython] H_element117  label="H_element : 38"  # scripted group (container) (typed FeaturePython)
  n = 38
  ref = H_element
FEATURE [App::DocumentObjectGroupPython] C_element127  label="C_element : 072"  # scripted group (container) (typed FeaturePython)
  n = 18
  ref = C_element
FEATURE [App::DocumentObjectGroupPython] O_element110  label="O_element : 063"  # scripted group (container) (typed FeaturePython)
  n = 1
  ref = O_element
FEATURE [App::DocumentObjectGroupPython] G4_OCTADECANOL  # scripted group (container) (typed FeaturePython)
  Dunit = g/cm3
  Dvalue = 0.812
  Group = -> [H_element117,C_element127,O_element110]
  conduct = 2
  density = 1
  expand = 3
  formula = G4_OCTADECANOL
  name = G4_OCTADECANOL
  specific = 4
FEATURE [App::DocumentObjectGroupPython] HEP  # scripted group (container) (typed FeaturePython)
  Group = -> [G4_lH2,G4_lN2,G4_lO2,G4_lAr,G4_lBr,G4_lKr,G4_lXe,G4_PbWO4,G4_Galactic,G4_GRAPHITE_POROUS,G4_LUCITE,G4_BRASS,G4_BRONZE,G4_STAINLESS_STEEL,G4_CR39,G4_OCTADECANOL]
FEATURE [App::DocumentObjectGroupPython] C_element128  label="C_element : 073"  # scripted group (container) (typed FeaturePython)
  n = 14
  ref = C_element
FEATURE [App::DocumentObjectGroupPython] H_element118  label="H_element : 065"  # scripted group (container) (typed FeaturePython)
  n = 10
  ref = H_element
FEATURE [App::DocumentObjectGroupPython] O_element111  label="O_element : 064"  # scripted group (container) (typed FeaturePython)
  n = 2
  ref = O_element
FEATURE [App::DocumentObjectGroupPython] N_element050  label="N_element : 023"  # scripted group (container) (typed FeaturePython)
  n = 2
  ref = N_element
FEATURE [App::DocumentObjectGroupPython] G4_KEVLAR  # scripted group (container) (typed FeaturePython)
  Dunit = g/cm3
  Dvalue = 1.44
  Group = -> [C_element128,H_element118,O_element111,N_element050]
  conduct = 2
  density = 1
  expand = 3
  formula = G4_KEVLAR
  name = G4_KEVLAR
  specific = 4
FEATURE [App::DocumentObjectGroupPython] C_element129  label="C_element : 074"  # scripted group (container) (typed FeaturePython)
  n = 10
  ref = C_element
FEATURE [App::DocumentObjectGroupPython] H_element119  label="H_element : 066"  # scripted group (container) (typed FeaturePython)
  n = 8
  ref = H_element
FEATURE [App::DocumentObjectGroupPython] O_element112  label="O_element : 065"  # scripted group (container) (typed FeaturePython)
  n = 4
  ref = O_element
FEATURE [App::DocumentObjectGroupPython] G4_DACRON  # scripted group (container) (typed FeaturePython)
  Dunit = g/cm3
  Dvalue = 1.4
  Group = -> [C_element129,H_element119,O_element112]
  conduct = 2
  density = 1
  expand = 3
  formula = G4_DACRON
  name = G4_DACRON
  specific = 4
FEATURE [App::DocumentObjectGroupPython] C_element130  label="C_element : 075"  # scripted group (container) (typed FeaturePython)
  n = 4
  ref = C_element
FEATURE [App::DocumentObjectGroupPython] H_element120  label="H_element : 067"  # scripted group (container) (typed FeaturePython)
  n = 5
  ref = H_element
FEATURE [App::DocumentObjectGroupPython] Cl_element030  label="Cl_element : 016"  # scripted group (container) (typed FeaturePython)
  n = 1
  ref = Cl_element
FEATURE [App::DocumentObjectGroupPython] G4_NEOPRENE  # scripted group (container) (typed FeaturePython)
  Dunit = g/cm3
  Dvalue = 1.23
  Group = -> [C_element130,H_element120,Cl_element030]
  conduct = 2
  density = 1
  expand = 3
  formula = G4_NEOPRENE
  name = G4_NEOPRENE
  specific = 4
FEATURE [App::DocumentObjectGroupPython] Space  # scripted group (container) (typed FeaturePython)
  Group = -> [G4_KEVLAR,G4_DACRON,G4_NEOPRENE]
FEATURE [App::DocumentObjectGroupPython] H_element121  label="H_element : 068"  # scripted group (container) (typed FeaturePython)
  n = 5
  ref = H_element
FEATURE [App::DocumentObjectGroupPython] C_element131  label="C_element : 076"  # scripted group (container) (typed FeaturePython)
  n = 4
  ref = C_element
FEATURE [App::DocumentObjectGroupPython] N_element051  label="N_element : 3"  # scripted group (container) (typed FeaturePython)
  n = 3
  ref = N_element
FEATURE [App::DocumentObjectGroupPython] O_element113  label="O_element : 066"  # scripted group (container) (typed FeaturePython)
  n = 1
  ref = O_element
FEATURE [App::DocumentObjectGroupPython] G4_CYTOSINE  # scripted group (container) (typed FeaturePython)
  Dunit = g/cm3
  Dvalue = 1.55
  Group = -> [H_element121,C_element131,N_element051,O_element113]
  conduct = 2
  density = 1
  expand = 3
  formula = G4_CYTOSINE
  name = G4_CYTOSINE
  specific = 4
FEATURE [App::DocumentObjectGroupPython] H_element122  label="H_element : 069"  # scripted group (container) (typed FeaturePython)
  n = 6
  ref = H_element
FEATURE [App::DocumentObjectGroupPython] C_element132  label="C_element : 077"  # scripted group (container) (typed FeaturePython)
  n = 5
  ref = C_element
FEATURE [App::DocumentObjectGroupPython] N_element052  label="N_element : 024"  # scripted group (container) (typed FeaturePython)
  n = 2
  ref = N_element
FEATURE [App::DocumentObjectGroupPython] O_element114  label="O_element : 067"  # scripted group (container) (typed FeaturePython)
  n = 2
  ref = O_element
FEATURE [App::DocumentObjectGroupPython] G4_THYMINE  # scripted group (container) (typed FeaturePython)
  Dunit = g/cm3
  Dvalue = 1.23
  Group = -> [H_element122,C_element132,N_element052,O_element114]
  conduct = 2
  density = 1
  expand = 3
  formula = G4_THYMINE
  name = G4_THYMINE
  specific = 4
FEATURE [App::DocumentObjectGroupPython] H_element123  label="H_element : 070"  # scripted group (container) (typed FeaturePython)
  n = 4
  ref = H_element
FEATURE [App::DocumentObjectGroupPython] C_element133  label="C_element : 078"  # scripted group (container) (typed FeaturePython)
  n = 4
  ref = C_element
FEATURE [App::DocumentObjectGroupPython] N_element053  label="N_element : 025"  # scripted group (container) (typed FeaturePython)
  n = 2
  ref = N_element
FEATURE [App::DocumentObjectGroupPython] O_element115  label="O_element : 068"  # scripted group (container) (typed FeaturePython)
  n = 2
  ref = O_element
FEATURE [App::DocumentObjectGroupPython] G4_URACIL  # scripted group (container) (typed FeaturePython)
  Dunit = g/cm3
  Dvalue = 1.32
  Group = -> [H_element123,C_element133,N_element053,O_element115]
  conduct = 2
  density = 1
  expand = 3
  formula = G4_URACIL
  name = G4_URACIL
  specific = 4
FEATURE [App::DocumentObjectGroupPython] H_element124  label="H_element : 071"  # scripted group (container) (typed FeaturePython)
  n = 4
  ref = H_element
FEATURE [App::DocumentObjectGroupPython] C_element134  label="C_element : 079"  # scripted group (container) (typed FeaturePython)
  n = 5
  ref = C_element
FEATURE [App::DocumentObjectGroupPython] N_element054  label="N_element : 026"  # scripted group (container) (typed FeaturePython)
  n = 5
  ref = N_element
FEATURE [App::DocumentObjectGroupPython] G4_DNA_ADENINE  # scripted group (container) (typed FeaturePython)
  Dunit = g/cm3
  Dvalue = 1
  Group = -> [H_element124,C_element134,N_element054]
  conduct = 2
  density = 1
  expand = 3
  formula = G4_DNA_ADENINE
  name = G4_DNA_ADENINE
  specific = 4
FEATURE [App::DocumentObjectGroupPython] H_element125  label="H_element : 072"  # scripted group (container) (typed FeaturePython)
  n = 4
  ref = H_element
FEATURE [App::DocumentObjectGroupPython] C_element135  label="C_element : 080"  # scripted group (container) (typed FeaturePython)
  n = 5
  ref = C_element
FEATURE [App::DocumentObjectGroupPython] N_element055  label="N_element : 027"  # scripted group (container) (typed FeaturePython)
  n = 5
  ref = N_element
FEATURE [App::DocumentObjectGroupPython] O_element116  label="O_element : 069"  # scripted group (container) (typed FeaturePython)
  n = 1
  ref = O_element
FEATURE [App::DocumentObjectGroupPython] G4_DNA_GUANINE  # scripted group (container) (typed FeaturePython)
  Dunit = g/cm3
  Dvalue = 1
  Group = -> [H_element125,C_element135,N_element055,O_element116]
  conduct = 2
  density = 1
  expand = 3
  formula = G4_DNA_GUANINE
  name = G4_DNA_GUANINE
  specific = 4
FEATURE [App::DocumentObjectGroupPython] H_element126  label="H_element : 073"  # scripted group (container) (typed FeaturePython)
  n = 4
  ref = H_element
FEATURE [App::DocumentObjectGroupPython] C_element136  label="C_element : 081"  # scripted group (container) (typed FeaturePython)
  n = 4
  ref = C_element
FEATURE [App::DocumentObjectGroupPython] N_element056  label="N_element : 028"  # scripted group (container) (typed FeaturePython)
  n = 3
  ref = N_element
FEATURE [App::DocumentObjectGroupPython] O_element117  label="O_element : 070"  # scripted group (container) (typed FeaturePython)
  n = 1
  ref = O_element
FEATURE [App::DocumentObjectGroupPython] G4_DNA_CYTOSINE  # scripted group (container) (typed FeaturePython)
  Dunit = g/cm3
  Dvalue = 1
  Group = -> [H_element126,C_element136,N_element056,O_element117]
  conduct = 2
  density = 1
  expand = 3
  formula = G4_DNA_CYTOSINE
  name = G4_DNA_CYTOSINE
  specific = 4
FEATURE [App::DocumentObjectGroupPython] H_element127  label="H_element : 074"  # scripted group (container) (typed FeaturePython)
  n = 5
  ref = H_element
FEATURE [App::DocumentObjectGroupPython] C_element137  label="C_element : 082"  # scripted group (container) (typed FeaturePython)
  n = 5
  ref = C_element
FEATURE [App::DocumentObjectGroupPython] N_element057  label="N_element : 029"  # scripted group (container) (typed FeaturePython)
  n = 2
  ref = N_element
FEATURE [App::DocumentObjectGroupPython] O_element118  label="O_element : 071"  # scripted group (container) (typed FeaturePython)
  n = 2
  ref = O_element
FEATURE [App::DocumentObjectGroupPython] G4_DNA_THYMINE  # scripted group (container) (typed FeaturePython)
  Dunit = g/cm3
  Dvalue = 1
  Group = -> [H_element127,C_element137,N_element057,O_element118]
  conduct = 2
  density = 1
  expand = 3
  formula = G4_DNA_THYMINE
  name = G4_DNA_THYMINE
  specific = 4
FEATURE [App::DocumentObjectGroupPython] H_element128  label="H_element : 075"  # scripted group (container) (typed FeaturePython)
  n = 3
  ref = H_element
FEATURE [App::DocumentObjectGroupPython] C_element138  label="C_element : 083"  # scripted group (container) (typed FeaturePython)
  n = 4
  ref = C_element
FEATURE [App::DocumentObjectGroupPython] N_element058  label="N_element : 030"  # scripted group (container) (typed FeaturePython)
  n = 2
  ref = N_element
FEATURE [App::DocumentObjectGroupPython] O_element119  label="O_element : 072"  # scripted group (container) (typed FeaturePython)
  n = 2
  ref = O_element
FEATURE [App::DocumentObjectGroupPython] G4_DNA_URACIL  # scripted group (container) (typed FeaturePython)
  Dunit = g/cm3
  Dvalue = 1
  Group = -> [H_element128,C_element138,N_element058,O_element119]
  conduct = 2
  density = 1
  expand = 3
  formula = G4_DNA_URACIL
  name = G4_DNA_URACIL
  specific = 4
FEATURE [App::DocumentObjectGroupPython] H_element129  label="H_element : 076"  # scripted group (container) (typed FeaturePython)
  n = 10
  ref = H_element
FEATURE [App::DocumentObjectGroupPython] C_element139  label="C_element : 084"  # scripted group (container) (typed FeaturePython)
  n = 10
  ref = C_element
FEATURE [App::DocumentObjectGroupPython] N_element059  label="N_element : 031"  # scripted group (container) (typed FeaturePython)
  n = 5
  ref = N_element
FEATURE [App::DocumentObjectGroupPython] O_element120  label="O_element : 073"  # scripted group (container) (typed FeaturePython)
  n = 4
  ref = O_element
FEATURE [App::DocumentObjectGroupPython] G4_DNA_ADENOSINE  # scripted group (container) (typed FeaturePython)
  Dunit = g/cm3
  Dvalue = 1
  Group = -> [H_element129,C_element139,N_element059,O_element120]
  conduct = 2
  density = 1
  expand = 3
  formula = G4_DNA_ADENOSINE
  name = G4_DNA_ADENOSINE
  specific = 4
FEATURE [App::DocumentObjectGroupPython] H_element130  label="H_element : 077"  # scripted group (container) (typed FeaturePython)
  n = 10
  ref = H_element
FEATURE [App::DocumentObjectGroupPython] C_element140  label="C_element : 085"  # scripted group (container) (typed FeaturePython)
  n = 10
  ref = C_element
FEATURE [App::DocumentObjectGroupPython] N_element060  label="N_element : 032"  # scripted group (container) (typed FeaturePython)
  n = 5
  ref = N_element
FEATURE [App::DocumentObjectGroupPython] O_element121  label="O_element : 074"  # scripted group (container) (typed FeaturePython)
  n = 5
  ref = O_element
FEATURE [App::DocumentObjectGroupPython] G4_DNA_GUANOSINE  # scripted group (container) (typed FeaturePython)
  Dunit = g/cm3
  Dvalue = 1
  Group = -> [H_element130,C_element140,N_element060,O_element121]
  conduct = 2
  density = 1
  expand = 3
  formula = G4_DNA_GUANOSINE
  name = G4_DNA_GUANOSINE
  specific = 4
FEATURE [App::DocumentObjectGroupPython] H_element131  label="H_element : 078"  # scripted group (container) (typed FeaturePython)
  n = 10
  ref = H_element
FEATURE [App::DocumentObjectGroupPython] C_element141  label="C_element : 086"  # scripted group (container) (typed FeaturePython)
  n = 9
  ref = C_element
FEATURE [App::DocumentObjectGroupPython] N_element061  label="N_element : 033"  # scripted group (container) (typed FeaturePython)
  n = 3
  ref = N_element
FEATURE [App::DocumentObjectGroupPython] O_element122  label="O_element : 075"  # scripted group (container) (typed FeaturePython)
  n = 5
  ref = O_element
FEATURE [App::DocumentObjectGroupPython] G4_DNA_CYTIDINE  # scripted group (container) (typed FeaturePython)
  Dunit = g/cm3
  Dvalue = 1
  Group = -> [H_element131,C_element141,N_element061,O_element122]
  conduct = 2
  density = 1
  expand = 3
  formula = G4_DNA_CYTIDINE
  name = G4_DNA_CYTIDINE
  specific = 4
FEATURE [App::DocumentObjectGroupPython] H_element132  label="H_element : 079"  # scripted group (container) (typed FeaturePython)
  n = 9
  ref = H_element
FEATURE [App::DocumentObjectGroupPython] C_element142  label="C_element : 087"  # scripted group (container) (typed FeaturePython)
  n = 9
  ref = C_element
FEATURE [App::DocumentObjectGroupPython] N_element062  label="N_element : 034"  # scripted group (container) (typed FeaturePython)
  n = 2
  ref = N_element
FEATURE [App::DocumentObjectGroupPython] O_element123  label="O_element : 076"  # scripted group (container) (typed FeaturePython)
  n = 6
  ref = O_element
FEATURE [App::DocumentObjectGroupPython] G4_DNA_URIDINE  # scripted group (container) (typed FeaturePython)
  Dunit = g/cm3
  Dvalue = 1
  Group = -> [H_element132,C_element142,N_element062,O_element123]
  conduct = 2
  density = 1
  expand = 3
  formula = G4_DNA_URIDINE
  name = G4_DNA_URIDINE
  specific = 4
FEATURE [App::DocumentObjectGroupPython] H_element133  label="H_element : 080"  # scripted group (container) (typed FeaturePython)
  n = 11
  ref = H_element
FEATURE [App::DocumentObjectGroupPython] C_element143  label="C_element : 088"  # scripted group (container) (typed FeaturePython)
  n = 10
  ref = C_element
FEATURE [App::DocumentObjectGroupPython] N_element063  label="N_element : 035"  # scripted group (container) (typed FeaturePython)
  n = 2
  ref = N_element
FEATURE [App::DocumentObjectGroupPython] O_element124  label="O_element : 077"  # scripted group (container) (typed FeaturePython)
  n = 6
  ref = O_element
FEATURE [App::DocumentObjectGroupPython] G4_DNA_METHYLURIDINE  # scripted group (container) (typed FeaturePython)
  Dunit = g/cm3
  Dvalue = 1
  Group = -> [H_element133,C_element143,N_element063,O_element124]
  conduct = 2
  density = 1
  expand = 3
  formula = G4_DNA_METHYLURIDINE
  name = G4_DNA_METHYLURIDINE
  specific = 4
FEATURE [App::DocumentObjectGroupPython] P_element014  label="P_element : 003"  # scripted group (container) (typed FeaturePython)
  n = 1
  ref = P_element
FEATURE [App::DocumentObjectGroupPython] O_element125  label="O_element : 078"  # scripted group (container) (typed FeaturePython)
  n = 3
  ref = O_element
FEATURE [App::DocumentObjectGroupPython] G4_DNA_MONOPHOSPHATE  # scripted group (container) (typed FeaturePython)
  Dunit = g/cm3
  Dvalue = 1
  Group = -> [P_element014,O_element125]
  conduct = 2
  density = 1
  expand = 3
  formula = G4_DNA_MONOPHOSPHATE
  name = G4_DNA_MONOPHOSPHATE
  specific = 4
FEATURE [App::DocumentObjectGroupPython] H_element134  label="H_element : 081"  # scripted group (container) (typed FeaturePython)
  n = 10
  ref = H_element
FEATURE [App::DocumentObjectGroupPython] C_element144  label="C_element : 089"  # scripted group (container) (typed FeaturePython)
  n = 10
  ref = C_element
FEATURE [App::DocumentObjectGroupPython] N_element064  label="N_element : 036"  # scripted group (container) (typed FeaturePython)
  n = 5
  ref = N_element
FEATURE [App::DocumentObjectGroupPython] O_element126  label="O_element : 079"  # scripted group (container) (typed FeaturePython)
  n = 7
  ref = O_element
FEATURE [App::DocumentObjectGroupPython] P_element015  label="P_element : 004"  # scripted group (container) (typed FeaturePython)
  n = 1
  ref = P_element
FEATURE [App::DocumentObjectGroupPython] G4_DNA_A  # scripted group (container) (typed FeaturePython)
  Dunit = g/cm3
  Dvalue = 1
  Group = -> [H_element134,C_element144,N_element064,O_element126,P_element015]
  conduct = 2
  density = 1
  expand = 3
  formula = G4_DNA_A
  name = G4_DNA_A
  specific = 4
FEATURE [App::DocumentObjectGroupPython] H_element135  label="H_element : 082"  # scripted group (container) (typed FeaturePython)
  n = 10
  ref = H_element
FEATURE [App::DocumentObjectGroupPython] C_element145  label="C_element : 090"  # scripted group (container) (typed FeaturePython)
  n = 10
  ref = C_element
FEATURE [App::DocumentObjectGroupPython] N_element065  label="N_element : 037"  # scripted group (container) (typed FeaturePython)
  n = 5
  ref = N_element
FEATURE [App::DocumentObjectGroupPython] O_element127  label="O_element : 8"  # scripted group (container) (typed FeaturePython)
  n = 8
  ref = O_element
FEATURE [App::DocumentObjectGroupPython] P_element016  label="P_element : 005"  # scripted group (container) (typed FeaturePython)
  n = 1
  ref = P_element
FEATURE [App::DocumentObjectGroupPython] G4_DNA_G  # scripted group (container) (typed FeaturePython)
  Dunit = g/cm3
  Dvalue = 1
  Group = -> [H_element135,C_element145,N_element065,O_element127,P_element016]
  conduct = 2
  density = 1
  expand = 3
  formula = G4_DNA_G
  name = G4_DNA_G
  specific = 4
FEATURE [App::DocumentObjectGroupPython] H_element136  label="H_element : 083"  # scripted group (container) (typed FeaturePython)
  n = 10
  ref = H_element
FEATURE [App::DocumentObjectGroupPython] C_element146  label="C_element : 091"  # scripted group (container) (typed FeaturePython)
  n = 9
  ref = C_element
FEATURE [App::DocumentObjectGroupPython] N_element066  label="N_element : 038"  # scripted group (container) (typed FeaturePython)
  n = 3
  ref = N_element
FEATURE [App::DocumentObjectGroupPython] O_element128  label="O_element : 080"  # scripted group (container) (typed FeaturePython)
  n = 8
  ref = O_element
FEATURE [App::DocumentObjectGroupPython] P_element017  label="P_element : 006"  # scripted group (container) (typed FeaturePython)
  n = 1
  ref = P_element
FEATURE [App::DocumentObjectGroupPython] G4_DNA_C  # scripted group (container) (typed FeaturePython)
  Dunit = g/cm3
  Dvalue = 1
  Group = -> [H_element136,C_element146,N_element066,O_element128,P_element017]
  conduct = 2
  density = 1
  expand = 3
  formula = G4_DNA_C
  name = G4_DNA_C
  specific = 4
FEATURE [App::DocumentObjectGroupPython] H_element137  label="H_element : 084"  # scripted group (container) (typed FeaturePython)
  n = 9
  ref = H_element
FEATURE [App::DocumentObjectGroupPython] C_element147  label="C_element : 092"  # scripted group (container) (typed FeaturePython)
  n = 9
  ref = C_element
FEATURE [App::DocumentObjectGroupPython] N_element067  label="N_element : 039"  # scripted group (container) (typed FeaturePython)
  n = 2
  ref = N_element
FEATURE [App::DocumentObjectGroupPython] O_element129  label="O_element : 9"  # scripted group (container) (typed FeaturePython)
  n = 9
  ref = O_element
FEATURE [App::DocumentObjectGroupPython] P_element018  label="P_element : 007"  # scripted group (container) (typed FeaturePython)
  n = 1
  ref = P_element
FEATURE [App::DocumentObjectGroupPython] G4_DNA_U  # scripted group (container) (typed FeaturePython)
  Dunit = g/cm3
  Dvalue = 1
  Group = -> [H_element137,C_element147,N_element067,O_element129,P_element018]
  conduct = 2
  density = 1
  expand = 3
  formula = G4_DNA_U
  name = G4_DNA_U
  specific = 4
FEATURE [App::DocumentObjectGroupPython] H_element138  label="H_element : 085"  # scripted group (container) (typed FeaturePython)
  n = 11
  ref = H_element
FEATURE [App::DocumentObjectGroupPython] C_element148  label="C_element : 093"  # scripted group (container) (typed FeaturePython)
  n = 10
  ref = C_element
FEATURE [App::DocumentObjectGroupPython] N_element068  label="N_element : 040"  # scripted group (container) (typed FeaturePython)
  n = 2
  ref = N_element
FEATURE [App::DocumentObjectGroupPython] O_element130  label="O_element : 081"  # scripted group (container) (typed FeaturePython)
  n = 9
  ref = O_element
FEATURE [App::DocumentObjectGroupPython] P_element019  label="P_element : 008"  # scripted group (container) (typed FeaturePython)
  n = 1
  ref = P_element
FEATURE [App::DocumentObjectGroupPython] G4_DNA_MU  # scripted group (container) (typed FeaturePython)
  Dunit = g/cm3
  Dvalue = 1
  Group = -> [H_element138,C_element148,N_element068,O_element130,P_element019]
  conduct = 2
  density = 1
  expand = 3
  formula = G4_DNA_MU
  name = G4_DNA_MU
  specific = 4
FEATURE [App::DocumentObjectGroupPython] BioChemical  # scripted group (container) (typed FeaturePython)
  Group = -> [G4_CYTOSINE,G4_THYMINE,G4_URACIL,G4_DNA_ADENINE,G4_DNA_GUANINE,G4_DNA_CYTOSINE,G4_DNA_THYMINE,G4_DNA_URACIL,G4_DNA_ADENOSINE,G4_DNA_GUANOSINE,G4_DNA_CYTIDINE,G4_DNA_URIDINE,G4_DNA_METHYLURIDINE,G4_DNA_MONOPHOSPHATE,G4_DNA_A,G4_DNA_G,G4_DNA_C,G4_DNA_U,G4_DNA_MU]
FEATURE [App::DocumentObjectGroupPython] G4Materials  # scripted group (container) (typed FeaturePython)
  Group = -> [NIST,Element,HEP,Space,BioChemical]
  version = 1
FEATURE [App::DocumentObjectGroupPython] Geant4  # scripted group (container) (typed FeaturePython)
  Group = -> [G4Isotopes,G4Elements,G4Materials]
FEATURE [App::DocumentObjectGroupPython] Materials  # scripted group (container) (typed FeaturePython)
  Group = -> [LYSO,Air,Glass,Geant4]
FEATURE [Part::FeaturePython] GDMLBox_World  # WARN: FeaturePython — macro-defined, semantics opaque (R4)
  lunit = 2
  material = 1
  x = 50
  y = 50
  z = 50
FEATURE [Part::FeaturePython] GDMLBox_Obj  # WARN: FeaturePython — macro-defined, semantics opaque (R4)
  lunit = 2
  material = 0
  x = 2
  y = 2
  z = 15
FEATURE [Part::FeaturePython] GDMLBox_GlassPlate  # WARN: FeaturePython — macro-defined, semantics opaque (R4)
  lunit = 2
  material = 2
  x = 2
  y = 2
  z = 2
FEATURE [App::Part] Det
  CopyNumber = 0
  Group = -> [GDMLBox_GlassPlate]
  Origin = -> Origin002
  Placement = pos=(0,0,8.5) rot=(0,0,1;0rad)
  SensDet = PhotonDetector
  SkinSurface = 0
FEATURE [App::FeaturePython] ScintWrap0  # WARN: FeaturePython — macro-defined, semantics opaque (R4)
  PV1 = Obj
  PV2 = Det
  Surface = ScintWrap
FEATURE [App::Part] Obj
  Group = -> [GDMLBox_Obj,Det,ScintWrap0]
  Origin = -> Origin001
  SensDet = Radiator
  SkinSurface = 0
FEATURE [Part::FeaturePython] Array  # Draft array (typed FeaturePython)
  AlwaysSyncPlacement = false
  Angle = 360
  ArrayType = 0
  Axis = (0,0,1)
  Base = -> Obj
  Center = (0,0,0)
  Count = 4
  ExpandArray = false
  Fuse = false
  IntervalAxis = (0,0,0)
  IntervalX = (3,0,0)
  IntervalY = (0,3,0)
  IntervalZ = (0,0,0)
  NumberCircles = 3
  NumberPolar = 5
  NumberX = 2
  NumberY = 2
  NumberZ = 1
  PlacementList = 4 placements: [(0,0,0),(0,3,0),(3,0,0),(3,3,0)]
  RadialDistance = 50
  ScaleList = (4) [(1,1,1),(1,1,1),(1,1,1),(1,1,1)]
  Symmetry = 1
  TangentialDistance = 25
  exportFlag = false
FEATURE [Part::FeaturePython] GDMLBox_Obj001  # WARN: FeaturePython — macro-defined, semantics opaque (R4)
  CopyNumber = 1
  lunit = 2
  material = 0
  x = 2
  y = 2
  z = 15
FEATURE [Part::FeaturePython] GDMLBox_GlassPlate001  # WARN: FeaturePython — macro-defined, semantics opaque (R4)
  CopyNumber = 1
  lunit = 2
  material = 2
  x = 2
  y = 2
  z = 2
FEATURE [App::Part] Det001
  CopyNumber = 1
  Group = -> [GDMLBox_GlassPlate001]
  Origin = -> Origin005
  Placement = pos=(0,0,8.5) rot=(0,0,1;0rad)
FEATURE [App::FeaturePython] ScintWrap001  # WARN: FeaturePython — macro-defined, semantics opaque (R4)
  PV1 = Obj001
  PV2 = Det001
  Surface = ScintWrap
FEATURE [App::Part] Obj001
  CopyNumber = 1
  Group = -> [GDMLBox_Obj001,Det001,ScintWrap001]
  Origin = -> Origin004
FEATURE [App::Link] Link_Obj001
  CopyNumber = 2
  LinkedObject = -> Obj001
FEATURE [App::Link] Link_Obj001001
  CopyNumber = 3
  LinkPlacement = pos=(0,3,0) rot=(0,0,1;0rad)
  LinkedObject = -> Obj001
  Placement = pos=(0,3,0) rot=(0,0,1;0rad)
FEATURE [App::Link] Link_Obj001002
  CopyNumber = 4
  LinkPlacement = pos=(3,0,0) rot=(0,0,1;0rad)
  LinkedObject = -> Obj001
  Placement = pos=(3,0,0) rot=(0,0,1;0rad)
FEATURE [App::Link] Link_Obj001003
  CopyNumber = 5
  LinkPlacement = pos=(3,3,0) rot=(0,0,1;0rad)
  LinkedObject = -> Obj001
  Placement = pos=(3,3,0) rot=(0,0,1;0rad)
FEATURE [App::Part] Array001
  Group = -> [Obj001,Link_Obj001,Link_Obj001001,Link_Obj001002,Link_Obj001003]
  Origin = -> Origin003
FEATURE [App::Part] Part
  Group = -> [Obj,Array,Array001]
  Origin = -> Origin006
FEATURE [App::Part] World
  Group = -> [GDMLBox_World,Part]
  Origin = -> Origin
